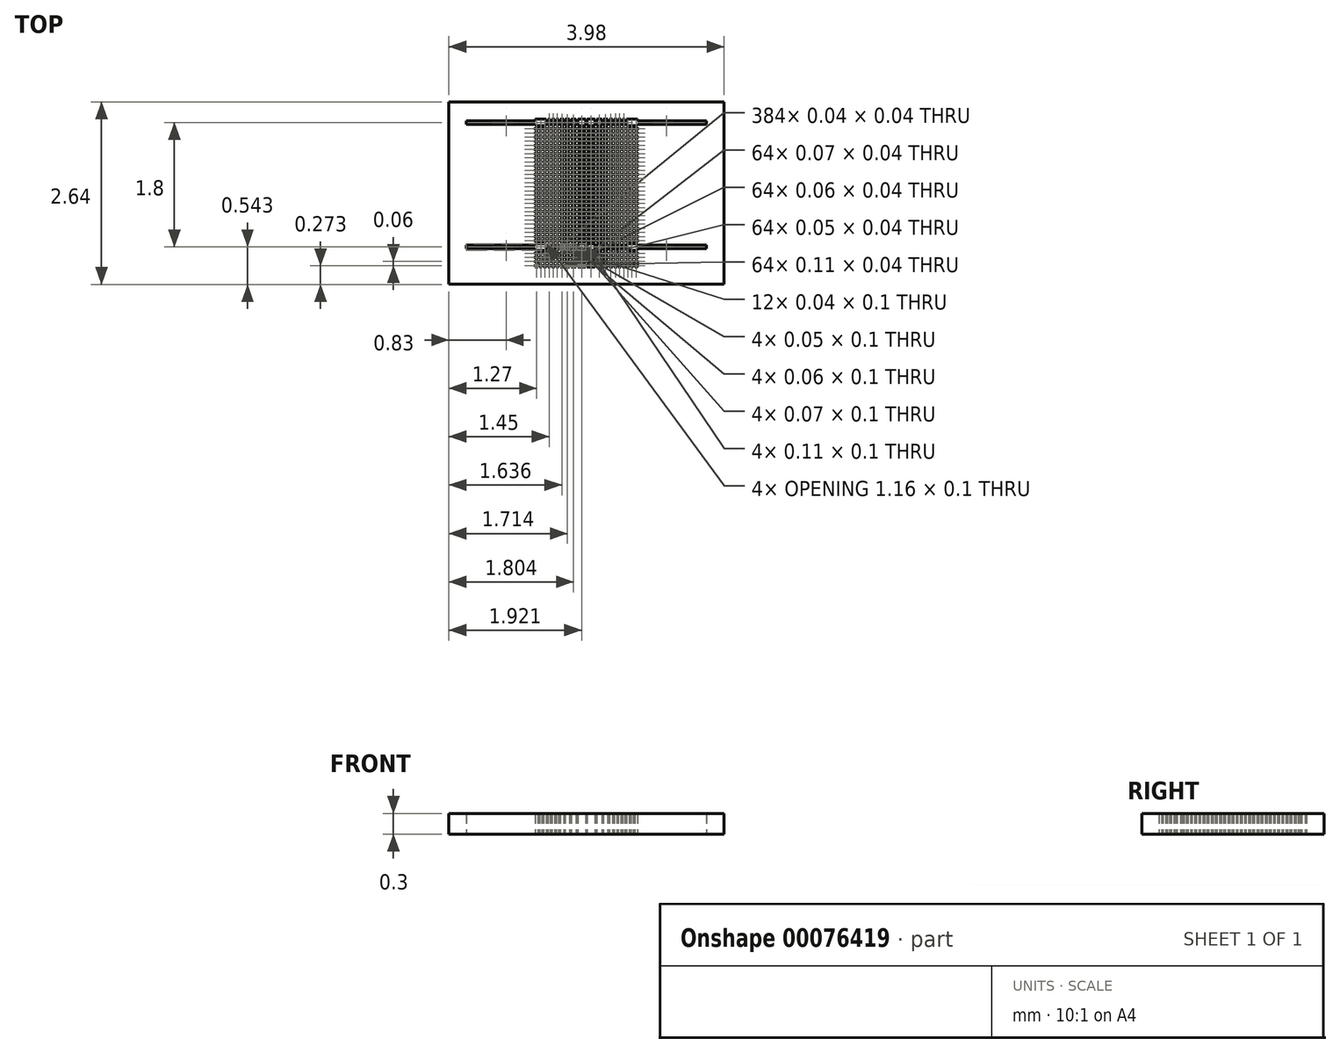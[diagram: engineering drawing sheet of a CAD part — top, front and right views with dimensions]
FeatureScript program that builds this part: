
annotation { "Feature Type Name" : "Feature", "Feature Type Description" : "" }
export const myFeature = defineFeature(function(context is Context, id is Id, definition is map)
    precondition{}
    {
        {
            var Q0;
            Q0=qCreatedBy(makeId("Top.planeOp"),FACE);
            var sketch = newSketch(context, id + "F0", { "sketchPlane" : qUnion([Q0])});
            skLineSegment(sketch, "E0", {"start": v(-0.58, -1.23) * mm, "end": v(-0.58, -1.33) * mm});
            skLineSegment(sketch, "E1", {"start": v(-0.56, -1.23) * mm, "end": v(-0.56, -1.33) * mm});
            skLineSegment(sketch, "E2", {"start": v(-0.52, -1.23) * mm, "end": v(-0.52, -1.33) * mm});
            skLineSegment(sketch, "E3", {"start": v(-0.52, -1.33) * mm, "end": v(-0.56, -1.33) * mm});
            skLineSegment(sketch, "E4", {"start": v(-0.5, -1.23) * mm, "end": v(-0.5, -1.33) * mm});
            skLineSegment(sketch, "E5", {"start": v(-0.46, -1.23) * mm, "end": v(-0.46, -1.33) * mm});
            skLineSegment(sketch, "E6", {"start": v(-0.46, -1.33) * mm, "end": v(-0.5, -1.33) * mm});
            skLineSegment(sketch, "E7", {"start": v(-0.44, -1.23) * mm, "end": v(-0.44, -1.33) * mm});
            skLineSegment(sketch, "E8", {"start": v(-0.4, -1.23) * mm, "end": v(-0.4, -1.33) * mm});
            skLineSegment(sketch, "E9", {"start": v(-0.4, -1.33) * mm, "end": v(-0.44, -1.33) * mm});
            skLineSegment(sketch, "E10", {"start": v(-0.74, -1.35) * mm, "end": v(-0.74, -1.39) * mm});
            skLineSegment(sketch, "E11", {"start": v(-0.7, -1.35) * mm, "end": v(-0.74, -1.35) * mm});
            skLineSegment(sketch, "E12", {"start": v(-0.7, -1.39) * mm, "end": v(-0.74, -1.39) * mm});
            skLineSegment(sketch, "E13", {"start": v(-0.7, -1.35) * mm, "end": v(-0.7, -1.39) * mm});
            skLineSegment(sketch, "E14", {"start": v(-0.7, -1.4) * mm, "end": v(-0.74, -1.4) * mm});
            skLineSegment(sketch, "E15", {"start": v(-0.7, -1.45) * mm, "end": v(-0.74, -1.45) * mm});
            skLineSegment(sketch, "E16", {"start": v(-0.74, -1.4) * mm, "end": v(-0.74, -1.45) * mm});
            skLineSegment(sketch, "E17", {"start": v(-0.7, -1.4) * mm, "end": v(-0.7, -1.45) * mm});
            skLineSegment(sketch, "E18", {"start": v(-0.7, -1.47) * mm, "end": v(-0.74, -1.47) * mm});
            skLineSegment(sketch, "E19", {"start": v(-0.7, -1.5) * mm, "end": v(-0.74, -1.5) * mm});
            skLineSegment(sketch, "E20", {"start": v(-0.74, -1.47) * mm, "end": v(-0.74, -1.5) * mm});
            skLineSegment(sketch, "E21", {"start": v(-0.7, -1.47) * mm, "end": v(-0.7, -1.5) * mm});
            skLineSegment(sketch, "E22", {"start": v(-0.7, -1.53) * mm, "end": v(-0.74, -1.53) * mm});
            skLineSegment(sketch, "E23", {"start": v(-0.7, -1.57) * mm, "end": v(-0.74, -1.57) * mm});
            skLineSegment(sketch, "E24", {"start": v(-0.74, -1.53) * mm, "end": v(-0.74, -1.57) * mm});
            skLineSegment(sketch, "E25", {"start": v(-0.7, -1.53) * mm, "end": v(-0.7, -1.57) * mm});
            skLineSegment(sketch, "E26", {"start": v(-0.7, -1.59) * mm, "end": v(-0.74, -1.59) * mm});
            skLineSegment(sketch, "E27", {"start": v(-0.7, -1.63) * mm, "end": v(-0.74, -1.63) * mm});
            skLineSegment(sketch, "E28", {"start": v(-0.74, -1.59) * mm, "end": v(-0.74, -1.63) * mm});
            skLineSegment(sketch, "E29", {"start": v(-0.7, -1.59) * mm, "end": v(-0.7, -1.63) * mm});
            skLineSegment(sketch, "E30", {"start": v(-0.7, -1.65) * mm, "end": v(-0.74, -1.65) * mm});
            skLineSegment(sketch, "E31", {"start": v(-0.7, -1.69) * mm, "end": v(-0.74, -1.69) * mm});
            skLineSegment(sketch, "E32", {"start": v(-0.74, -1.65) * mm, "end": v(-0.74, -1.69) * mm});
            skLineSegment(sketch, "E33", {"start": v(-0.7, -1.65) * mm, "end": v(-0.7, -1.69) * mm});
            skLineSegment(sketch, "E34", {"start": v(-0.64, -1.35) * mm, "end": v(-0.68, -1.35) * mm});
            skLineSegment(sketch, "E35", {"start": v(-0.64, -1.39) * mm, "end": v(-0.68, -1.39) * mm});
            skLineSegment(sketch, "E36", {"start": v(-0.68, -1.35) * mm, "end": v(-0.68, -1.39) * mm});
            skLineSegment(sketch, "E37", {"start": v(-0.64, -1.35) * mm, "end": v(-0.64, -1.39) * mm});
            skLineSegment(sketch, "E38", {"start": v(-0.64, -1.4) * mm, "end": v(-0.68, -1.4) * mm});
            skLineSegment(sketch, "E39", {"start": v(-0.64, -1.45) * mm, "end": v(-0.68, -1.45) * mm});
            skLineSegment(sketch, "E40", {"start": v(-0.68, -1.4) * mm, "end": v(-0.68, -1.45) * mm});
            skLineSegment(sketch, "E41", {"start": v(-0.64, -1.4) * mm, "end": v(-0.64, -1.45) * mm});
            skLineSegment(sketch, "E42", {"start": v(-0.64, -1.47) * mm, "end": v(-0.68, -1.47) * mm});
            skLineSegment(sketch, "E43", {"start": v(-0.64, -1.5) * mm, "end": v(-0.68, -1.5) * mm});
            skLineSegment(sketch, "E44", {"start": v(-0.68, -1.47) * mm, "end": v(-0.68, -1.5) * mm});
            skLineSegment(sketch, "E45", {"start": v(-0.64, -1.47) * mm, "end": v(-0.64, -1.5) * mm});
            skLineSegment(sketch, "E46", {"start": v(-0.64, -1.53) * mm, "end": v(-0.68, -1.53) * mm});
            skLineSegment(sketch, "E47", {"start": v(-0.64, -1.57) * mm, "end": v(-0.68, -1.57) * mm});
            skLineSegment(sketch, "E48", {"start": v(-0.68, -1.53) * mm, "end": v(-0.68, -1.57) * mm});
            skLineSegment(sketch, "E49", {"start": v(-0.64, -1.53) * mm, "end": v(-0.64, -1.57) * mm});
            skLineSegment(sketch, "E50", {"start": v(-0.64, -1.59) * mm, "end": v(-0.68, -1.59) * mm});
            skLineSegment(sketch, "E51", {"start": v(-0.64, -1.63) * mm, "end": v(-0.68, -1.63) * mm});
            skLineSegment(sketch, "E52", {"start": v(-0.68, -1.59) * mm, "end": v(-0.68, -1.63) * mm});
            skLineSegment(sketch, "E53", {"start": v(-0.64, -1.59) * mm, "end": v(-0.64, -1.63) * mm});
            skLineSegment(sketch, "E54", {"start": v(-0.64, -1.65) * mm, "end": v(-0.68, -1.65) * mm});
            skLineSegment(sketch, "E55", {"start": v(-0.64, -1.69) * mm, "end": v(-0.68, -1.69) * mm});
            skLineSegment(sketch, "E56", {"start": v(-0.68, -1.65) * mm, "end": v(-0.68, -1.69) * mm});
            skLineSegment(sketch, "E57", {"start": v(-0.64, -1.65) * mm, "end": v(-0.64, -1.69) * mm});
            skLineSegment(sketch, "E58", {"start": v(-0.58, -1.35) * mm, "end": v(-0.62, -1.35) * mm});
            skLineSegment(sketch, "E59", {"start": v(-0.58, -1.39) * mm, "end": v(-0.62, -1.39) * mm});
            skLineSegment(sketch, "E60", {"start": v(-0.62, -1.35) * mm, "end": v(-0.62, -1.39) * mm});
            skLineSegment(sketch, "E61", {"start": v(-0.58, -1.35) * mm, "end": v(-0.58, -1.39) * mm});
            skLineSegment(sketch, "E62", {"start": v(-0.58, -1.4) * mm, "end": v(-0.62, -1.4) * mm});
            skLineSegment(sketch, "E63", {"start": v(-0.58, -1.45) * mm, "end": v(-0.62, -1.45) * mm});
            skLineSegment(sketch, "E64", {"start": v(-0.62, -1.4) * mm, "end": v(-0.62, -1.45) * mm});
            skLineSegment(sketch, "E65", {"start": v(-0.58, -1.4) * mm, "end": v(-0.58, -1.45) * mm});
            skLineSegment(sketch, "E66", {"start": v(-0.58, -1.47) * mm, "end": v(-0.62, -1.47) * mm});
            skLineSegment(sketch, "E67", {"start": v(-0.58, -1.5) * mm, "end": v(-0.62, -1.5) * mm});
            skLineSegment(sketch, "E68", {"start": v(-0.62, -1.47) * mm, "end": v(-0.62, -1.5) * mm});
            skLineSegment(sketch, "E69", {"start": v(-0.58, -1.47) * mm, "end": v(-0.58, -1.5) * mm});
            skLineSegment(sketch, "E70", {"start": v(-0.58, -1.53) * mm, "end": v(-0.62, -1.53) * mm});
            skLineSegment(sketch, "E71", {"start": v(-0.58, -1.57) * mm, "end": v(-0.62, -1.57) * mm});
            skLineSegment(sketch, "E72", {"start": v(-0.62, -1.53) * mm, "end": v(-0.62, -1.57) * mm});
            skLineSegment(sketch, "E73", {"start": v(-0.58, -1.53) * mm, "end": v(-0.58, -1.57) * mm});
            skLineSegment(sketch, "E74", {"start": v(-0.58, -1.59) * mm, "end": v(-0.62, -1.59) * mm});
            skLineSegment(sketch, "E75", {"start": v(-0.58, -1.63) * mm, "end": v(-0.62, -1.63) * mm});
            skLineSegment(sketch, "E76", {"start": v(-0.62, -1.59) * mm, "end": v(-0.62, -1.63) * mm});
            skLineSegment(sketch, "E77", {"start": v(-0.58, -1.59) * mm, "end": v(-0.58, -1.63) * mm});
            skLineSegment(sketch, "E78", {"start": v(-0.58, -1.65) * mm, "end": v(-0.62, -1.65) * mm});
            skLineSegment(sketch, "E79", {"start": v(-0.58, -1.69) * mm, "end": v(-0.62, -1.69) * mm});
            skLineSegment(sketch, "E80", {"start": v(-0.62, -1.65) * mm, "end": v(-0.62, -1.69) * mm});
            skLineSegment(sketch, "E81", {"start": v(-0.58, -1.65) * mm, "end": v(-0.58, -1.69) * mm});
            skLineSegment(sketch, "E82", {"start": v(-0.52, -1.35) * mm, "end": v(-0.56, -1.35) * mm});
            skLineSegment(sketch, "E83", {"start": v(-0.52, -1.39) * mm, "end": v(-0.56, -1.39) * mm});
            skLineSegment(sketch, "E84", {"start": v(-0.56, -1.35) * mm, "end": v(-0.56, -1.39) * mm});
            skLineSegment(sketch, "E85", {"start": v(-0.52, -1.35) * mm, "end": v(-0.52, -1.39) * mm});
            skLineSegment(sketch, "E86", {"start": v(-0.52, -1.4) * mm, "end": v(-0.56, -1.4) * mm});
            skLineSegment(sketch, "E87", {"start": v(-0.52, -1.45) * mm, "end": v(-0.56, -1.45) * mm});
            skLineSegment(sketch, "E88", {"start": v(-0.56, -1.4) * mm, "end": v(-0.56, -1.45) * mm});
            skLineSegment(sketch, "E89", {"start": v(-0.52, -1.4) * mm, "end": v(-0.52, -1.45) * mm});
            skLineSegment(sketch, "E90", {"start": v(-0.52, -1.47) * mm, "end": v(-0.56, -1.47) * mm});
            skLineSegment(sketch, "E91", {"start": v(-0.52, -1.5) * mm, "end": v(-0.56, -1.5) * mm});
            skLineSegment(sketch, "E92", {"start": v(-0.56, -1.47) * mm, "end": v(-0.56, -1.5) * mm});
            skLineSegment(sketch, "E93", {"start": v(-0.52, -1.47) * mm, "end": v(-0.52, -1.5) * mm});
            skLineSegment(sketch, "E94", {"start": v(-0.52, -1.53) * mm, "end": v(-0.56, -1.53) * mm});
            skLineSegment(sketch, "E95", {"start": v(-0.52, -1.57) * mm, "end": v(-0.56, -1.57) * mm});
            skLineSegment(sketch, "E96", {"start": v(-0.56, -1.53) * mm, "end": v(-0.56, -1.57) * mm});
            skLineSegment(sketch, "E97", {"start": v(-0.52, -1.53) * mm, "end": v(-0.52, -1.57) * mm});
            skLineSegment(sketch, "E98", {"start": v(-0.52, -1.59) * mm, "end": v(-0.56, -1.59) * mm});
            skLineSegment(sketch, "E99", {"start": v(-0.52, -1.63) * mm, "end": v(-0.56, -1.63) * mm});
            skLineSegment(sketch, "E100", {"start": v(-0.56, -1.59) * mm, "end": v(-0.56, -1.63) * mm});
            skLineSegment(sketch, "E101", {"start": v(-0.52, -1.59) * mm, "end": v(-0.52, -1.63) * mm});
            skLineSegment(sketch, "E102", {"start": v(-0.52, -1.65) * mm, "end": v(-0.56, -1.65) * mm});
            skLineSegment(sketch, "E103", {"start": v(-0.52, -1.69) * mm, "end": v(-0.56, -1.69) * mm});
            skLineSegment(sketch, "E104", {"start": v(-0.56, -1.65) * mm, "end": v(-0.56, -1.69) * mm});
            skLineSegment(sketch, "E105", {"start": v(-0.52, -1.65) * mm, "end": v(-0.52, -1.69) * mm});
            skLineSegment(sketch, "E106", {"start": v(-0.46, -1.35) * mm, "end": v(-0.5, -1.35) * mm});
            skLineSegment(sketch, "E107", {"start": v(-0.46, -1.39) * mm, "end": v(-0.5, -1.39) * mm});
            skLineSegment(sketch, "E108", {"start": v(-0.5, -1.35) * mm, "end": v(-0.5, -1.39) * mm});
            skLineSegment(sketch, "E109", {"start": v(-0.46, -1.35) * mm, "end": v(-0.46, -1.39) * mm});
            skLineSegment(sketch, "E110", {"start": v(-0.46, -1.4) * mm, "end": v(-0.5, -1.4) * mm});
            skLineSegment(sketch, "E111", {"start": v(-0.46, -1.45) * mm, "end": v(-0.5, -1.45) * mm});
            skLineSegment(sketch, "E112", {"start": v(-0.5, -1.4) * mm, "end": v(-0.5, -1.45) * mm});
            skLineSegment(sketch, "E113", {"start": v(-0.46, -1.4) * mm, "end": v(-0.46, -1.45) * mm});
            skLineSegment(sketch, "E114", {"start": v(-0.46, -1.47) * mm, "end": v(-0.5, -1.47) * mm});
            skLineSegment(sketch, "E115", {"start": v(-0.46, -1.5) * mm, "end": v(-0.5, -1.5) * mm});
            skLineSegment(sketch, "E116", {"start": v(-0.5, -1.47) * mm, "end": v(-0.5, -1.5) * mm});
            skLineSegment(sketch, "E117", {"start": v(-0.46, -1.47) * mm, "end": v(-0.46, -1.5) * mm});
            skLineSegment(sketch, "E118", {"start": v(-0.46, -1.53) * mm, "end": v(-0.5, -1.53) * mm});
            skLineSegment(sketch, "E119", {"start": v(-0.46, -1.57) * mm, "end": v(-0.5, -1.57) * mm});
            skLineSegment(sketch, "E120", {"start": v(-0.5, -1.53) * mm, "end": v(-0.5, -1.57) * mm});
            skLineSegment(sketch, "E121", {"start": v(-0.46, -1.53) * mm, "end": v(-0.46, -1.57) * mm});
            skLineSegment(sketch, "E122", {"start": v(-0.46, -1.59) * mm, "end": v(-0.5, -1.59) * mm});
            skLineSegment(sketch, "E123", {"start": v(-0.46, -1.63) * mm, "end": v(-0.5, -1.63) * mm});
            skLineSegment(sketch, "E124", {"start": v(-0.5, -1.59) * mm, "end": v(-0.5, -1.63) * mm});
            skLineSegment(sketch, "E125", {"start": v(-0.46, -1.59) * mm, "end": v(-0.46, -1.63) * mm});
            skLineSegment(sketch, "E126", {"start": v(-0.46, -1.65) * mm, "end": v(-0.5, -1.65) * mm});
            skLineSegment(sketch, "E127", {"start": v(-0.46, -1.69) * mm, "end": v(-0.5, -1.69) * mm});
            skLineSegment(sketch, "E128", {"start": v(-0.5, -1.65) * mm, "end": v(-0.5, -1.69) * mm});
            skLineSegment(sketch, "E129", {"start": v(-0.46, -1.65) * mm, "end": v(-0.46, -1.69) * mm});
            skLineSegment(sketch, "E130", {"start": v(-0.4, -1.35) * mm, "end": v(-0.44, -1.35) * mm});
            skLineSegment(sketch, "E131", {"start": v(-0.4, -1.39) * mm, "end": v(-0.44, -1.39) * mm});
            skLineSegment(sketch, "E132", {"start": v(-0.44, -1.35) * mm, "end": v(-0.44, -1.39) * mm});
            skLineSegment(sketch, "E133", {"start": v(-0.4, -1.35) * mm, "end": v(-0.4, -1.39) * mm});
            skLineSegment(sketch, "E134", {"start": v(-0.4, -1.4) * mm, "end": v(-0.44, -1.4) * mm});
            skLineSegment(sketch, "E135", {"start": v(-0.4, -1.45) * mm, "end": v(-0.44, -1.45) * mm});
            skLineSegment(sketch, "E136", {"start": v(-0.44, -1.4) * mm, "end": v(-0.44, -1.45) * mm});
            skLineSegment(sketch, "E137", {"start": v(-0.4, -1.4) * mm, "end": v(-0.4, -1.45) * mm});
            skLineSegment(sketch, "E138", {"start": v(-0.4, -1.47) * mm, "end": v(-0.44, -1.47) * mm});
            skLineSegment(sketch, "E139", {"start": v(-0.4, -1.5) * mm, "end": v(-0.44, -1.5) * mm});
            skLineSegment(sketch, "E140", {"start": v(-0.44, -1.47) * mm, "end": v(-0.44, -1.5) * mm});
            skLineSegment(sketch, "E141", {"start": v(-0.4, -1.47) * mm, "end": v(-0.4, -1.5) * mm});
            skLineSegment(sketch, "E142", {"start": v(-0.4, -1.53) * mm, "end": v(-0.44, -1.53) * mm});
            skLineSegment(sketch, "E143", {"start": v(-0.4, -1.57) * mm, "end": v(-0.44, -1.57) * mm});
            skLineSegment(sketch, "E144", {"start": v(-0.44, -1.53) * mm, "end": v(-0.44, -1.57) * mm});
            skLineSegment(sketch, "E145", {"start": v(-0.4, -1.53) * mm, "end": v(-0.4, -1.57) * mm});
            skLineSegment(sketch, "E146", {"start": v(-0.4, -1.59) * mm, "end": v(-0.44, -1.59) * mm});
            skLineSegment(sketch, "E147", {"start": v(-0.4, -1.63) * mm, "end": v(-0.44, -1.63) * mm});
            skLineSegment(sketch, "E148", {"start": v(-0.44, -1.59) * mm, "end": v(-0.44, -1.63) * mm});
            skLineSegment(sketch, "E149", {"start": v(-0.4, -1.59) * mm, "end": v(-0.4, -1.63) * mm});
            skLineSegment(sketch, "E150", {"start": v(-0.4, -1.65) * mm, "end": v(-0.44, -1.65) * mm});
            skLineSegment(sketch, "E151", {"start": v(-0.4, -1.69) * mm, "end": v(-0.44, -1.69) * mm});
            skLineSegment(sketch, "E152", {"start": v(-0.44, -1.65) * mm, "end": v(-0.44, -1.69) * mm});
            skLineSegment(sketch, "E153", {"start": v(-0.4, -1.65) * mm, "end": v(-0.4, -1.69) * mm});
            skLineSegment(sketch, "E154", {"start": v(-0.38, -1.23) * mm, "end": v(-0.38, -1.33) * mm});
            skLineSegment(sketch, "E155", {"start": v(-0.38, -1.35) * mm, "end": v(-0.38, -1.39) * mm});
            skLineSegment(sketch, "E156", {"start": v(-0.33, -1.23) * mm, "end": v(-0.33, -1.33) * mm});
            skLineSegment(sketch, "E157", {"start": v(-0.33, -1.35) * mm, "end": v(-0.33, -1.39) * mm});
            skLineSegment(sketch, "E158", {"start": v(-0.3, -1.23) * mm, "end": v(-0.3, -1.33) * mm});
            skLineSegment(sketch, "E159", {"start": v(-0.3, -1.35) * mm, "end": v(-0.3, -1.39) * mm});
            skLineSegment(sketch, "E160", {"start": v(-0.25, -1.23) * mm, "end": v(-0.25, -1.33) * mm});
            skLineSegment(sketch, "E161", {"start": v(-0.25, -1.35) * mm, "end": v(-0.25, -1.39) * mm});
            skLineSegment(sketch, "E162", {"start": v(-0.22, -1.23) * mm, "end": v(-0.22, -1.33) * mm});
            skLineSegment(sketch, "E163", {"start": v(-0.22, -1.35) * mm, "end": v(-0.22, -1.39) * mm});
            skLineSegment(sketch, "E164", {"start": v(-0.15, -1.23) * mm, "end": v(-0.15, -1.33) * mm});
            skLineSegment(sketch, "E165", {"start": v(-0.15, -1.35) * mm, "end": v(-0.15, -1.39) * mm});
            skLineSegment(sketch, "E166", {"start": v(-0.13, -1.23) * mm, "end": v(-0.13, -1.33) * mm});
            skLineSegment(sketch, "E167", {"start": v(-0.13, -1.35) * mm, "end": v(-0.13, -1.39) * mm});
            skLineSegment(sketch, "E168", {"start": v(-0.01, -1.23) * mm, "end": v(-0.01, -1.33) * mm});
            skLineSegment(sketch, "E169", {"start": v(-0.13, -1.35) * mm, "end": v(-0.01, -1.35) * mm});
            skLineSegment(sketch, "E170", {"start": v(-0.13, -1.33) * mm, "end": v(-0.01, -1.33) * mm});
            skLineSegment(sketch, "E171", {"start": v(-0.13, -1.39) * mm, "end": v(-0.01, -1.39) * mm});
            skLineSegment(sketch, "E172", {"start": v(-0.15, -1.35) * mm, "end": v(-0.22, -1.35) * mm});
            skLineSegment(sketch, "E173", {"start": v(-0.22, -1.39) * mm, "end": v(-0.15, -1.39) * mm});
            skLineSegment(sketch, "E174", {"start": v(-0.25, -1.35) * mm, "end": v(-0.3, -1.35) * mm});
            skLineSegment(sketch, "E175", {"start": v(-0.3, -1.39) * mm, "end": v(-0.25, -1.39) * mm});
            skLineSegment(sketch, "E176", {"start": v(-0.33, -1.35) * mm, "end": v(-0.38, -1.35) * mm});
            skLineSegment(sketch, "E177", {"start": v(-0.38, -1.39) * mm, "end": v(-0.33, -1.39) * mm});
            skLineSegment(sketch, "E178", {"start": v(-0.38, -1.33) * mm, "end": v(-0.33, -1.33) * mm});
            skLineSegment(sketch, "E179", {"start": v(-0.3, -1.33) * mm, "end": v(-0.25, -1.33) * mm});
            skLineSegment(sketch, "E180", {"start": v(-0.22, -1.33) * mm, "end": v(-0.15, -1.33) * mm});
            skLineSegment(sketch, "E181", {"start": v(-0.01, -1.35) * mm, "end": v(-0.01, -1.39) * mm});
            skLineSegment(sketch, "E182", {"start": v(-0.01, -1.4) * mm, "end": v(-0.01, -1.45) * mm});
            skLineSegment(sketch, "E183", {"start": v(-0.38, -1.4) * mm, "end": v(-0.38, -1.45) * mm});
            skLineSegment(sketch, "E184", {"start": v(-0.33, -1.4) * mm, "end": v(-0.33, -1.45) * mm});
            skLineSegment(sketch, "E185", {"start": v(-0.3, -1.4) * mm, "end": v(-0.3, -1.45) * mm});
            skLineSegment(sketch, "E186", {"start": v(-0.25, -1.4) * mm, "end": v(-0.25, -1.45) * mm});
            skLineSegment(sketch, "E187", {"start": v(-0.22, -1.4) * mm, "end": v(-0.22, -1.45) * mm});
            skLineSegment(sketch, "E188", {"start": v(-0.15, -1.4) * mm, "end": v(-0.15, -1.45) * mm});
            skLineSegment(sketch, "E189", {"start": v(-0.13, -1.4) * mm, "end": v(-0.13, -1.45) * mm});
            skLineSegment(sketch, "E190", {"start": v(-0.13, -1.4) * mm, "end": v(-0.01, -1.4) * mm});
            skLineSegment(sketch, "E191", {"start": v(-0.13, -1.45) * mm, "end": v(-0.01, -1.45) * mm});
            skLineSegment(sketch, "E192", {"start": v(-0.15, -1.4) * mm, "end": v(-0.22, -1.4) * mm});
            skLineSegment(sketch, "E193", {"start": v(-0.22, -1.45) * mm, "end": v(-0.15, -1.45) * mm});
            skLineSegment(sketch, "E194", {"start": v(-0.25, -1.4) * mm, "end": v(-0.3, -1.4) * mm});
            skLineSegment(sketch, "E195", {"start": v(-0.3, -1.45) * mm, "end": v(-0.25, -1.45) * mm});
            skLineSegment(sketch, "E196", {"start": v(-0.33, -1.4) * mm, "end": v(-0.38, -1.4) * mm});
            skLineSegment(sketch, "E197", {"start": v(-0.38, -1.45) * mm, "end": v(-0.33, -1.45) * mm});
            skLineSegment(sketch, "E198", {"start": v(-0.01, -1.47) * mm, "end": v(-0.01, -1.5) * mm});
            skLineSegment(sketch, "E199", {"start": v(-0.38, -1.47) * mm, "end": v(-0.38, -1.5) * mm});
            skLineSegment(sketch, "E200", {"start": v(-0.33, -1.47) * mm, "end": v(-0.33, -1.5) * mm});
            skLineSegment(sketch, "E201", {"start": v(-0.3, -1.47) * mm, "end": v(-0.3, -1.5) * mm});
            skLineSegment(sketch, "E202", {"start": v(-0.25, -1.47) * mm, "end": v(-0.25, -1.5) * mm});
            skLineSegment(sketch, "E203", {"start": v(-0.22, -1.47) * mm, "end": v(-0.22, -1.5) * mm});
            skLineSegment(sketch, "E204", {"start": v(-0.15, -1.47) * mm, "end": v(-0.15, -1.5) * mm});
            skLineSegment(sketch, "E205", {"start": v(-0.13, -1.47) * mm, "end": v(-0.13, -1.5) * mm});
            skLineSegment(sketch, "E206", {"start": v(-0.13, -1.47) * mm, "end": v(-0.01, -1.47) * mm});
            skLineSegment(sketch, "E207", {"start": v(-0.13, -1.5) * mm, "end": v(-0.01, -1.5) * mm});
            skLineSegment(sketch, "E208", {"start": v(-0.15, -1.47) * mm, "end": v(-0.22, -1.47) * mm});
            skLineSegment(sketch, "E209", {"start": v(-0.22, -1.5) * mm, "end": v(-0.15, -1.5) * mm});
            skLineSegment(sketch, "E210", {"start": v(-0.25, -1.47) * mm, "end": v(-0.3, -1.47) * mm});
            skLineSegment(sketch, "E211", {"start": v(-0.3, -1.5) * mm, "end": v(-0.25, -1.5) * mm});
            skLineSegment(sketch, "E212", {"start": v(-0.33, -1.47) * mm, "end": v(-0.38, -1.47) * mm});
            skLineSegment(sketch, "E213", {"start": v(-0.38, -1.5) * mm, "end": v(-0.33, -1.5) * mm});
            skLineSegment(sketch, "E214", {"start": v(-0.01, -1.53) * mm, "end": v(-0.01, -1.57) * mm});
            skLineSegment(sketch, "E215", {"start": v(-0.38, -1.53) * mm, "end": v(-0.38, -1.57) * mm});
            skLineSegment(sketch, "E216", {"start": v(-0.33, -1.53) * mm, "end": v(-0.33, -1.57) * mm});
            skLineSegment(sketch, "E217", {"start": v(-0.3, -1.53) * mm, "end": v(-0.3, -1.57) * mm});
            skLineSegment(sketch, "E218", {"start": v(-0.25, -1.53) * mm, "end": v(-0.25, -1.57) * mm});
            skLineSegment(sketch, "E219", {"start": v(-0.22, -1.53) * mm, "end": v(-0.22, -1.57) * mm});
            skLineSegment(sketch, "E220", {"start": v(-0.15, -1.53) * mm, "end": v(-0.15, -1.57) * mm});
            skLineSegment(sketch, "E221", {"start": v(-0.13, -1.53) * mm, "end": v(-0.13, -1.57) * mm});
            skLineSegment(sketch, "E222", {"start": v(-0.13, -1.53) * mm, "end": v(-0.01, -1.53) * mm});
            skLineSegment(sketch, "E223", {"start": v(-0.13, -1.57) * mm, "end": v(-0.01, -1.57) * mm});
            skLineSegment(sketch, "E224", {"start": v(-0.15, -1.53) * mm, "end": v(-0.22, -1.53) * mm});
            skLineSegment(sketch, "E225", {"start": v(-0.22, -1.57) * mm, "end": v(-0.15, -1.57) * mm});
            skLineSegment(sketch, "E226", {"start": v(-0.25, -1.53) * mm, "end": v(-0.3, -1.53) * mm});
            skLineSegment(sketch, "E227", {"start": v(-0.3, -1.57) * mm, "end": v(-0.25, -1.57) * mm});
            skLineSegment(sketch, "E228", {"start": v(-0.33, -1.53) * mm, "end": v(-0.38, -1.53) * mm});
            skLineSegment(sketch, "E229", {"start": v(-0.38, -1.57) * mm, "end": v(-0.33, -1.57) * mm});
            skLineSegment(sketch, "E230", {"start": v(-0.01, -1.59) * mm, "end": v(-0.01, -1.63) * mm});
            skLineSegment(sketch, "E231", {"start": v(-0.38, -1.59) * mm, "end": v(-0.38, -1.63) * mm});
            skLineSegment(sketch, "E232", {"start": v(-0.33, -1.59) * mm, "end": v(-0.33, -1.63) * mm});
            skLineSegment(sketch, "E233", {"start": v(-0.3, -1.59) * mm, "end": v(-0.3, -1.63) * mm});
            skLineSegment(sketch, "E234", {"start": v(-0.25, -1.59) * mm, "end": v(-0.25, -1.63) * mm});
            skLineSegment(sketch, "E235", {"start": v(-0.22, -1.59) * mm, "end": v(-0.22, -1.63) * mm});
            skLineSegment(sketch, "E236", {"start": v(-0.15, -1.59) * mm, "end": v(-0.15, -1.63) * mm});
            skLineSegment(sketch, "E237", {"start": v(-0.13, -1.59) * mm, "end": v(-0.13, -1.63) * mm});
            skLineSegment(sketch, "E238", {"start": v(-0.13, -1.59) * mm, "end": v(-0.01, -1.59) * mm});
            skLineSegment(sketch, "E239", {"start": v(-0.13, -1.63) * mm, "end": v(-0.01, -1.63) * mm});
            skLineSegment(sketch, "E240", {"start": v(-0.15, -1.59) * mm, "end": v(-0.22, -1.59) * mm});
            skLineSegment(sketch, "E241", {"start": v(-0.22, -1.63) * mm, "end": v(-0.15, -1.63) * mm});
            skLineSegment(sketch, "E242", {"start": v(-0.25, -1.59) * mm, "end": v(-0.3, -1.59) * mm});
            skLineSegment(sketch, "E243", {"start": v(-0.3, -1.63) * mm, "end": v(-0.25, -1.63) * mm});
            skLineSegment(sketch, "E244", {"start": v(-0.33, -1.59) * mm, "end": v(-0.38, -1.59) * mm});
            skLineSegment(sketch, "E245", {"start": v(-0.38, -1.63) * mm, "end": v(-0.33, -1.63) * mm});
            skLineSegment(sketch, "E246", {"start": v(-0.01, -1.65) * mm, "end": v(-0.01, -1.69) * mm});
            skLineSegment(sketch, "E247", {"start": v(-0.38, -1.65) * mm, "end": v(-0.38, -1.69) * mm});
            skLineSegment(sketch, "E248", {"start": v(-0.33, -1.65) * mm, "end": v(-0.33, -1.69) * mm});
            skLineSegment(sketch, "E249", {"start": v(-0.3, -1.65) * mm, "end": v(-0.3, -1.69) * mm});
            skLineSegment(sketch, "E250", {"start": v(-0.25, -1.65) * mm, "end": v(-0.25, -1.69) * mm});
            skLineSegment(sketch, "E251", {"start": v(-0.22, -1.65) * mm, "end": v(-0.22, -1.69) * mm});
            skLineSegment(sketch, "E252", {"start": v(-0.15, -1.65) * mm, "end": v(-0.15, -1.69) * mm});
            skLineSegment(sketch, "E253", {"start": v(-0.13, -1.65) * mm, "end": v(-0.13, -1.69) * mm});
            skLineSegment(sketch, "E254", {"start": v(-0.13, -1.65) * mm, "end": v(-0.01, -1.65) * mm});
            skLineSegment(sketch, "E255", {"start": v(-0.13, -1.69) * mm, "end": v(-0.01, -1.69) * mm});
            skLineSegment(sketch, "E256", {"start": v(-0.15, -1.65) * mm, "end": v(-0.22, -1.65) * mm});
            skLineSegment(sketch, "E257", {"start": v(-0.22, -1.69) * mm, "end": v(-0.15, -1.69) * mm});
            skLineSegment(sketch, "E258", {"start": v(-0.25, -1.65) * mm, "end": v(-0.3, -1.65) * mm});
            skLineSegment(sketch, "E259", {"start": v(-0.3, -1.69) * mm, "end": v(-0.25, -1.69) * mm});
            skLineSegment(sketch, "E260", {"start": v(-0.33, -1.65) * mm, "end": v(-0.38, -1.65) * mm});
            skLineSegment(sketch, "E261", {"start": v(-0.38, -1.69) * mm, "end": v(-0.33, -1.69) * mm});
            skLineSegment(sketch, "E262", {"start": v(-0.7, -1.7) * mm, "end": v(-0.74, -1.7) * mm});
            skLineSegment(sketch, "E263", {"start": v(-0.7, -1.75) * mm, "end": v(-0.74, -1.75) * mm});
            skLineSegment(sketch, "E264", {"start": v(-0.74, -1.7) * mm, "end": v(-0.74, -1.75) * mm});
            skLineSegment(sketch, "E265", {"start": v(-0.7, -1.7) * mm, "end": v(-0.7, -1.75) * mm});
            skLineSegment(sketch, "E266", {"start": v(-0.64, -1.7) * mm, "end": v(-0.68, -1.7) * mm});
            skLineSegment(sketch, "E267", {"start": v(-0.64, -1.75) * mm, "end": v(-0.68, -1.75) * mm});
            skLineSegment(sketch, "E268", {"start": v(-0.68, -1.7) * mm, "end": v(-0.68, -1.75) * mm});
            skLineSegment(sketch, "E269", {"start": v(-0.64, -1.7) * mm, "end": v(-0.64, -1.75) * mm});
            skLineSegment(sketch, "E270", {"start": v(-0.58, -1.7) * mm, "end": v(-0.62, -1.7) * mm});
            skLineSegment(sketch, "E271", {"start": v(-0.58, -1.75) * mm, "end": v(-0.62, -1.75) * mm});
            skLineSegment(sketch, "E272", {"start": v(-0.62, -1.7) * mm, "end": v(-0.62, -1.75) * mm});
            skLineSegment(sketch, "E273", {"start": v(-0.58, -1.7) * mm, "end": v(-0.58, -1.75) * mm});
            skLineSegment(sketch, "E274", {"start": v(-0.52, -1.7) * mm, "end": v(-0.56, -1.7) * mm});
            skLineSegment(sketch, "E275", {"start": v(-0.52, -1.75) * mm, "end": v(-0.56, -1.75) * mm});
            skLineSegment(sketch, "E276", {"start": v(-0.56, -1.7) * mm, "end": v(-0.56, -1.75) * mm});
            skLineSegment(sketch, "E277", {"start": v(-0.52, -1.7) * mm, "end": v(-0.52, -1.75) * mm});
            skLineSegment(sketch, "E278", {"start": v(-0.46, -1.7) * mm, "end": v(-0.5, -1.7) * mm});
            skLineSegment(sketch, "E279", {"start": v(-0.46, -1.75) * mm, "end": v(-0.5, -1.75) * mm});
            skLineSegment(sketch, "E280", {"start": v(-0.5, -1.7) * mm, "end": v(-0.5, -1.75) * mm});
            skLineSegment(sketch, "E281", {"start": v(-0.46, -1.7) * mm, "end": v(-0.46, -1.75) * mm});
            skLineSegment(sketch, "E282", {"start": v(-0.4, -1.7) * mm, "end": v(-0.44, -1.7) * mm});
            skLineSegment(sketch, "E283", {"start": v(-0.4, -1.75) * mm, "end": v(-0.44, -1.75) * mm});
            skLineSegment(sketch, "E284", {"start": v(-0.44, -1.7) * mm, "end": v(-0.44, -1.75) * mm});
            skLineSegment(sketch, "E285", {"start": v(-0.4, -1.7) * mm, "end": v(-0.4, -1.75) * mm});
            skLineSegment(sketch, "E286", {"start": v(-0.01, -1.7) * mm, "end": v(-0.01, -1.75) * mm});
            skLineSegment(sketch, "E287", {"start": v(-0.38, -1.7) * mm, "end": v(-0.38, -1.75) * mm});
            skLineSegment(sketch, "E288", {"start": v(-0.33, -1.7) * mm, "end": v(-0.33, -1.75) * mm});
            skLineSegment(sketch, "E289", {"start": v(-0.3, -1.7) * mm, "end": v(-0.3, -1.75) * mm});
            skLineSegment(sketch, "E290", {"start": v(-0.25, -1.7) * mm, "end": v(-0.25, -1.75) * mm});
            skLineSegment(sketch, "E291", {"start": v(-0.22, -1.7) * mm, "end": v(-0.22, -1.75) * mm});
            skLineSegment(sketch, "E292", {"start": v(-0.15, -1.7) * mm, "end": v(-0.15, -1.75) * mm});
            skLineSegment(sketch, "E293", {"start": v(-0.13, -1.7) * mm, "end": v(-0.13, -1.75) * mm});
            skLineSegment(sketch, "E294", {"start": v(-0.13, -1.7) * mm, "end": v(-0.01, -1.7) * mm});
            skLineSegment(sketch, "E295", {"start": v(-0.13, -1.75) * mm, "end": v(-0.01, -1.75) * mm});
            skLineSegment(sketch, "E296", {"start": v(-0.15, -1.7) * mm, "end": v(-0.22, -1.7) * mm});
            skLineSegment(sketch, "E297", {"start": v(-0.22, -1.75) * mm, "end": v(-0.15, -1.75) * mm});
            skLineSegment(sketch, "E298", {"start": v(-0.25, -1.7) * mm, "end": v(-0.3, -1.7) * mm});
            skLineSegment(sketch, "E299", {"start": v(-0.3, -1.75) * mm, "end": v(-0.25, -1.75) * mm});
            skLineSegment(sketch, "E300", {"start": v(-0.33, -1.7) * mm, "end": v(-0.38, -1.7) * mm});
            skLineSegment(sketch, "E301", {"start": v(-0.38, -1.75) * mm, "end": v(-0.33, -1.75) * mm});
            skLineSegment(sketch, "E302", {"start": v(-0.7, -1.77) * mm, "end": v(-0.74, -1.77) * mm});
            skLineSegment(sketch, "E303", {"start": v(-0.7, -1.8) * mm, "end": v(-0.74, -1.8) * mm});
            skLineSegment(sketch, "E304", {"start": v(-0.74, -1.77) * mm, "end": v(-0.74, -1.8) * mm});
            skLineSegment(sketch, "E305", {"start": v(-0.7, -1.77) * mm, "end": v(-0.7, -1.8) * mm});
            skLineSegment(sketch, "E306", {"start": v(-0.64, -1.77) * mm, "end": v(-0.68, -1.77) * mm});
            skLineSegment(sketch, "E307", {"start": v(-0.64, -1.8) * mm, "end": v(-0.68, -1.8) * mm});
            skLineSegment(sketch, "E308", {"start": v(-0.68, -1.77) * mm, "end": v(-0.68, -1.8) * mm});
            skLineSegment(sketch, "E309", {"start": v(-0.64, -1.77) * mm, "end": v(-0.64, -1.8) * mm});
            skLineSegment(sketch, "E310", {"start": v(-0.58, -1.77) * mm, "end": v(-0.62, -1.77) * mm});
            skLineSegment(sketch, "E311", {"start": v(-0.58, -1.8) * mm, "end": v(-0.62, -1.8) * mm});
            skLineSegment(sketch, "E312", {"start": v(-0.62, -1.77) * mm, "end": v(-0.62, -1.8) * mm});
            skLineSegment(sketch, "E313", {"start": v(-0.58, -1.77) * mm, "end": v(-0.58, -1.8) * mm});
            skLineSegment(sketch, "E314", {"start": v(-0.52, -1.77) * mm, "end": v(-0.56, -1.77) * mm});
            skLineSegment(sketch, "E315", {"start": v(-0.52, -1.8) * mm, "end": v(-0.56, -1.8) * mm});
            skLineSegment(sketch, "E316", {"start": v(-0.56, -1.77) * mm, "end": v(-0.56, -1.8) * mm});
            skLineSegment(sketch, "E317", {"start": v(-0.52, -1.77) * mm, "end": v(-0.52, -1.8) * mm});
            skLineSegment(sketch, "E318", {"start": v(-0.46, -1.77) * mm, "end": v(-0.5, -1.77) * mm});
            skLineSegment(sketch, "E319", {"start": v(-0.46, -1.8) * mm, "end": v(-0.5, -1.8) * mm});
            skLineSegment(sketch, "E320", {"start": v(-0.5, -1.77) * mm, "end": v(-0.5, -1.8) * mm});
            skLineSegment(sketch, "E321", {"start": v(-0.46, -1.77) * mm, "end": v(-0.46, -1.8) * mm});
            skLineSegment(sketch, "E322", {"start": v(-0.4, -1.77) * mm, "end": v(-0.44, -1.77) * mm});
            skLineSegment(sketch, "E323", {"start": v(-0.4, -1.8) * mm, "end": v(-0.44, -1.8) * mm});
            skLineSegment(sketch, "E324", {"start": v(-0.44, -1.77) * mm, "end": v(-0.44, -1.8) * mm});
            skLineSegment(sketch, "E325", {"start": v(-0.4, -1.77) * mm, "end": v(-0.4, -1.8) * mm});
            skLineSegment(sketch, "E326", {"start": v(-0.01, -1.77) * mm, "end": v(-0.01, -1.8) * mm});
            skLineSegment(sketch, "E327", {"start": v(-0.38, -1.77) * mm, "end": v(-0.38, -1.8) * mm});
            skLineSegment(sketch, "E328", {"start": v(-0.33, -1.77) * mm, "end": v(-0.33, -1.8) * mm});
            skLineSegment(sketch, "E329", {"start": v(-0.3, -1.77) * mm, "end": v(-0.3, -1.8) * mm});
            skLineSegment(sketch, "E330", {"start": v(-0.25, -1.77) * mm, "end": v(-0.25, -1.8) * mm});
            skLineSegment(sketch, "E331", {"start": v(-0.22, -1.77) * mm, "end": v(-0.22, -1.8) * mm});
            skLineSegment(sketch, "E332", {"start": v(-0.15, -1.77) * mm, "end": v(-0.15, -1.8) * mm});
            skLineSegment(sketch, "E333", {"start": v(-0.13, -1.77) * mm, "end": v(-0.13, -1.8) * mm});
            skLineSegment(sketch, "E334", {"start": v(-0.13, -1.77) * mm, "end": v(-0.01, -1.77) * mm});
            skLineSegment(sketch, "E335", {"start": v(-0.13, -1.8) * mm, "end": v(-0.01, -1.8) * mm});
            skLineSegment(sketch, "E336", {"start": v(-0.15, -1.77) * mm, "end": v(-0.22, -1.77) * mm});
            skLineSegment(sketch, "E337", {"start": v(-0.22, -1.8) * mm, "end": v(-0.15, -1.8) * mm});
            skLineSegment(sketch, "E338", {"start": v(-0.25, -1.77) * mm, "end": v(-0.3, -1.77) * mm});
            skLineSegment(sketch, "E339", {"start": v(-0.3, -1.8) * mm, "end": v(-0.25, -1.8) * mm});
            skLineSegment(sketch, "E340", {"start": v(-0.33, -1.77) * mm, "end": v(-0.38, -1.77) * mm});
            skLineSegment(sketch, "E341", {"start": v(-0.38, -1.8) * mm, "end": v(-0.33, -1.8) * mm});
            skLineSegment(sketch, "E342", {"start": v(-0.7, -1.83) * mm, "end": v(-0.74, -1.83) * mm});
            skLineSegment(sketch, "E343", {"start": v(-0.7, -1.87) * mm, "end": v(-0.74, -1.87) * mm});
            skLineSegment(sketch, "E344", {"start": v(-0.74, -1.83) * mm, "end": v(-0.74, -1.87) * mm});
            skLineSegment(sketch, "E345", {"start": v(-0.7, -1.83) * mm, "end": v(-0.7, -1.87) * mm});
            skLineSegment(sketch, "E346", {"start": v(-0.64, -1.83) * mm, "end": v(-0.68, -1.83) * mm});
            skLineSegment(sketch, "E347", {"start": v(-0.64, -1.87) * mm, "end": v(-0.68, -1.87) * mm});
            skLineSegment(sketch, "E348", {"start": v(-0.68, -1.83) * mm, "end": v(-0.68, -1.87) * mm});
            skLineSegment(sketch, "E349", {"start": v(-0.64, -1.83) * mm, "end": v(-0.64, -1.87) * mm});
            skLineSegment(sketch, "E350", {"start": v(-0.58, -1.83) * mm, "end": v(-0.62, -1.83) * mm});
            skLineSegment(sketch, "E351", {"start": v(-0.58, -1.87) * mm, "end": v(-0.62, -1.87) * mm});
            skLineSegment(sketch, "E352", {"start": v(-0.62, -1.83) * mm, "end": v(-0.62, -1.87) * mm});
            skLineSegment(sketch, "E353", {"start": v(-0.58, -1.83) * mm, "end": v(-0.58, -1.87) * mm});
            skLineSegment(sketch, "E354", {"start": v(-0.52, -1.83) * mm, "end": v(-0.56, -1.83) * mm});
            skLineSegment(sketch, "E355", {"start": v(-0.52, -1.87) * mm, "end": v(-0.56, -1.87) * mm});
            skLineSegment(sketch, "E356", {"start": v(-0.56, -1.83) * mm, "end": v(-0.56, -1.87) * mm});
            skLineSegment(sketch, "E357", {"start": v(-0.52, -1.83) * mm, "end": v(-0.52, -1.87) * mm});
            skLineSegment(sketch, "E358", {"start": v(-0.46, -1.83) * mm, "end": v(-0.5, -1.83) * mm});
            skLineSegment(sketch, "E359", {"start": v(-0.46, -1.87) * mm, "end": v(-0.5, -1.87) * mm});
            skLineSegment(sketch, "E360", {"start": v(-0.5, -1.83) * mm, "end": v(-0.5, -1.87) * mm});
            skLineSegment(sketch, "E361", {"start": v(-0.46, -1.83) * mm, "end": v(-0.46, -1.87) * mm});
            skLineSegment(sketch, "E362", {"start": v(-0.4, -1.83) * mm, "end": v(-0.44, -1.83) * mm});
            skLineSegment(sketch, "E363", {"start": v(-0.4, -1.87) * mm, "end": v(-0.44, -1.87) * mm});
            skLineSegment(sketch, "E364", {"start": v(-0.44, -1.83) * mm, "end": v(-0.44, -1.87) * mm});
            skLineSegment(sketch, "E365", {"start": v(-0.4, -1.83) * mm, "end": v(-0.4, -1.87) * mm});
            skLineSegment(sketch, "E366", {"start": v(-0.01, -1.83) * mm, "end": v(-0.01, -1.87) * mm});
            skLineSegment(sketch, "E367", {"start": v(-0.38, -1.83) * mm, "end": v(-0.38, -1.87) * mm});
            skLineSegment(sketch, "E368", {"start": v(-0.33, -1.83) * mm, "end": v(-0.33, -1.87) * mm});
            skLineSegment(sketch, "E369", {"start": v(-0.3, -1.83) * mm, "end": v(-0.3, -1.87) * mm});
            skLineSegment(sketch, "E370", {"start": v(-0.25, -1.83) * mm, "end": v(-0.25, -1.87) * mm});
            skLineSegment(sketch, "E371", {"start": v(-0.22, -1.83) * mm, "end": v(-0.22, -1.87) * mm});
            skLineSegment(sketch, "E372", {"start": v(-0.15, -1.83) * mm, "end": v(-0.15, -1.87) * mm});
            skLineSegment(sketch, "E373", {"start": v(-0.13, -1.83) * mm, "end": v(-0.13, -1.87) * mm});
            skLineSegment(sketch, "E374", {"start": v(-0.13, -1.83) * mm, "end": v(-0.01, -1.83) * mm});
            skLineSegment(sketch, "E375", {"start": v(-0.13, -1.87) * mm, "end": v(-0.01, -1.87) * mm});
            skLineSegment(sketch, "E376", {"start": v(-0.15, -1.83) * mm, "end": v(-0.22, -1.83) * mm});
            skLineSegment(sketch, "E377", {"start": v(-0.22, -1.87) * mm, "end": v(-0.15, -1.87) * mm});
            skLineSegment(sketch, "E378", {"start": v(-0.25, -1.83) * mm, "end": v(-0.3, -1.83) * mm});
            skLineSegment(sketch, "E379", {"start": v(-0.3, -1.87) * mm, "end": v(-0.25, -1.87) * mm});
            skLineSegment(sketch, "E380", {"start": v(-0.33, -1.83) * mm, "end": v(-0.38, -1.83) * mm});
            skLineSegment(sketch, "E381", {"start": v(-0.38, -1.87) * mm, "end": v(-0.33, -1.87) * mm});
            skLineSegment(sketch, "E382", {"start": v(-0.7, -1.89) * mm, "end": v(-0.74, -1.89) * mm});
            skLineSegment(sketch, "E383", {"start": v(-0.7, -1.93) * mm, "end": v(-0.74, -1.93) * mm});
            skLineSegment(sketch, "E384", {"start": v(-0.74, -1.89) * mm, "end": v(-0.74, -1.93) * mm});
            skLineSegment(sketch, "E385", {"start": v(-0.7, -1.89) * mm, "end": v(-0.7, -1.93) * mm});
            skLineSegment(sketch, "E386", {"start": v(-0.64, -1.89) * mm, "end": v(-0.68, -1.89) * mm});
            skLineSegment(sketch, "E387", {"start": v(-0.64, -1.93) * mm, "end": v(-0.68, -1.93) * mm});
            skLineSegment(sketch, "E388", {"start": v(-0.68, -1.89) * mm, "end": v(-0.68, -1.93) * mm});
            skLineSegment(sketch, "E389", {"start": v(-0.64, -1.89) * mm, "end": v(-0.64, -1.93) * mm});
            skLineSegment(sketch, "E390", {"start": v(-0.58, -1.89) * mm, "end": v(-0.62, -1.89) * mm});
            skLineSegment(sketch, "E391", {"start": v(-0.58, -1.93) * mm, "end": v(-0.62, -1.93) * mm});
            skLineSegment(sketch, "E392", {"start": v(-0.62, -1.89) * mm, "end": v(-0.62, -1.93) * mm});
            skLineSegment(sketch, "E393", {"start": v(-0.58, -1.89) * mm, "end": v(-0.58, -1.93) * mm});
            skLineSegment(sketch, "E394", {"start": v(-0.52, -1.89) * mm, "end": v(-0.56, -1.89) * mm});
            skLineSegment(sketch, "E395", {"start": v(-0.52, -1.93) * mm, "end": v(-0.56, -1.93) * mm});
            skLineSegment(sketch, "E396", {"start": v(-0.56, -1.89) * mm, "end": v(-0.56, -1.93) * mm});
            skLineSegment(sketch, "E397", {"start": v(-0.52, -1.89) * mm, "end": v(-0.52, -1.93) * mm});
            skLineSegment(sketch, "E398", {"start": v(-0.46, -1.89) * mm, "end": v(-0.5, -1.89) * mm});
            skLineSegment(sketch, "E399", {"start": v(-0.46, -1.93) * mm, "end": v(-0.5, -1.93) * mm});
            skLineSegment(sketch, "E400", {"start": v(-0.5, -1.89) * mm, "end": v(-0.5, -1.93) * mm});
            skLineSegment(sketch, "E401", {"start": v(-0.46, -1.89) * mm, "end": v(-0.46, -1.93) * mm});
            skLineSegment(sketch, "E402", {"start": v(-0.4, -1.89) * mm, "end": v(-0.44, -1.89) * mm});
            skLineSegment(sketch, "E403", {"start": v(-0.4, -1.93) * mm, "end": v(-0.44, -1.93) * mm});
            skLineSegment(sketch, "E404", {"start": v(-0.44, -1.89) * mm, "end": v(-0.44, -1.93) * mm});
            skLineSegment(sketch, "E405", {"start": v(-0.4, -1.89) * mm, "end": v(-0.4, -1.93) * mm});
            skLineSegment(sketch, "E406", {"start": v(-0.01, -1.89) * mm, "end": v(-0.01, -1.93) * mm});
            skLineSegment(sketch, "E407", {"start": v(-0.38, -1.89) * mm, "end": v(-0.38, -1.93) * mm});
            skLineSegment(sketch, "E408", {"start": v(-0.33, -1.89) * mm, "end": v(-0.33, -1.93) * mm});
            skLineSegment(sketch, "E409", {"start": v(-0.3, -1.89) * mm, "end": v(-0.3, -1.93) * mm});
            skLineSegment(sketch, "E410", {"start": v(-0.25, -1.89) * mm, "end": v(-0.25, -1.93) * mm});
            skLineSegment(sketch, "E411", {"start": v(-0.22, -1.89) * mm, "end": v(-0.22, -1.93) * mm});
            skLineSegment(sketch, "E412", {"start": v(-0.15, -1.89) * mm, "end": v(-0.15, -1.93) * mm});
            skLineSegment(sketch, "E413", {"start": v(-0.13, -1.89) * mm, "end": v(-0.13, -1.93) * mm});
            skLineSegment(sketch, "E414", {"start": v(-0.13, -1.89) * mm, "end": v(-0.01, -1.89) * mm});
            skLineSegment(sketch, "E415", {"start": v(-0.13, -1.93) * mm, "end": v(-0.01, -1.93) * mm});
            skLineSegment(sketch, "E416", {"start": v(-0.15, -1.89) * mm, "end": v(-0.22, -1.89) * mm});
            skLineSegment(sketch, "E417", {"start": v(-0.22, -1.93) * mm, "end": v(-0.15, -1.93) * mm});
            skLineSegment(sketch, "E418", {"start": v(-0.25, -1.89) * mm, "end": v(-0.3, -1.89) * mm});
            skLineSegment(sketch, "E419", {"start": v(-0.3, -1.93) * mm, "end": v(-0.25, -1.93) * mm});
            skLineSegment(sketch, "E420", {"start": v(-0.33, -1.89) * mm, "end": v(-0.38, -1.89) * mm});
            skLineSegment(sketch, "E421", {"start": v(-0.38, -1.93) * mm, "end": v(-0.33, -1.93) * mm});
            skLineSegment(sketch, "E422", {"start": v(-0.7, -1.95) * mm, "end": v(-0.74, -1.95) * mm});
            skLineSegment(sketch, "E423", {"start": v(-0.7, -1.99) * mm, "end": v(-0.74, -1.99) * mm});
            skLineSegment(sketch, "E424", {"start": v(-0.74, -1.95) * mm, "end": v(-0.74, -1.99) * mm});
            skLineSegment(sketch, "E425", {"start": v(-0.7, -1.95) * mm, "end": v(-0.7, -1.99) * mm});
            skLineSegment(sketch, "E426", {"start": v(-0.64, -1.95) * mm, "end": v(-0.68, -1.95) * mm});
            skLineSegment(sketch, "E427", {"start": v(-0.64, -1.99) * mm, "end": v(-0.68, -1.99) * mm});
            skLineSegment(sketch, "E428", {"start": v(-0.68, -1.95) * mm, "end": v(-0.68, -1.99) * mm});
            skLineSegment(sketch, "E429", {"start": v(-0.64, -1.95) * mm, "end": v(-0.64, -1.99) * mm});
            skLineSegment(sketch, "E430", {"start": v(-0.58, -1.95) * mm, "end": v(-0.62, -1.95) * mm});
            skLineSegment(sketch, "E431", {"start": v(-0.58, -1.99) * mm, "end": v(-0.62, -1.99) * mm});
            skLineSegment(sketch, "E432", {"start": v(-0.62, -1.95) * mm, "end": v(-0.62, -1.99) * mm});
            skLineSegment(sketch, "E433", {"start": v(-0.58, -1.95) * mm, "end": v(-0.58, -1.99) * mm});
            skLineSegment(sketch, "E434", {"start": v(-0.52, -1.95) * mm, "end": v(-0.56, -1.95) * mm});
            skLineSegment(sketch, "E435", {"start": v(-0.52, -1.99) * mm, "end": v(-0.56, -1.99) * mm});
            skLineSegment(sketch, "E436", {"start": v(-0.56, -1.95) * mm, "end": v(-0.56, -1.99) * mm});
            skLineSegment(sketch, "E437", {"start": v(-0.52, -1.95) * mm, "end": v(-0.52, -1.99) * mm});
            skLineSegment(sketch, "E438", {"start": v(-0.46, -1.95) * mm, "end": v(-0.5, -1.95) * mm});
            skLineSegment(sketch, "E439", {"start": v(-0.46, -1.99) * mm, "end": v(-0.5, -1.99) * mm});
            skLineSegment(sketch, "E440", {"start": v(-0.5, -1.95) * mm, "end": v(-0.5, -1.99) * mm});
            skLineSegment(sketch, "E441", {"start": v(-0.46, -1.95) * mm, "end": v(-0.46, -1.99) * mm});
            skLineSegment(sketch, "E442", {"start": v(-0.4, -1.95) * mm, "end": v(-0.44, -1.95) * mm});
            skLineSegment(sketch, "E443", {"start": v(-0.4, -1.99) * mm, "end": v(-0.44, -1.99) * mm});
            skLineSegment(sketch, "E444", {"start": v(-0.44, -1.95) * mm, "end": v(-0.44, -1.99) * mm});
            skLineSegment(sketch, "E445", {"start": v(-0.4, -1.95) * mm, "end": v(-0.4, -1.99) * mm});
            skLineSegment(sketch, "E446", {"start": v(-0.01, -1.95) * mm, "end": v(-0.01, -1.99) * mm});
            skLineSegment(sketch, "E447", {"start": v(-0.38, -1.95) * mm, "end": v(-0.38, -1.99) * mm});
            skLineSegment(sketch, "E448", {"start": v(-0.33, -1.95) * mm, "end": v(-0.33, -1.99) * mm});
            skLineSegment(sketch, "E449", {"start": v(-0.3, -1.95) * mm, "end": v(-0.3, -1.99) * mm});
            skLineSegment(sketch, "E450", {"start": v(-0.25, -1.95) * mm, "end": v(-0.25, -1.99) * mm});
            skLineSegment(sketch, "E451", {"start": v(-0.22, -1.95) * mm, "end": v(-0.22, -1.99) * mm});
            skLineSegment(sketch, "E452", {"start": v(-0.15, -1.95) * mm, "end": v(-0.15, -1.99) * mm});
            skLineSegment(sketch, "E453", {"start": v(-0.13, -1.95) * mm, "end": v(-0.13, -1.99) * mm});
            skLineSegment(sketch, "E454", {"start": v(-0.13, -1.95) * mm, "end": v(-0.01, -1.95) * mm});
            skLineSegment(sketch, "E455", {"start": v(-0.13, -1.99) * mm, "end": v(-0.01, -1.99) * mm});
            skLineSegment(sketch, "E456", {"start": v(-0.15, -1.95) * mm, "end": v(-0.22, -1.95) * mm});
            skLineSegment(sketch, "E457", {"start": v(-0.22, -1.99) * mm, "end": v(-0.15, -1.99) * mm});
            skLineSegment(sketch, "E458", {"start": v(-0.25, -1.95) * mm, "end": v(-0.3, -1.95) * mm});
            skLineSegment(sketch, "E459", {"start": v(-0.3, -1.99) * mm, "end": v(-0.25, -1.99) * mm});
            skLineSegment(sketch, "E460", {"start": v(-0.33, -1.95) * mm, "end": v(-0.38, -1.95) * mm});
            skLineSegment(sketch, "E461", {"start": v(-0.38, -1.99) * mm, "end": v(-0.33, -1.99) * mm});
            skLineSegment(sketch, "E462", {"start": v(-0.7, -2) * mm, "end": v(-0.74, -2) * mm});
            skLineSegment(sketch, "E463", {"start": v(-0.7, -2.05) * mm, "end": v(-0.74, -2.05) * mm});
            skLineSegment(sketch, "E464", {"start": v(-0.74, -2) * mm, "end": v(-0.74, -2.05) * mm});
            skLineSegment(sketch, "E465", {"start": v(-0.7, -2) * mm, "end": v(-0.7, -2.05) * mm});
            skLineSegment(sketch, "E466", {"start": v(-0.64, -2) * mm, "end": v(-0.68, -2) * mm});
            skLineSegment(sketch, "E467", {"start": v(-0.64, -2.05) * mm, "end": v(-0.68, -2.05) * mm});
            skLineSegment(sketch, "E468", {"start": v(-0.68, -2) * mm, "end": v(-0.68, -2.05) * mm});
            skLineSegment(sketch, "E469", {"start": v(-0.64, -2) * mm, "end": v(-0.64, -2.05) * mm});
            skLineSegment(sketch, "E470", {"start": v(-0.58, -2) * mm, "end": v(-0.62, -2) * mm});
            skLineSegment(sketch, "E471", {"start": v(-0.58, -2.05) * mm, "end": v(-0.62, -2.05) * mm});
            skLineSegment(sketch, "E472", {"start": v(-0.62, -2) * mm, "end": v(-0.62, -2.05) * mm});
            skLineSegment(sketch, "E473", {"start": v(-0.58, -2) * mm, "end": v(-0.58, -2.05) * mm});
            skLineSegment(sketch, "E474", {"start": v(-0.52, -2) * mm, "end": v(-0.56, -2) * mm});
            skLineSegment(sketch, "E475", {"start": v(-0.52, -2.05) * mm, "end": v(-0.56, -2.05) * mm});
            skLineSegment(sketch, "E476", {"start": v(-0.56, -2) * mm, "end": v(-0.56, -2.05) * mm});
            skLineSegment(sketch, "E477", {"start": v(-0.52, -2) * mm, "end": v(-0.52, -2.05) * mm});
            skLineSegment(sketch, "E478", {"start": v(-0.46, -2) * mm, "end": v(-0.5, -2) * mm});
            skLineSegment(sketch, "E479", {"start": v(-0.46, -2.05) * mm, "end": v(-0.5, -2.05) * mm});
            skLineSegment(sketch, "E480", {"start": v(-0.5, -2) * mm, "end": v(-0.5, -2.05) * mm});
            skLineSegment(sketch, "E481", {"start": v(-0.46, -2) * mm, "end": v(-0.46, -2.05) * mm});
            skLineSegment(sketch, "E482", {"start": v(-0.4, -2) * mm, "end": v(-0.44, -2) * mm});
            skLineSegment(sketch, "E483", {"start": v(-0.4, -2.05) * mm, "end": v(-0.44, -2.05) * mm});
            skLineSegment(sketch, "E484", {"start": v(-0.44, -2) * mm, "end": v(-0.44, -2.05) * mm});
            skLineSegment(sketch, "E485", {"start": v(-0.4, -2) * mm, "end": v(-0.4, -2.05) * mm});
            skLineSegment(sketch, "E486", {"start": v(-0.01, -2) * mm, "end": v(-0.01, -2.05) * mm});
            skLineSegment(sketch, "E487", {"start": v(-0.38, -2) * mm, "end": v(-0.38, -2.05) * mm});
            skLineSegment(sketch, "E488", {"start": v(-0.33, -2) * mm, "end": v(-0.33, -2.05) * mm});
            skLineSegment(sketch, "E489", {"start": v(-0.3, -2) * mm, "end": v(-0.3, -2.05) * mm});
            skLineSegment(sketch, "E490", {"start": v(-0.25, -2) * mm, "end": v(-0.25, -2.05) * mm});
            skLineSegment(sketch, "E491", {"start": v(-0.22, -2) * mm, "end": v(-0.22, -2.05) * mm});
            skLineSegment(sketch, "E492", {"start": v(-0.15, -2) * mm, "end": v(-0.15, -2.05) * mm});
            skLineSegment(sketch, "E493", {"start": v(-0.13, -2) * mm, "end": v(-0.13, -2.05) * mm});
            skLineSegment(sketch, "E494", {"start": v(-0.13, -2) * mm, "end": v(-0.01, -2) * mm});
            skLineSegment(sketch, "E495", {"start": v(-0.13, -2.05) * mm, "end": v(-0.01, -2.05) * mm});
            skLineSegment(sketch, "E496", {"start": v(-0.15, -2) * mm, "end": v(-0.22, -2) * mm});
            skLineSegment(sketch, "E497", {"start": v(-0.22, -2.05) * mm, "end": v(-0.15, -2.05) * mm});
            skLineSegment(sketch, "E498", {"start": v(-0.25, -2) * mm, "end": v(-0.3, -2) * mm});
            skLineSegment(sketch, "E499", {"start": v(-0.3, -2.05) * mm, "end": v(-0.25, -2.05) * mm});
            skLineSegment(sketch, "E500", {"start": v(-0.33, -2) * mm, "end": v(-0.38, -2) * mm});
            skLineSegment(sketch, "E501", {"start": v(-0.38, -2.05) * mm, "end": v(-0.33, -2.05) * mm});
            skLineSegment(sketch, "E502", {"start": v(-0.7, -2.07) * mm, "end": v(-0.74, -2.07) * mm});
            skLineSegment(sketch, "E503", {"start": v(-0.7, -2.1) * mm, "end": v(-0.74, -2.1) * mm});
            skLineSegment(sketch, "E504", {"start": v(-0.74, -2.07) * mm, "end": v(-0.74, -2.1) * mm});
            skLineSegment(sketch, "E505", {"start": v(-0.7, -2.07) * mm, "end": v(-0.7, -2.1) * mm});
            skLineSegment(sketch, "E506", {"start": v(-0.64, -2.07) * mm, "end": v(-0.68, -2.07) * mm});
            skLineSegment(sketch, "E507", {"start": v(-0.64, -2.1) * mm, "end": v(-0.68, -2.1) * mm});
            skLineSegment(sketch, "E508", {"start": v(-0.68, -2.07) * mm, "end": v(-0.68, -2.1) * mm});
            skLineSegment(sketch, "E509", {"start": v(-0.64, -2.07) * mm, "end": v(-0.64, -2.1) * mm});
            skLineSegment(sketch, "E510", {"start": v(-0.58, -2.07) * mm, "end": v(-0.62, -2.07) * mm});
            skLineSegment(sketch, "E511", {"start": v(-0.58, -2.1) * mm, "end": v(-0.62, -2.1) * mm});
            skLineSegment(sketch, "E512", {"start": v(-0.62, -2.07) * mm, "end": v(-0.62, -2.1) * mm});
            skLineSegment(sketch, "E513", {"start": v(-0.58, -2.07) * mm, "end": v(-0.58, -2.1) * mm});
            skLineSegment(sketch, "E514", {"start": v(-0.52, -2.07) * mm, "end": v(-0.56, -2.07) * mm});
            skLineSegment(sketch, "E515", {"start": v(-0.52, -2.1) * mm, "end": v(-0.56, -2.1) * mm});
            skLineSegment(sketch, "E516", {"start": v(-0.56, -2.07) * mm, "end": v(-0.56, -2.1) * mm});
            skLineSegment(sketch, "E517", {"start": v(-0.52, -2.07) * mm, "end": v(-0.52, -2.1) * mm});
            skLineSegment(sketch, "E518", {"start": v(-0.46, -2.07) * mm, "end": v(-0.5, -2.07) * mm});
            skLineSegment(sketch, "E519", {"start": v(-0.46, -2.1) * mm, "end": v(-0.5, -2.1) * mm});
            skLineSegment(sketch, "E520", {"start": v(-0.5, -2.07) * mm, "end": v(-0.5, -2.1) * mm});
            skLineSegment(sketch, "E521", {"start": v(-0.46, -2.07) * mm, "end": v(-0.46, -2.1) * mm});
            skLineSegment(sketch, "E522", {"start": v(-0.4, -2.07) * mm, "end": v(-0.44, -2.07) * mm});
            skLineSegment(sketch, "E523", {"start": v(-0.4, -2.1) * mm, "end": v(-0.44, -2.1) * mm});
            skLineSegment(sketch, "E524", {"start": v(-0.44, -2.07) * mm, "end": v(-0.44, -2.1) * mm});
            skLineSegment(sketch, "E525", {"start": v(-0.4, -2.07) * mm, "end": v(-0.4, -2.1) * mm});
            skLineSegment(sketch, "E526", {"start": v(-0.01, -2.07) * mm, "end": v(-0.01, -2.1) * mm});
            skLineSegment(sketch, "E527", {"start": v(-0.38, -2.07) * mm, "end": v(-0.38, -2.1) * mm});
            skLineSegment(sketch, "E528", {"start": v(-0.33, -2.07) * mm, "end": v(-0.33, -2.1) * mm});
            skLineSegment(sketch, "E529", {"start": v(-0.3, -2.07) * mm, "end": v(-0.3, -2.1) * mm});
            skLineSegment(sketch, "E530", {"start": v(-0.25, -2.07) * mm, "end": v(-0.25, -2.1) * mm});
            skLineSegment(sketch, "E531", {"start": v(-0.22, -2.07) * mm, "end": v(-0.22, -2.1) * mm});
            skLineSegment(sketch, "E532", {"start": v(-0.15, -2.07) * mm, "end": v(-0.15, -2.1) * mm});
            skLineSegment(sketch, "E533", {"start": v(-0.13, -2.07) * mm, "end": v(-0.13, -2.1) * mm});
            skLineSegment(sketch, "E534", {"start": v(-0.13, -2.07) * mm, "end": v(-0.01, -2.07) * mm});
            skLineSegment(sketch, "E535", {"start": v(-0.13, -2.1) * mm, "end": v(-0.01, -2.1) * mm});
            skLineSegment(sketch, "E536", {"start": v(-0.15, -2.07) * mm, "end": v(-0.22, -2.07) * mm});
            skLineSegment(sketch, "E537", {"start": v(-0.22, -2.1) * mm, "end": v(-0.15, -2.1) * mm});
            skLineSegment(sketch, "E538", {"start": v(-0.25, -2.07) * mm, "end": v(-0.3, -2.07) * mm});
            skLineSegment(sketch, "E539", {"start": v(-0.3, -2.1) * mm, "end": v(-0.25, -2.1) * mm});
            skLineSegment(sketch, "E540", {"start": v(-0.33, -2.07) * mm, "end": v(-0.38, -2.07) * mm});
            skLineSegment(sketch, "E541", {"start": v(-0.38, -2.1) * mm, "end": v(-0.33, -2.1) * mm});
            skLineSegment(sketch, "E542", {"start": v(-0.7, -2.13) * mm, "end": v(-0.74, -2.13) * mm});
            skLineSegment(sketch, "E543", {"start": v(-0.7, -2.17) * mm, "end": v(-0.74, -2.17) * mm});
            skLineSegment(sketch, "E544", {"start": v(-0.74, -2.13) * mm, "end": v(-0.74, -2.17) * mm});
            skLineSegment(sketch, "E545", {"start": v(-0.7, -2.13) * mm, "end": v(-0.7, -2.17) * mm});
            skLineSegment(sketch, "E546", {"start": v(-0.64, -2.13) * mm, "end": v(-0.68, -2.13) * mm});
            skLineSegment(sketch, "E547", {"start": v(-0.64, -2.17) * mm, "end": v(-0.68, -2.17) * mm});
            skLineSegment(sketch, "E548", {"start": v(-0.68, -2.13) * mm, "end": v(-0.68, -2.17) * mm});
            skLineSegment(sketch, "E549", {"start": v(-0.64, -2.13) * mm, "end": v(-0.64, -2.17) * mm});
            skLineSegment(sketch, "E550", {"start": v(-0.58, -2.13) * mm, "end": v(-0.62, -2.13) * mm});
            skLineSegment(sketch, "E551", {"start": v(-0.58, -2.17) * mm, "end": v(-0.62, -2.17) * mm});
            skLineSegment(sketch, "E552", {"start": v(-0.62, -2.13) * mm, "end": v(-0.62, -2.17) * mm});
            skLineSegment(sketch, "E553", {"start": v(-0.58, -2.13) * mm, "end": v(-0.58, -2.17) * mm});
            skLineSegment(sketch, "E554", {"start": v(-0.52, -2.13) * mm, "end": v(-0.56, -2.13) * mm});
            skLineSegment(sketch, "E555", {"start": v(-0.52, -2.17) * mm, "end": v(-0.56, -2.17) * mm});
            skLineSegment(sketch, "E556", {"start": v(-0.56, -2.13) * mm, "end": v(-0.56, -2.17) * mm});
            skLineSegment(sketch, "E557", {"start": v(-0.52, -2.13) * mm, "end": v(-0.52, -2.17) * mm});
            skLineSegment(sketch, "E558", {"start": v(-0.46, -2.13) * mm, "end": v(-0.5, -2.13) * mm});
            skLineSegment(sketch, "E559", {"start": v(-0.46, -2.17) * mm, "end": v(-0.5, -2.17) * mm});
            skLineSegment(sketch, "E560", {"start": v(-0.5, -2.13) * mm, "end": v(-0.5, -2.17) * mm});
            skLineSegment(sketch, "E561", {"start": v(-0.46, -2.13) * mm, "end": v(-0.46, -2.17) * mm});
            skLineSegment(sketch, "E562", {"start": v(-0.4, -2.13) * mm, "end": v(-0.44, -2.13) * mm});
            skLineSegment(sketch, "E563", {"start": v(-0.4, -2.17) * mm, "end": v(-0.44, -2.17) * mm});
            skLineSegment(sketch, "E564", {"start": v(-0.44, -2.13) * mm, "end": v(-0.44, -2.17) * mm});
            skLineSegment(sketch, "E565", {"start": v(-0.4, -2.13) * mm, "end": v(-0.4, -2.17) * mm});
            skLineSegment(sketch, "E566", {"start": v(-0.01, -2.13) * mm, "end": v(-0.01, -2.17) * mm});
            skLineSegment(sketch, "E567", {"start": v(-0.38, -2.13) * mm, "end": v(-0.38, -2.17) * mm});
            skLineSegment(sketch, "E568", {"start": v(-0.33, -2.13) * mm, "end": v(-0.33, -2.17) * mm});
            skLineSegment(sketch, "E569", {"start": v(-0.3, -2.13) * mm, "end": v(-0.3, -2.17) * mm});
            skLineSegment(sketch, "E570", {"start": v(-0.25, -2.13) * mm, "end": v(-0.25, -2.17) * mm});
            skLineSegment(sketch, "E571", {"start": v(-0.22, -2.13) * mm, "end": v(-0.22, -2.17) * mm});
            skLineSegment(sketch, "E572", {"start": v(-0.15, -2.13) * mm, "end": v(-0.15, -2.17) * mm});
            skLineSegment(sketch, "E573", {"start": v(-0.13, -2.13) * mm, "end": v(-0.13, -2.17) * mm});
            skLineSegment(sketch, "E574", {"start": v(-0.13, -2.13) * mm, "end": v(-0.01, -2.13) * mm});
            skLineSegment(sketch, "E575", {"start": v(-0.13, -2.17) * mm, "end": v(-0.01, -2.17) * mm});
            skLineSegment(sketch, "E576", {"start": v(-0.15, -2.13) * mm, "end": v(-0.22, -2.13) * mm});
            skLineSegment(sketch, "E577", {"start": v(-0.22, -2.17) * mm, "end": v(-0.15, -2.17) * mm});
            skLineSegment(sketch, "E578", {"start": v(-0.25, -2.13) * mm, "end": v(-0.3, -2.13) * mm});
            skLineSegment(sketch, "E579", {"start": v(-0.3, -2.17) * mm, "end": v(-0.25, -2.17) * mm});
            skLineSegment(sketch, "E580", {"start": v(-0.33, -2.13) * mm, "end": v(-0.38, -2.13) * mm});
            skLineSegment(sketch, "E581", {"start": v(-0.38, -2.17) * mm, "end": v(-0.33, -2.17) * mm});
            skLineSegment(sketch, "E582", {"start": v(-0.7, -2.19) * mm, "end": v(-0.74, -2.19) * mm});
            skLineSegment(sketch, "E583", {"start": v(-0.7, -2.23) * mm, "end": v(-0.74, -2.23) * mm});
            skLineSegment(sketch, "E584", {"start": v(-0.74, -2.19) * mm, "end": v(-0.74, -2.23) * mm});
            skLineSegment(sketch, "E585", {"start": v(-0.7, -2.19) * mm, "end": v(-0.7, -2.23) * mm});
            skLineSegment(sketch, "E586", {"start": v(-0.64, -2.19) * mm, "end": v(-0.68, -2.19) * mm});
            skLineSegment(sketch, "E587", {"start": v(-0.64, -2.23) * mm, "end": v(-0.68, -2.23) * mm});
            skLineSegment(sketch, "E588", {"start": v(-0.68, -2.19) * mm, "end": v(-0.68, -2.23) * mm});
            skLineSegment(sketch, "E589", {"start": v(-0.64, -2.19) * mm, "end": v(-0.64, -2.23) * mm});
            skLineSegment(sketch, "E590", {"start": v(-0.58, -2.19) * mm, "end": v(-0.62, -2.19) * mm});
            skLineSegment(sketch, "E591", {"start": v(-0.58, -2.23) * mm, "end": v(-0.62, -2.23) * mm});
            skLineSegment(sketch, "E592", {"start": v(-0.62, -2.19) * mm, "end": v(-0.62, -2.23) * mm});
            skLineSegment(sketch, "E593", {"start": v(-0.58, -2.19) * mm, "end": v(-0.58, -2.23) * mm});
            skLineSegment(sketch, "E594", {"start": v(-0.52, -2.19) * mm, "end": v(-0.56, -2.19) * mm});
            skLineSegment(sketch, "E595", {"start": v(-0.52, -2.23) * mm, "end": v(-0.56, -2.23) * mm});
            skLineSegment(sketch, "E596", {"start": v(-0.56, -2.19) * mm, "end": v(-0.56, -2.23) * mm});
            skLineSegment(sketch, "E597", {"start": v(-0.52, -2.19) * mm, "end": v(-0.52, -2.23) * mm});
            skLineSegment(sketch, "E598", {"start": v(-0.46, -2.19) * mm, "end": v(-0.5, -2.19) * mm});
            skLineSegment(sketch, "E599", {"start": v(-0.46, -2.23) * mm, "end": v(-0.5, -2.23) * mm});
            skLineSegment(sketch, "E600", {"start": v(-0.5, -2.19) * mm, "end": v(-0.5, -2.23) * mm});
            skLineSegment(sketch, "E601", {"start": v(-0.46, -2.19) * mm, "end": v(-0.46, -2.23) * mm});
            skLineSegment(sketch, "E602", {"start": v(-0.4, -2.19) * mm, "end": v(-0.44, -2.19) * mm});
            skLineSegment(sketch, "E603", {"start": v(-0.4, -2.23) * mm, "end": v(-0.44, -2.23) * mm});
            skLineSegment(sketch, "E604", {"start": v(-0.44, -2.19) * mm, "end": v(-0.44, -2.23) * mm});
            skLineSegment(sketch, "E605", {"start": v(-0.4, -2.19) * mm, "end": v(-0.4, -2.23) * mm});
            skLineSegment(sketch, "E606", {"start": v(-0.01, -2.19) * mm, "end": v(-0.01, -2.23) * mm});
            skLineSegment(sketch, "E607", {"start": v(-0.38, -2.19) * mm, "end": v(-0.38, -2.23) * mm});
            skLineSegment(sketch, "E608", {"start": v(-0.33, -2.19) * mm, "end": v(-0.33, -2.23) * mm});
            skLineSegment(sketch, "E609", {"start": v(-0.3, -2.19) * mm, "end": v(-0.3, -2.23) * mm});
            skLineSegment(sketch, "E610", {"start": v(-0.25, -2.19) * mm, "end": v(-0.25, -2.23) * mm});
            skLineSegment(sketch, "E611", {"start": v(-0.22, -2.19) * mm, "end": v(-0.22, -2.23) * mm});
            skLineSegment(sketch, "E612", {"start": v(-0.15, -2.19) * mm, "end": v(-0.15, -2.23) * mm});
            skLineSegment(sketch, "E613", {"start": v(-0.13, -2.19) * mm, "end": v(-0.13, -2.23) * mm});
            skLineSegment(sketch, "E614", {"start": v(-0.13, -2.19) * mm, "end": v(-0.01, -2.19) * mm});
            skLineSegment(sketch, "E615", {"start": v(-0.13, -2.23) * mm, "end": v(-0.01, -2.23) * mm});
            skLineSegment(sketch, "E616", {"start": v(-0.15, -2.19) * mm, "end": v(-0.22, -2.19) * mm});
            skLineSegment(sketch, "E617", {"start": v(-0.22, -2.23) * mm, "end": v(-0.15, -2.23) * mm});
            skLineSegment(sketch, "E618", {"start": v(-0.25, -2.19) * mm, "end": v(-0.3, -2.19) * mm});
            skLineSegment(sketch, "E619", {"start": v(-0.3, -2.23) * mm, "end": v(-0.25, -2.23) * mm});
            skLineSegment(sketch, "E620", {"start": v(-0.33, -2.19) * mm, "end": v(-0.38, -2.19) * mm});
            skLineSegment(sketch, "E621", {"start": v(-0.38, -2.23) * mm, "end": v(-0.33, -2.23) * mm});
            skLineSegment(sketch, "E622", {"start": v(-0.7, -2.25) * mm, "end": v(-0.74, -2.25) * mm});
            skLineSegment(sketch, "E623", {"start": v(-0.7, -2.29) * mm, "end": v(-0.74, -2.29) * mm});
            skLineSegment(sketch, "E624", {"start": v(-0.74, -2.25) * mm, "end": v(-0.74, -2.29) * mm});
            skLineSegment(sketch, "E625", {"start": v(-0.7, -2.25) * mm, "end": v(-0.7, -2.29) * mm});
            skLineSegment(sketch, "E626", {"start": v(-0.64, -2.25) * mm, "end": v(-0.68, -2.25) * mm});
            skLineSegment(sketch, "E627", {"start": v(-0.64, -2.29) * mm, "end": v(-0.68, -2.29) * mm});
            skLineSegment(sketch, "E628", {"start": v(-0.68, -2.25) * mm, "end": v(-0.68, -2.29) * mm});
            skLineSegment(sketch, "E629", {"start": v(-0.64, -2.25) * mm, "end": v(-0.64, -2.29) * mm});
            skLineSegment(sketch, "E630", {"start": v(-0.58, -2.25) * mm, "end": v(-0.62, -2.25) * mm});
            skLineSegment(sketch, "E631", {"start": v(-0.58, -2.29) * mm, "end": v(-0.62, -2.29) * mm});
            skLineSegment(sketch, "E632", {"start": v(-0.62, -2.25) * mm, "end": v(-0.62, -2.29) * mm});
            skLineSegment(sketch, "E633", {"start": v(-0.58, -2.25) * mm, "end": v(-0.58, -2.29) * mm});
            skLineSegment(sketch, "E634", {"start": v(-0.52, -2.25) * mm, "end": v(-0.56, -2.25) * mm});
            skLineSegment(sketch, "E635", {"start": v(-0.52, -2.29) * mm, "end": v(-0.56, -2.29) * mm});
            skLineSegment(sketch, "E636", {"start": v(-0.56, -2.25) * mm, "end": v(-0.56, -2.29) * mm});
            skLineSegment(sketch, "E637", {"start": v(-0.52, -2.25) * mm, "end": v(-0.52, -2.29) * mm});
            skLineSegment(sketch, "E638", {"start": v(-0.46, -2.25) * mm, "end": v(-0.5, -2.25) * mm});
            skLineSegment(sketch, "E639", {"start": v(-0.46, -2.29) * mm, "end": v(-0.5, -2.29) * mm});
            skLineSegment(sketch, "E640", {"start": v(-0.5, -2.25) * mm, "end": v(-0.5, -2.29) * mm});
            skLineSegment(sketch, "E641", {"start": v(-0.46, -2.25) * mm, "end": v(-0.46, -2.29) * mm});
            skLineSegment(sketch, "E642", {"start": v(-0.4, -2.25) * mm, "end": v(-0.44, -2.25) * mm});
            skLineSegment(sketch, "E643", {"start": v(-0.4, -2.29) * mm, "end": v(-0.44, -2.29) * mm});
            skLineSegment(sketch, "E644", {"start": v(-0.44, -2.25) * mm, "end": v(-0.44, -2.29) * mm});
            skLineSegment(sketch, "E645", {"start": v(-0.4, -2.25) * mm, "end": v(-0.4, -2.29) * mm});
            skLineSegment(sketch, "E646", {"start": v(-0.01, -2.25) * mm, "end": v(-0.01, -2.29) * mm});
            skLineSegment(sketch, "E647", {"start": v(-0.38, -2.25) * mm, "end": v(-0.38, -2.29) * mm});
            skLineSegment(sketch, "E648", {"start": v(-0.33, -2.25) * mm, "end": v(-0.33, -2.29) * mm});
            skLineSegment(sketch, "E649", {"start": v(-0.3, -2.25) * mm, "end": v(-0.3, -2.29) * mm});
            skLineSegment(sketch, "E650", {"start": v(-0.25, -2.25) * mm, "end": v(-0.25, -2.29) * mm});
            skLineSegment(sketch, "E651", {"start": v(-0.22, -2.25) * mm, "end": v(-0.22, -2.29) * mm});
            skLineSegment(sketch, "E652", {"start": v(-0.15, -2.25) * mm, "end": v(-0.15, -2.29) * mm});
            skLineSegment(sketch, "E653", {"start": v(-0.13, -2.25) * mm, "end": v(-0.13, -2.29) * mm});
            skLineSegment(sketch, "E654", {"start": v(-0.13, -2.25) * mm, "end": v(-0.01, -2.25) * mm});
            skLineSegment(sketch, "E655", {"start": v(-0.13, -2.29) * mm, "end": v(-0.01, -2.29) * mm});
            skLineSegment(sketch, "E656", {"start": v(-0.15, -2.25) * mm, "end": v(-0.22, -2.25) * mm});
            skLineSegment(sketch, "E657", {"start": v(-0.22, -2.29) * mm, "end": v(-0.15, -2.29) * mm});
            skLineSegment(sketch, "E658", {"start": v(-0.25, -2.25) * mm, "end": v(-0.3, -2.25) * mm});
            skLineSegment(sketch, "E659", {"start": v(-0.3, -2.29) * mm, "end": v(-0.25, -2.29) * mm});
            skLineSegment(sketch, "E660", {"start": v(-0.33, -2.25) * mm, "end": v(-0.38, -2.25) * mm});
            skLineSegment(sketch, "E661", {"start": v(-0.38, -2.29) * mm, "end": v(-0.33, -2.29) * mm});
            skLineSegment(sketch, "E662", {"start": v(-0.7, -2.3) * mm, "end": v(-0.74, -2.3) * mm});
            skLineSegment(sketch, "E663", {"start": v(-0.7, -2.35) * mm, "end": v(-0.74, -2.35) * mm});
            skLineSegment(sketch, "E664", {"start": v(-0.74, -2.3) * mm, "end": v(-0.74, -2.35) * mm});
            skLineSegment(sketch, "E665", {"start": v(-0.7, -2.3) * mm, "end": v(-0.7, -2.35) * mm});
            skLineSegment(sketch, "E666", {"start": v(-0.64, -2.3) * mm, "end": v(-0.68, -2.3) * mm});
            skLineSegment(sketch, "E667", {"start": v(-0.64, -2.35) * mm, "end": v(-0.68, -2.35) * mm});
            skLineSegment(sketch, "E668", {"start": v(-0.68, -2.3) * mm, "end": v(-0.68, -2.35) * mm});
            skLineSegment(sketch, "E669", {"start": v(-0.64, -2.3) * mm, "end": v(-0.64, -2.35) * mm});
            skLineSegment(sketch, "E670", {"start": v(-0.58, -2.3) * mm, "end": v(-0.62, -2.3) * mm});
            skLineSegment(sketch, "E671", {"start": v(-0.58, -2.35) * mm, "end": v(-0.62, -2.35) * mm});
            skLineSegment(sketch, "E672", {"start": v(-0.62, -2.3) * mm, "end": v(-0.62, -2.35) * mm});
            skLineSegment(sketch, "E673", {"start": v(-0.58, -2.3) * mm, "end": v(-0.58, -2.35) * mm});
            skLineSegment(sketch, "E674", {"start": v(-0.52, -2.3) * mm, "end": v(-0.56, -2.3) * mm});
            skLineSegment(sketch, "E675", {"start": v(-0.52, -2.35) * mm, "end": v(-0.56, -2.35) * mm});
            skLineSegment(sketch, "E676", {"start": v(-0.56, -2.3) * mm, "end": v(-0.56, -2.35) * mm});
            skLineSegment(sketch, "E677", {"start": v(-0.52, -2.3) * mm, "end": v(-0.52, -2.35) * mm});
            skLineSegment(sketch, "E678", {"start": v(-0.46, -2.3) * mm, "end": v(-0.5, -2.3) * mm});
            skLineSegment(sketch, "E679", {"start": v(-0.46, -2.35) * mm, "end": v(-0.5, -2.35) * mm});
            skLineSegment(sketch, "E680", {"start": v(-0.5, -2.3) * mm, "end": v(-0.5, -2.35) * mm});
            skLineSegment(sketch, "E681", {"start": v(-0.46, -2.3) * mm, "end": v(-0.46, -2.35) * mm});
            skLineSegment(sketch, "E682", {"start": v(-0.4, -2.3) * mm, "end": v(-0.44, -2.3) * mm});
            skLineSegment(sketch, "E683", {"start": v(-0.4, -2.35) * mm, "end": v(-0.44, -2.35) * mm});
            skLineSegment(sketch, "E684", {"start": v(-0.44, -2.3) * mm, "end": v(-0.44, -2.35) * mm});
            skLineSegment(sketch, "E685", {"start": v(-0.4, -2.3) * mm, "end": v(-0.4, -2.35) * mm});
            skLineSegment(sketch, "E686", {"start": v(-0.01, -2.3) * mm, "end": v(-0.01, -2.35) * mm});
            skLineSegment(sketch, "E687", {"start": v(-0.38, -2.3) * mm, "end": v(-0.38, -2.35) * mm});
            skLineSegment(sketch, "E688", {"start": v(-0.33, -2.3) * mm, "end": v(-0.33, -2.35) * mm});
            skLineSegment(sketch, "E689", {"start": v(-0.3, -2.3) * mm, "end": v(-0.3, -2.35) * mm});
            skLineSegment(sketch, "E690", {"start": v(-0.25, -2.3) * mm, "end": v(-0.25, -2.35) * mm});
            skLineSegment(sketch, "E691", {"start": v(-0.22, -2.3) * mm, "end": v(-0.22, -2.35) * mm});
            skLineSegment(sketch, "E692", {"start": v(-0.15, -2.3) * mm, "end": v(-0.15, -2.35) * mm});
            skLineSegment(sketch, "E693", {"start": v(-0.13, -2.3) * mm, "end": v(-0.13, -2.35) * mm});
            skLineSegment(sketch, "E694", {"start": v(-0.13, -2.3) * mm, "end": v(-0.01, -2.3) * mm});
            skLineSegment(sketch, "E695", {"start": v(-0.13, -2.35) * mm, "end": v(-0.01, -2.35) * mm});
            skLineSegment(sketch, "E696", {"start": v(-0.15, -2.3) * mm, "end": v(-0.22, -2.3) * mm});
            skLineSegment(sketch, "E697", {"start": v(-0.22, -2.35) * mm, "end": v(-0.15, -2.35) * mm});
            skLineSegment(sketch, "E698", {"start": v(-0.25, -2.3) * mm, "end": v(-0.3, -2.3) * mm});
            skLineSegment(sketch, "E699", {"start": v(-0.3, -2.35) * mm, "end": v(-0.25, -2.35) * mm});
            skLineSegment(sketch, "E700", {"start": v(-0.33, -2.3) * mm, "end": v(-0.38, -2.3) * mm});
            skLineSegment(sketch, "E701", {"start": v(-0.38, -2.35) * mm, "end": v(-0.33, -2.35) * mm});
            skLineSegment(sketch, "E702", {"start": v(-0.7, -2.37) * mm, "end": v(-0.74, -2.37) * mm});
            skLineSegment(sketch, "E703", {"start": v(-0.7, -2.4) * mm, "end": v(-0.74, -2.4) * mm});
            skLineSegment(sketch, "E704", {"start": v(-0.74, -2.37) * mm, "end": v(-0.74, -2.4) * mm});
            skLineSegment(sketch, "E705", {"start": v(-0.7, -2.37) * mm, "end": v(-0.7, -2.4) * mm});
            skLineSegment(sketch, "E706", {"start": v(-0.64, -2.37) * mm, "end": v(-0.68, -2.37) * mm});
            skLineSegment(sketch, "E707", {"start": v(-0.64, -2.4) * mm, "end": v(-0.68, -2.4) * mm});
            skLineSegment(sketch, "E708", {"start": v(-0.68, -2.37) * mm, "end": v(-0.68, -2.4) * mm});
            skLineSegment(sketch, "E709", {"start": v(-0.64, -2.37) * mm, "end": v(-0.64, -2.4) * mm});
            skLineSegment(sketch, "E710", {"start": v(-0.58, -2.37) * mm, "end": v(-0.62, -2.37) * mm});
            skLineSegment(sketch, "E711", {"start": v(-0.58, -2.4) * mm, "end": v(-0.62, -2.4) * mm});
            skLineSegment(sketch, "E712", {"start": v(-0.62, -2.37) * mm, "end": v(-0.62, -2.4) * mm});
            skLineSegment(sketch, "E713", {"start": v(-0.58, -2.37) * mm, "end": v(-0.58, -2.4) * mm});
            skLineSegment(sketch, "E714", {"start": v(-0.52, -2.37) * mm, "end": v(-0.56, -2.37) * mm});
            skLineSegment(sketch, "E715", {"start": v(-0.52, -2.4) * mm, "end": v(-0.56, -2.4) * mm});
            skLineSegment(sketch, "E716", {"start": v(-0.56, -2.37) * mm, "end": v(-0.56, -2.4) * mm});
            skLineSegment(sketch, "E717", {"start": v(-0.52, -2.37) * mm, "end": v(-0.52, -2.4) * mm});
            skLineSegment(sketch, "E718", {"start": v(-0.46, -2.37) * mm, "end": v(-0.5, -2.37) * mm});
            skLineSegment(sketch, "E719", {"start": v(-0.46, -2.4) * mm, "end": v(-0.5, -2.4) * mm});
            skLineSegment(sketch, "E720", {"start": v(-0.5, -2.37) * mm, "end": v(-0.5, -2.4) * mm});
            skLineSegment(sketch, "E721", {"start": v(-0.46, -2.37) * mm, "end": v(-0.46, -2.4) * mm});
            skLineSegment(sketch, "E722", {"start": v(-0.4, -2.37) * mm, "end": v(-0.44, -2.37) * mm});
            skLineSegment(sketch, "E723", {"start": v(-0.4, -2.4) * mm, "end": v(-0.44, -2.4) * mm});
            skLineSegment(sketch, "E724", {"start": v(-0.44, -2.37) * mm, "end": v(-0.44, -2.4) * mm});
            skLineSegment(sketch, "E725", {"start": v(-0.4, -2.37) * mm, "end": v(-0.4, -2.4) * mm});
            skLineSegment(sketch, "E726", {"start": v(-0.01, -2.37) * mm, "end": v(-0.01, -2.4) * mm});
            skLineSegment(sketch, "E727", {"start": v(-0.38, -2.37) * mm, "end": v(-0.38, -2.4) * mm});
            skLineSegment(sketch, "E728", {"start": v(-0.33, -2.37) * mm, "end": v(-0.33, -2.4) * mm});
            skLineSegment(sketch, "E729", {"start": v(-0.3, -2.37) * mm, "end": v(-0.3, -2.4) * mm});
            skLineSegment(sketch, "E730", {"start": v(-0.25, -2.37) * mm, "end": v(-0.25, -2.4) * mm});
            skLineSegment(sketch, "E731", {"start": v(-0.22, -2.37) * mm, "end": v(-0.22, -2.4) * mm});
            skLineSegment(sketch, "E732", {"start": v(-0.15, -2.37) * mm, "end": v(-0.15, -2.4) * mm});
            skLineSegment(sketch, "E733", {"start": v(-0.13, -2.37) * mm, "end": v(-0.13, -2.4) * mm});
            skLineSegment(sketch, "E734", {"start": v(-0.13, -2.37) * mm, "end": v(-0.01, -2.37) * mm});
            skLineSegment(sketch, "E735", {"start": v(-0.13, -2.4) * mm, "end": v(-0.01, -2.4) * mm});
            skLineSegment(sketch, "E736", {"start": v(-0.15, -2.37) * mm, "end": v(-0.22, -2.37) * mm});
            skLineSegment(sketch, "E737", {"start": v(-0.22, -2.4) * mm, "end": v(-0.15, -2.4) * mm});
            skLineSegment(sketch, "E738", {"start": v(-0.25, -2.37) * mm, "end": v(-0.3, -2.37) * mm});
            skLineSegment(sketch, "E739", {"start": v(-0.3, -2.4) * mm, "end": v(-0.25, -2.4) * mm});
            skLineSegment(sketch, "E740", {"start": v(-0.33, -2.37) * mm, "end": v(-0.38, -2.37) * mm});
            skLineSegment(sketch, "E741", {"start": v(-0.38, -2.4) * mm, "end": v(-0.33, -2.4) * mm});
            skLineSegment(sketch, "E742", {"start": v(-0.7, -2.43) * mm, "end": v(-0.74, -2.43) * mm});
            skLineSegment(sketch, "E743", {"start": v(-0.7, -2.47) * mm, "end": v(-0.74, -2.47) * mm});
            skLineSegment(sketch, "E744", {"start": v(-0.74, -2.43) * mm, "end": v(-0.74, -2.47) * mm});
            skLineSegment(sketch, "E745", {"start": v(-0.7, -2.43) * mm, "end": v(-0.7, -2.47) * mm});
            skLineSegment(sketch, "E746", {"start": v(-0.64, -2.43) * mm, "end": v(-0.68, -2.43) * mm});
            skLineSegment(sketch, "E747", {"start": v(-0.64, -2.47) * mm, "end": v(-0.68, -2.47) * mm});
            skLineSegment(sketch, "E748", {"start": v(-0.68, -2.43) * mm, "end": v(-0.68, -2.47) * mm});
            skLineSegment(sketch, "E749", {"start": v(-0.64, -2.43) * mm, "end": v(-0.64, -2.47) * mm});
            skLineSegment(sketch, "E750", {"start": v(-0.58, -2.43) * mm, "end": v(-0.62, -2.43) * mm});
            skLineSegment(sketch, "E751", {"start": v(-0.58, -2.47) * mm, "end": v(-0.62, -2.47) * mm});
            skLineSegment(sketch, "E752", {"start": v(-0.62, -2.43) * mm, "end": v(-0.62, -2.47) * mm});
            skLineSegment(sketch, "E753", {"start": v(-0.58, -2.43) * mm, "end": v(-0.58, -2.47) * mm});
            skLineSegment(sketch, "E754", {"start": v(-0.52, -2.43) * mm, "end": v(-0.56, -2.43) * mm});
            skLineSegment(sketch, "E755", {"start": v(-0.52, -2.47) * mm, "end": v(-0.56, -2.47) * mm});
            skLineSegment(sketch, "E756", {"start": v(-0.56, -2.43) * mm, "end": v(-0.56, -2.47) * mm});
            skLineSegment(sketch, "E757", {"start": v(-0.52, -2.43) * mm, "end": v(-0.52, -2.47) * mm});
            skLineSegment(sketch, "E758", {"start": v(-0.46, -2.43) * mm, "end": v(-0.5, -2.43) * mm});
            skLineSegment(sketch, "E759", {"start": v(-0.46, -2.47) * mm, "end": v(-0.5, -2.47) * mm});
            skLineSegment(sketch, "E760", {"start": v(-0.5, -2.43) * mm, "end": v(-0.5, -2.47) * mm});
            skLineSegment(sketch, "E761", {"start": v(-0.46, -2.43) * mm, "end": v(-0.46, -2.47) * mm});
            skLineSegment(sketch, "E762", {"start": v(-0.4, -2.43) * mm, "end": v(-0.44, -2.43) * mm});
            skLineSegment(sketch, "E763", {"start": v(-0.4, -2.47) * mm, "end": v(-0.44, -2.47) * mm});
            skLineSegment(sketch, "E764", {"start": v(-0.44, -2.43) * mm, "end": v(-0.44, -2.47) * mm});
            skLineSegment(sketch, "E765", {"start": v(-0.4, -2.43) * mm, "end": v(-0.4, -2.47) * mm});
            skLineSegment(sketch, "E766", {"start": v(-0.01, -2.43) * mm, "end": v(-0.01, -2.47) * mm});
            skLineSegment(sketch, "E767", {"start": v(-0.38, -2.43) * mm, "end": v(-0.38, -2.47) * mm});
            skLineSegment(sketch, "E768", {"start": v(-0.33, -2.43) * mm, "end": v(-0.33, -2.47) * mm});
            skLineSegment(sketch, "E769", {"start": v(-0.3, -2.43) * mm, "end": v(-0.3, -2.47) * mm});
            skLineSegment(sketch, "E770", {"start": v(-0.25, -2.43) * mm, "end": v(-0.25, -2.47) * mm});
            skLineSegment(sketch, "E771", {"start": v(-0.22, -2.43) * mm, "end": v(-0.22, -2.47) * mm});
            skLineSegment(sketch, "E772", {"start": v(-0.15, -2.43) * mm, "end": v(-0.15, -2.47) * mm});
            skLineSegment(sketch, "E773", {"start": v(-0.13, -2.43) * mm, "end": v(-0.13, -2.47) * mm});
            skLineSegment(sketch, "E774", {"start": v(-0.13, -2.43) * mm, "end": v(-0.01, -2.43) * mm});
            skLineSegment(sketch, "E775", {"start": v(-0.13, -2.47) * mm, "end": v(-0.01, -2.47) * mm});
            skLineSegment(sketch, "E776", {"start": v(-0.15, -2.43) * mm, "end": v(-0.22, -2.43) * mm});
            skLineSegment(sketch, "E777", {"start": v(-0.22, -2.47) * mm, "end": v(-0.15, -2.47) * mm});
            skLineSegment(sketch, "E778", {"start": v(-0.25, -2.43) * mm, "end": v(-0.3, -2.43) * mm});
            skLineSegment(sketch, "E779", {"start": v(-0.3, -2.47) * mm, "end": v(-0.25, -2.47) * mm});
            skLineSegment(sketch, "E780", {"start": v(-0.33, -2.43) * mm, "end": v(-0.38, -2.43) * mm});
            skLineSegment(sketch, "E781", {"start": v(-0.38, -2.47) * mm, "end": v(-0.33, -2.47) * mm});
            skLineSegment(sketch, "E782", {"start": v(-0.7, -2.49) * mm, "end": v(-0.74, -2.49) * mm});
            skLineSegment(sketch, "E783", {"start": v(-0.7, -2.53) * mm, "end": v(-0.74, -2.53) * mm});
            skLineSegment(sketch, "E784", {"start": v(-0.74, -2.49) * mm, "end": v(-0.74, -2.53) * mm});
            skLineSegment(sketch, "E785", {"start": v(-0.7, -2.49) * mm, "end": v(-0.7, -2.53) * mm});
            skLineSegment(sketch, "E786", {"start": v(-0.64, -2.49) * mm, "end": v(-0.68, -2.49) * mm});
            skLineSegment(sketch, "E787", {"start": v(-0.64, -2.53) * mm, "end": v(-0.68, -2.53) * mm});
            skLineSegment(sketch, "E788", {"start": v(-0.68, -2.49) * mm, "end": v(-0.68, -2.53) * mm});
            skLineSegment(sketch, "E789", {"start": v(-0.64, -2.49) * mm, "end": v(-0.64, -2.53) * mm});
            skLineSegment(sketch, "E790", {"start": v(-0.58, -2.49) * mm, "end": v(-0.62, -2.49) * mm});
            skLineSegment(sketch, "E791", {"start": v(-0.58, -2.53) * mm, "end": v(-0.62, -2.53) * mm});
            skLineSegment(sketch, "E792", {"start": v(-0.62, -2.49) * mm, "end": v(-0.62, -2.53) * mm});
            skLineSegment(sketch, "E793", {"start": v(-0.58, -2.49) * mm, "end": v(-0.58, -2.53) * mm});
            skLineSegment(sketch, "E794", {"start": v(-0.52, -2.49) * mm, "end": v(-0.56, -2.49) * mm});
            skLineSegment(sketch, "E795", {"start": v(-0.52, -2.53) * mm, "end": v(-0.56, -2.53) * mm});
            skLineSegment(sketch, "E796", {"start": v(-0.56, -2.49) * mm, "end": v(-0.56, -2.53) * mm});
            skLineSegment(sketch, "E797", {"start": v(-0.52, -2.49) * mm, "end": v(-0.52, -2.53) * mm});
            skLineSegment(sketch, "E798", {"start": v(-0.46, -2.49) * mm, "end": v(-0.5, -2.49) * mm});
            skLineSegment(sketch, "E799", {"start": v(-0.46, -2.53) * mm, "end": v(-0.5, -2.53) * mm});
            skLineSegment(sketch, "E800", {"start": v(-0.5, -2.49) * mm, "end": v(-0.5, -2.53) * mm});
            skLineSegment(sketch, "E801", {"start": v(-0.46, -2.49) * mm, "end": v(-0.46, -2.53) * mm});
            skLineSegment(sketch, "E802", {"start": v(-0.4, -2.49) * mm, "end": v(-0.44, -2.49) * mm});
            skLineSegment(sketch, "E803", {"start": v(-0.4, -2.53) * mm, "end": v(-0.44, -2.53) * mm});
            skLineSegment(sketch, "E804", {"start": v(-0.44, -2.49) * mm, "end": v(-0.44, -2.53) * mm});
            skLineSegment(sketch, "E805", {"start": v(-0.4, -2.49) * mm, "end": v(-0.4, -2.53) * mm});
            skLineSegment(sketch, "E806", {"start": v(-0.01, -2.49) * mm, "end": v(-0.01, -2.53) * mm});
            skLineSegment(sketch, "E807", {"start": v(-0.38, -2.49) * mm, "end": v(-0.38, -2.53) * mm});
            skLineSegment(sketch, "E808", {"start": v(-0.33, -2.49) * mm, "end": v(-0.33, -2.53) * mm});
            skLineSegment(sketch, "E809", {"start": v(-0.3, -2.49) * mm, "end": v(-0.3, -2.53) * mm});
            skLineSegment(sketch, "E810", {"start": v(-0.25, -2.49) * mm, "end": v(-0.25, -2.53) * mm});
            skLineSegment(sketch, "E811", {"start": v(-0.22, -2.49) * mm, "end": v(-0.22, -2.53) * mm});
            skLineSegment(sketch, "E812", {"start": v(-0.15, -2.49) * mm, "end": v(-0.15, -2.53) * mm});
            skLineSegment(sketch, "E813", {"start": v(-0.13, -2.49) * mm, "end": v(-0.13, -2.53) * mm});
            skLineSegment(sketch, "E814", {"start": v(-0.13, -2.49) * mm, "end": v(-0.01, -2.49) * mm});
            skLineSegment(sketch, "E815", {"start": v(-0.13, -2.53) * mm, "end": v(-0.01, -2.53) * mm});
            skLineSegment(sketch, "E816", {"start": v(-0.15, -2.49) * mm, "end": v(-0.22, -2.49) * mm});
            skLineSegment(sketch, "E817", {"start": v(-0.22, -2.53) * mm, "end": v(-0.15, -2.53) * mm});
            skLineSegment(sketch, "E818", {"start": v(-0.25, -2.49) * mm, "end": v(-0.3, -2.49) * mm});
            skLineSegment(sketch, "E819", {"start": v(-0.3, -2.53) * mm, "end": v(-0.25, -2.53) * mm});
            skLineSegment(sketch, "E820", {"start": v(-0.33, -2.49) * mm, "end": v(-0.38, -2.49) * mm});
            skLineSegment(sketch, "E821", {"start": v(-0.38, -2.53) * mm, "end": v(-0.33, -2.53) * mm});
            skLineSegment(sketch, "E822", {"start": v(-0.7, -2.55) * mm, "end": v(-0.74, -2.55) * mm});
            skLineSegment(sketch, "E823", {"start": v(-0.7, -2.59) * mm, "end": v(-0.74, -2.59) * mm});
            skLineSegment(sketch, "E824", {"start": v(-0.74, -2.55) * mm, "end": v(-0.74, -2.59) * mm});
            skLineSegment(sketch, "E825", {"start": v(-0.7, -2.55) * mm, "end": v(-0.7, -2.59) * mm});
            skLineSegment(sketch, "E826", {"start": v(-0.64, -2.55) * mm, "end": v(-0.68, -2.55) * mm});
            skLineSegment(sketch, "E827", {"start": v(-0.64, -2.59) * mm, "end": v(-0.68, -2.59) * mm});
            skLineSegment(sketch, "E828", {"start": v(-0.68, -2.55) * mm, "end": v(-0.68, -2.59) * mm});
            skLineSegment(sketch, "E829", {"start": v(-0.64, -2.55) * mm, "end": v(-0.64, -2.59) * mm});
            skLineSegment(sketch, "E830", {"start": v(-0.58, -2.55) * mm, "end": v(-0.62, -2.55) * mm});
            skLineSegment(sketch, "E831", {"start": v(-0.58, -2.59) * mm, "end": v(-0.62, -2.59) * mm});
            skLineSegment(sketch, "E832", {"start": v(-0.62, -2.55) * mm, "end": v(-0.62, -2.59) * mm});
            skLineSegment(sketch, "E833", {"start": v(-0.58, -2.55) * mm, "end": v(-0.58, -2.59) * mm});
            skLineSegment(sketch, "E834", {"start": v(-0.52, -2.55) * mm, "end": v(-0.56, -2.55) * mm});
            skLineSegment(sketch, "E835", {"start": v(-0.52, -2.59) * mm, "end": v(-0.56, -2.59) * mm});
            skLineSegment(sketch, "E836", {"start": v(-0.56, -2.55) * mm, "end": v(-0.56, -2.59) * mm});
            skLineSegment(sketch, "E837", {"start": v(-0.52, -2.55) * mm, "end": v(-0.52, -2.59) * mm});
            skLineSegment(sketch, "E838", {"start": v(-0.46, -2.55) * mm, "end": v(-0.5, -2.55) * mm});
            skLineSegment(sketch, "E839", {"start": v(-0.46, -2.59) * mm, "end": v(-0.5, -2.59) * mm});
            skLineSegment(sketch, "E840", {"start": v(-0.5, -2.55) * mm, "end": v(-0.5, -2.59) * mm});
            skLineSegment(sketch, "E841", {"start": v(-0.46, -2.55) * mm, "end": v(-0.46, -2.59) * mm});
            skLineSegment(sketch, "E842", {"start": v(-0.4, -2.55) * mm, "end": v(-0.44, -2.55) * mm});
            skLineSegment(sketch, "E843", {"start": v(-0.4, -2.59) * mm, "end": v(-0.44, -2.59) * mm});
            skLineSegment(sketch, "E844", {"start": v(-0.44, -2.55) * mm, "end": v(-0.44, -2.59) * mm});
            skLineSegment(sketch, "E845", {"start": v(-0.4, -2.55) * mm, "end": v(-0.4, -2.59) * mm});
            skLineSegment(sketch, "E846", {"start": v(-0.01, -2.55) * mm, "end": v(-0.01, -2.59) * mm});
            skLineSegment(sketch, "E847", {"start": v(-0.38, -2.55) * mm, "end": v(-0.38, -2.59) * mm});
            skLineSegment(sketch, "E848", {"start": v(-0.33, -2.55) * mm, "end": v(-0.33, -2.59) * mm});
            skLineSegment(sketch, "E849", {"start": v(-0.3, -2.55) * mm, "end": v(-0.3, -2.59) * mm});
            skLineSegment(sketch, "E850", {"start": v(-0.25, -2.55) * mm, "end": v(-0.25, -2.59) * mm});
            skLineSegment(sketch, "E851", {"start": v(-0.22, -2.55) * mm, "end": v(-0.22, -2.59) * mm});
            skLineSegment(sketch, "E852", {"start": v(-0.15, -2.55) * mm, "end": v(-0.15, -2.59) * mm});
            skLineSegment(sketch, "E853", {"start": v(-0.13, -2.55) * mm, "end": v(-0.13, -2.59) * mm});
            skLineSegment(sketch, "E854", {"start": v(-0.13, -2.55) * mm, "end": v(-0.01, -2.55) * mm});
            skLineSegment(sketch, "E855", {"start": v(-0.13, -2.59) * mm, "end": v(-0.01, -2.59) * mm});
            skLineSegment(sketch, "E856", {"start": v(-0.15, -2.55) * mm, "end": v(-0.22, -2.55) * mm});
            skLineSegment(sketch, "E857", {"start": v(-0.22, -2.59) * mm, "end": v(-0.15, -2.59) * mm});
            skLineSegment(sketch, "E858", {"start": v(-0.25, -2.55) * mm, "end": v(-0.3, -2.55) * mm});
            skLineSegment(sketch, "E859", {"start": v(-0.3, -2.59) * mm, "end": v(-0.25, -2.59) * mm});
            skLineSegment(sketch, "E860", {"start": v(-0.33, -2.55) * mm, "end": v(-0.38, -2.55) * mm});
            skLineSegment(sketch, "E861", {"start": v(-0.38, -2.59) * mm, "end": v(-0.33, -2.59) * mm});
            skLineSegment(sketch, "E862", {"start": v(-0.7, -2.6) * mm, "end": v(-0.74, -2.6) * mm});
            skLineSegment(sketch, "E863", {"start": v(-0.7, -2.65) * mm, "end": v(-0.74, -2.65) * mm});
            skLineSegment(sketch, "E864", {"start": v(-0.74, -2.6) * mm, "end": v(-0.74, -2.65) * mm});
            skLineSegment(sketch, "E865", {"start": v(-0.7, -2.6) * mm, "end": v(-0.7, -2.65) * mm});
            skLineSegment(sketch, "E866", {"start": v(-0.64, -2.6) * mm, "end": v(-0.68, -2.6) * mm});
            skLineSegment(sketch, "E867", {"start": v(-0.64, -2.65) * mm, "end": v(-0.68, -2.65) * mm});
            skLineSegment(sketch, "E868", {"start": v(-0.68, -2.6) * mm, "end": v(-0.68, -2.65) * mm});
            skLineSegment(sketch, "E869", {"start": v(-0.64, -2.6) * mm, "end": v(-0.64, -2.65) * mm});
            skLineSegment(sketch, "E870", {"start": v(-0.58, -2.6) * mm, "end": v(-0.62, -2.6) * mm});
            skLineSegment(sketch, "E871", {"start": v(-0.58, -2.65) * mm, "end": v(-0.62, -2.65) * mm});
            skLineSegment(sketch, "E872", {"start": v(-0.62, -2.6) * mm, "end": v(-0.62, -2.65) * mm});
            skLineSegment(sketch, "E873", {"start": v(-0.58, -2.6) * mm, "end": v(-0.58, -2.65) * mm});
            skLineSegment(sketch, "E874", {"start": v(-0.52, -2.6) * mm, "end": v(-0.56, -2.6) * mm});
            skLineSegment(sketch, "E875", {"start": v(-0.52, -2.65) * mm, "end": v(-0.56, -2.65) * mm});
            skLineSegment(sketch, "E876", {"start": v(-0.56, -2.6) * mm, "end": v(-0.56, -2.65) * mm});
            skLineSegment(sketch, "E877", {"start": v(-0.52, -2.6) * mm, "end": v(-0.52, -2.65) * mm});
            skLineSegment(sketch, "E878", {"start": v(-0.46, -2.6) * mm, "end": v(-0.5, -2.6) * mm});
            skLineSegment(sketch, "E879", {"start": v(-0.46, -2.65) * mm, "end": v(-0.5, -2.65) * mm});
            skLineSegment(sketch, "E880", {"start": v(-0.5, -2.6) * mm, "end": v(-0.5, -2.65) * mm});
            skLineSegment(sketch, "E881", {"start": v(-0.46, -2.6) * mm, "end": v(-0.46, -2.65) * mm});
            skLineSegment(sketch, "E882", {"start": v(-0.4, -2.6) * mm, "end": v(-0.44, -2.6) * mm});
            skLineSegment(sketch, "E883", {"start": v(-0.4, -2.65) * mm, "end": v(-0.44, -2.65) * mm});
            skLineSegment(sketch, "E884", {"start": v(-0.44, -2.6) * mm, "end": v(-0.44, -2.65) * mm});
            skLineSegment(sketch, "E885", {"start": v(-0.4, -2.6) * mm, "end": v(-0.4, -2.65) * mm});
            skLineSegment(sketch, "E886", {"start": v(-0.01, -2.6) * mm, "end": v(-0.01, -2.65) * mm});
            skLineSegment(sketch, "E887", {"start": v(-0.38, -2.6) * mm, "end": v(-0.38, -2.65) * mm});
            skLineSegment(sketch, "E888", {"start": v(-0.33, -2.6) * mm, "end": v(-0.33, -2.65) * mm});
            skLineSegment(sketch, "E889", {"start": v(-0.3, -2.6) * mm, "end": v(-0.3, -2.65) * mm});
            skLineSegment(sketch, "E890", {"start": v(-0.25, -2.6) * mm, "end": v(-0.25, -2.65) * mm});
            skLineSegment(sketch, "E891", {"start": v(-0.22, -2.6) * mm, "end": v(-0.22, -2.65) * mm});
            skLineSegment(sketch, "E892", {"start": v(-0.15, -2.6) * mm, "end": v(-0.15, -2.65) * mm});
            skLineSegment(sketch, "E893", {"start": v(-0.13, -2.6) * mm, "end": v(-0.13, -2.65) * mm});
            skLineSegment(sketch, "E894", {"start": v(-0.13, -2.6) * mm, "end": v(-0.01, -2.6) * mm});
            skLineSegment(sketch, "E895", {"start": v(-0.13, -2.65) * mm, "end": v(-0.01, -2.65) * mm});
            skLineSegment(sketch, "E896", {"start": v(-0.15, -2.6) * mm, "end": v(-0.22, -2.6) * mm});
            skLineSegment(sketch, "E897", {"start": v(-0.22, -2.65) * mm, "end": v(-0.15, -2.65) * mm});
            skLineSegment(sketch, "E898", {"start": v(-0.25, -2.6) * mm, "end": v(-0.3, -2.6) * mm});
            skLineSegment(sketch, "E899", {"start": v(-0.3, -2.65) * mm, "end": v(-0.25, -2.65) * mm});
            skLineSegment(sketch, "E900", {"start": v(-0.33, -2.6) * mm, "end": v(-0.38, -2.6) * mm});
            skLineSegment(sketch, "E901", {"start": v(-0.38, -2.65) * mm, "end": v(-0.33, -2.65) * mm});
            skLineSegment(sketch, "E902", {"start": v(-0.7, -2.67) * mm, "end": v(-0.74, -2.67) * mm});
            skLineSegment(sketch, "E903", {"start": v(-0.7, -2.7) * mm, "end": v(-0.74, -2.7) * mm});
            skLineSegment(sketch, "E904", {"start": v(-0.74, -2.67) * mm, "end": v(-0.74, -2.7) * mm});
            skLineSegment(sketch, "E905", {"start": v(-0.7, -2.67) * mm, "end": v(-0.7, -2.7) * mm});
            skLineSegment(sketch, "E906", {"start": v(-0.64, -2.67) * mm, "end": v(-0.68, -2.67) * mm});
            skLineSegment(sketch, "E907", {"start": v(-0.64, -2.7) * mm, "end": v(-0.68, -2.7) * mm});
            skLineSegment(sketch, "E908", {"start": v(-0.68, -2.67) * mm, "end": v(-0.68, -2.7) * mm});
            skLineSegment(sketch, "E909", {"start": v(-0.64, -2.67) * mm, "end": v(-0.64, -2.7) * mm});
            skLineSegment(sketch, "E910", {"start": v(-0.58, -2.67) * mm, "end": v(-0.62, -2.67) * mm});
            skLineSegment(sketch, "E911", {"start": v(-0.58, -2.7) * mm, "end": v(-0.62, -2.7) * mm});
            skLineSegment(sketch, "E912", {"start": v(-0.62, -2.67) * mm, "end": v(-0.62, -2.7) * mm});
            skLineSegment(sketch, "E913", {"start": v(-0.58, -2.67) * mm, "end": v(-0.58, -2.7) * mm});
            skLineSegment(sketch, "E914", {"start": v(-0.52, -2.67) * mm, "end": v(-0.56, -2.67) * mm});
            skLineSegment(sketch, "E915", {"start": v(-0.52, -2.7) * mm, "end": v(-0.56, -2.7) * mm});
            skLineSegment(sketch, "E916", {"start": v(-0.56, -2.67) * mm, "end": v(-0.56, -2.7) * mm});
            skLineSegment(sketch, "E917", {"start": v(-0.52, -2.67) * mm, "end": v(-0.52, -2.7) * mm});
            skLineSegment(sketch, "E918", {"start": v(-0.46, -2.67) * mm, "end": v(-0.5, -2.67) * mm});
            skLineSegment(sketch, "E919", {"start": v(-0.46, -2.7) * mm, "end": v(-0.5, -2.7) * mm});
            skLineSegment(sketch, "E920", {"start": v(-0.5, -2.67) * mm, "end": v(-0.5, -2.7) * mm});
            skLineSegment(sketch, "E921", {"start": v(-0.46, -2.67) * mm, "end": v(-0.46, -2.7) * mm});
            skLineSegment(sketch, "E922", {"start": v(-0.4, -2.67) * mm, "end": v(-0.44, -2.67) * mm});
            skLineSegment(sketch, "E923", {"start": v(-0.4, -2.7) * mm, "end": v(-0.44, -2.7) * mm});
            skLineSegment(sketch, "E924", {"start": v(-0.44, -2.67) * mm, "end": v(-0.44, -2.7) * mm});
            skLineSegment(sketch, "E925", {"start": v(-0.4, -2.67) * mm, "end": v(-0.4, -2.7) * mm});
            skLineSegment(sketch, "E926", {"start": v(-0.01, -2.67) * mm, "end": v(-0.01, -2.7) * mm});
            skLineSegment(sketch, "E927", {"start": v(-0.38, -2.67) * mm, "end": v(-0.38, -2.7) * mm});
            skLineSegment(sketch, "E928", {"start": v(-0.33, -2.67) * mm, "end": v(-0.33, -2.7) * mm});
            skLineSegment(sketch, "E929", {"start": v(-0.3, -2.67) * mm, "end": v(-0.3, -2.7) * mm});
            skLineSegment(sketch, "E930", {"start": v(-0.25, -2.67) * mm, "end": v(-0.25, -2.7) * mm});
            skLineSegment(sketch, "E931", {"start": v(-0.22, -2.67) * mm, "end": v(-0.22, -2.7) * mm});
            skLineSegment(sketch, "E932", {"start": v(-0.15, -2.67) * mm, "end": v(-0.15, -2.7) * mm});
            skLineSegment(sketch, "E933", {"start": v(-0.13, -2.67) * mm, "end": v(-0.13, -2.7) * mm});
            skLineSegment(sketch, "E934", {"start": v(-0.13, -2.67) * mm, "end": v(-0.01, -2.67) * mm});
            skLineSegment(sketch, "E935", {"start": v(-0.13, -2.7) * mm, "end": v(-0.01, -2.7) * mm});
            skLineSegment(sketch, "E936", {"start": v(-0.15, -2.67) * mm, "end": v(-0.22, -2.67) * mm});
            skLineSegment(sketch, "E937", {"start": v(-0.22, -2.7) * mm, "end": v(-0.15, -2.7) * mm});
            skLineSegment(sketch, "E938", {"start": v(-0.25, -2.67) * mm, "end": v(-0.3, -2.67) * mm});
            skLineSegment(sketch, "E939", {"start": v(-0.3, -2.7) * mm, "end": v(-0.25, -2.7) * mm});
            skLineSegment(sketch, "E940", {"start": v(-0.33, -2.67) * mm, "end": v(-0.38, -2.67) * mm});
            skLineSegment(sketch, "E941", {"start": v(-0.38, -2.7) * mm, "end": v(-0.33, -2.7) * mm});
            skLineSegment(sketch, "E942", {"start": v(-0.7, -2.73) * mm, "end": v(-0.74, -2.73) * mm});
            skLineSegment(sketch, "E943", {"start": v(-0.7, -2.77) * mm, "end": v(-0.74, -2.77) * mm});
            skLineSegment(sketch, "E944", {"start": v(-0.74, -2.73) * mm, "end": v(-0.74, -2.77) * mm});
            skLineSegment(sketch, "E945", {"start": v(-0.7, -2.73) * mm, "end": v(-0.7, -2.77) * mm});
            skLineSegment(sketch, "E946", {"start": v(-0.64, -2.73) * mm, "end": v(-0.68, -2.73) * mm});
            skLineSegment(sketch, "E947", {"start": v(-0.64, -2.77) * mm, "end": v(-0.68, -2.77) * mm});
            skLineSegment(sketch, "E948", {"start": v(-0.68, -2.73) * mm, "end": v(-0.68, -2.77) * mm});
            skLineSegment(sketch, "E949", {"start": v(-0.64, -2.73) * mm, "end": v(-0.64, -2.77) * mm});
            skLineSegment(sketch, "E950", {"start": v(-0.58, -2.73) * mm, "end": v(-0.62, -2.73) * mm});
            skLineSegment(sketch, "E951", {"start": v(-0.58, -2.77) * mm, "end": v(-0.62, -2.77) * mm});
            skLineSegment(sketch, "E952", {"start": v(-0.62, -2.73) * mm, "end": v(-0.62, -2.77) * mm});
            skLineSegment(sketch, "E953", {"start": v(-0.58, -2.73) * mm, "end": v(-0.58, -2.77) * mm});
            skLineSegment(sketch, "E954", {"start": v(-0.52, -2.73) * mm, "end": v(-0.56, -2.73) * mm});
            skLineSegment(sketch, "E955", {"start": v(-0.52, -2.77) * mm, "end": v(-0.56, -2.77) * mm});
            skLineSegment(sketch, "E956", {"start": v(-0.56, -2.73) * mm, "end": v(-0.56, -2.77) * mm});
            skLineSegment(sketch, "E957", {"start": v(-0.52, -2.73) * mm, "end": v(-0.52, -2.77) * mm});
            skLineSegment(sketch, "E958", {"start": v(-0.46, -2.73) * mm, "end": v(-0.5, -2.73) * mm});
            skLineSegment(sketch, "E959", {"start": v(-0.46, -2.77) * mm, "end": v(-0.5, -2.77) * mm});
            skLineSegment(sketch, "E960", {"start": v(-0.5, -2.73) * mm, "end": v(-0.5, -2.77) * mm});
            skLineSegment(sketch, "E961", {"start": v(-0.46, -2.73) * mm, "end": v(-0.46, -2.77) * mm});
            skLineSegment(sketch, "E962", {"start": v(-0.4, -2.73) * mm, "end": v(-0.44, -2.73) * mm});
            skLineSegment(sketch, "E963", {"start": v(-0.4, -2.77) * mm, "end": v(-0.44, -2.77) * mm});
            skLineSegment(sketch, "E964", {"start": v(-0.44, -2.73) * mm, "end": v(-0.44, -2.77) * mm});
            skLineSegment(sketch, "E965", {"start": v(-0.4, -2.73) * mm, "end": v(-0.4, -2.77) * mm});
            skLineSegment(sketch, "E966", {"start": v(-0.01, -2.73) * mm, "end": v(-0.01, -2.77) * mm});
            skLineSegment(sketch, "E967", {"start": v(-0.38, -2.73) * mm, "end": v(-0.38, -2.77) * mm});
            skLineSegment(sketch, "E968", {"start": v(-0.33, -2.73) * mm, "end": v(-0.33, -2.77) * mm});
            skLineSegment(sketch, "E969", {"start": v(-0.3, -2.73) * mm, "end": v(-0.3, -2.77) * mm});
            skLineSegment(sketch, "E970", {"start": v(-0.25, -2.73) * mm, "end": v(-0.25, -2.77) * mm});
            skLineSegment(sketch, "E971", {"start": v(-0.22, -2.73) * mm, "end": v(-0.22, -2.77) * mm});
            skLineSegment(sketch, "E972", {"start": v(-0.15, -2.73) * mm, "end": v(-0.15, -2.77) * mm});
            skLineSegment(sketch, "E973", {"start": v(-0.13, -2.73) * mm, "end": v(-0.13, -2.77) * mm});
            skLineSegment(sketch, "E974", {"start": v(-0.13, -2.73) * mm, "end": v(-0.01, -2.73) * mm});
            skLineSegment(sketch, "E975", {"start": v(-0.13, -2.77) * mm, "end": v(-0.01, -2.77) * mm});
            skLineSegment(sketch, "E976", {"start": v(-0.15, -2.73) * mm, "end": v(-0.22, -2.73) * mm});
            skLineSegment(sketch, "E977", {"start": v(-0.22, -2.77) * mm, "end": v(-0.15, -2.77) * mm});
            skLineSegment(sketch, "E978", {"start": v(-0.25, -2.73) * mm, "end": v(-0.3, -2.73) * mm});
            skLineSegment(sketch, "E979", {"start": v(-0.3, -2.77) * mm, "end": v(-0.25, -2.77) * mm});
            skLineSegment(sketch, "E980", {"start": v(-0.33, -2.73) * mm, "end": v(-0.38, -2.73) * mm});
            skLineSegment(sketch, "E981", {"start": v(-0.38, -2.77) * mm, "end": v(-0.33, -2.77) * mm});
            skLineSegment(sketch, "E982", {"start": v(-0.7, -2.79) * mm, "end": v(-0.74, -2.79) * mm});
            skLineSegment(sketch, "E983", {"start": v(-0.7, -2.83) * mm, "end": v(-0.74, -2.83) * mm});
            skLineSegment(sketch, "E984", {"start": v(-0.74, -2.79) * mm, "end": v(-0.74, -2.83) * mm});
            skLineSegment(sketch, "E985", {"start": v(-0.7, -2.79) * mm, "end": v(-0.7, -2.83) * mm});
            skLineSegment(sketch, "E986", {"start": v(-0.64, -2.79) * mm, "end": v(-0.68, -2.79) * mm});
            skLineSegment(sketch, "E987", {"start": v(-0.64, -2.83) * mm, "end": v(-0.68, -2.83) * mm});
            skLineSegment(sketch, "E988", {"start": v(-0.68, -2.79) * mm, "end": v(-0.68, -2.83) * mm});
            skLineSegment(sketch, "E989", {"start": v(-0.64, -2.79) * mm, "end": v(-0.64, -2.83) * mm});
            skLineSegment(sketch, "E990", {"start": v(-0.58, -2.79) * mm, "end": v(-0.62, -2.79) * mm});
            skLineSegment(sketch, "E991", {"start": v(-0.58, -2.83) * mm, "end": v(-0.62, -2.83) * mm});
            skLineSegment(sketch, "E992", {"start": v(-0.62, -2.79) * mm, "end": v(-0.62, -2.83) * mm});
            skLineSegment(sketch, "E993", {"start": v(-0.58, -2.79) * mm, "end": v(-0.58, -2.83) * mm});
            skLineSegment(sketch, "E994", {"start": v(-0.52, -2.79) * mm, "end": v(-0.56, -2.79) * mm});
            skLineSegment(sketch, "E995", {"start": v(-0.52, -2.83) * mm, "end": v(-0.56, -2.83) * mm});
            skLineSegment(sketch, "E996", {"start": v(-0.56, -2.79) * mm, "end": v(-0.56, -2.83) * mm});
            skLineSegment(sketch, "E997", {"start": v(-0.52, -2.79) * mm, "end": v(-0.52, -2.83) * mm});
            skLineSegment(sketch, "E998", {"start": v(-0.46, -2.79) * mm, "end": v(-0.5, -2.79) * mm});
            skLineSegment(sketch, "E999", {"start": v(-0.46, -2.83) * mm, "end": v(-0.5, -2.83) * mm});
            skLineSegment(sketch, "E1000", {"start": v(-0.5, -2.79) * mm, "end": v(-0.5, -2.83) * mm});
            skLineSegment(sketch, "E1001", {"start": v(-0.46, -2.79) * mm, "end": v(-0.46, -2.83) * mm});
            skLineSegment(sketch, "E1002", {"start": v(-0.4, -2.79) * mm, "end": v(-0.44, -2.79) * mm});
            skLineSegment(sketch, "E1003", {"start": v(-0.4, -2.83) * mm, "end": v(-0.44, -2.83) * mm});
            skLineSegment(sketch, "E1004", {"start": v(-0.44, -2.79) * mm, "end": v(-0.44, -2.83) * mm});
            skLineSegment(sketch, "E1005", {"start": v(-0.4, -2.79) * mm, "end": v(-0.4, -2.83) * mm});
            skLineSegment(sketch, "E1006", {"start": v(-0.01, -2.79) * mm, "end": v(-0.01, -2.83) * mm});
            skLineSegment(sketch, "E1007", {"start": v(-0.38, -2.79) * mm, "end": v(-0.38, -2.83) * mm});
            skLineSegment(sketch, "E1008", {"start": v(-0.33, -2.79) * mm, "end": v(-0.33, -2.83) * mm});
            skLineSegment(sketch, "E1009", {"start": v(-0.3, -2.79) * mm, "end": v(-0.3, -2.83) * mm});
            skLineSegment(sketch, "E1010", {"start": v(-0.25, -2.79) * mm, "end": v(-0.25, -2.83) * mm});
            skLineSegment(sketch, "E1011", {"start": v(-0.22, -2.79) * mm, "end": v(-0.22, -2.83) * mm});
            skLineSegment(sketch, "E1012", {"start": v(-0.15, -2.79) * mm, "end": v(-0.15, -2.83) * mm});
            skLineSegment(sketch, "E1013", {"start": v(-0.13, -2.79) * mm, "end": v(-0.13, -2.83) * mm});
            skLineSegment(sketch, "E1014", {"start": v(-0.13, -2.79) * mm, "end": v(-0.01, -2.79) * mm});
            skLineSegment(sketch, "E1015", {"start": v(-0.13, -2.83) * mm, "end": v(-0.01, -2.83) * mm});
            skLineSegment(sketch, "E1016", {"start": v(-0.15, -2.79) * mm, "end": v(-0.22, -2.79) * mm});
            skLineSegment(sketch, "E1017", {"start": v(-0.22, -2.83) * mm, "end": v(-0.15, -2.83) * mm});
            skLineSegment(sketch, "E1018", {"start": v(-0.25, -2.79) * mm, "end": v(-0.3, -2.79) * mm});
            skLineSegment(sketch, "E1019", {"start": v(-0.3, -2.83) * mm, "end": v(-0.25, -2.83) * mm});
            skLineSegment(sketch, "E1020", {"start": v(-0.33, -2.79) * mm, "end": v(-0.38, -2.79) * mm});
            skLineSegment(sketch, "E1021", {"start": v(-0.38, -2.83) * mm, "end": v(-0.33, -2.83) * mm});
            skLineSegment(sketch, "E1022", {"start": v(0.58, -1.33) * mm, "end": v(0.74, -1.33) * mm});
            skLineSegment(sketch, "E1023", {"start": v(0.7, -1.35) * mm, "end": v(0.74, -1.35) * mm});
            skLineSegment(sketch, "E1024", {"start": v(0.7, -1.39) * mm, "end": v(0.74, -1.39) * mm});
            skLineSegment(sketch, "E1025", {"start": v(0.01, -1.23) * mm, "end": v(0.01, -1.33) * mm});
            skLineSegment(sketch, "E1026", {"start": v(0.01, -1.35) * mm, "end": v(0.01, -1.39) * mm});
            skLineSegment(sketch, "E1027", {"start": v(0.74, -1.35) * mm, "end": v(0.74, -1.39) * mm});
            skLineSegment(sketch, "E1028", {"start": v(0.7, -1.35) * mm, "end": v(0.7, -1.39) * mm});
            skLineSegment(sketch, "E1029", {"start": v(0.58, -1.23) * mm, "end": v(0.58, -1.33) * mm});
            skLineSegment(sketch, "E1030", {"start": v(0.56, -1.23) * mm, "end": v(0.56, -1.33) * mm});
            skLineSegment(sketch, "E1031", {"start": v(0.52, -1.23) * mm, "end": v(0.52, -1.33) * mm});
            skLineSegment(sketch, "E1032", {"start": v(0.52, -1.33) * mm, "end": v(0.56, -1.33) * mm});
            skLineSegment(sketch, "E1033", {"start": v(0.5, -1.23) * mm, "end": v(0.5, -1.33) * mm});
            skLineSegment(sketch, "E1034", {"start": v(0.46, -1.23) * mm, "end": v(0.46, -1.33) * mm});
            skLineSegment(sketch, "E1035", {"start": v(0.46, -1.33) * mm, "end": v(0.5, -1.33) * mm});
            skLineSegment(sketch, "E1036", {"start": v(0.44, -1.23) * mm, "end": v(0.44, -1.33) * mm});
            skLineSegment(sketch, "E1037", {"start": v(0.4, -1.23) * mm, "end": v(0.4, -1.33) * mm});
            skLineSegment(sketch, "E1038", {"start": v(0.38, -1.23) * mm, "end": v(0.38, -1.33) * mm});
            skLineSegment(sketch, "E1039", {"start": v(0.33, -1.23) * mm, "end": v(0.33, -1.33) * mm});
            skLineSegment(sketch, "E1040", {"start": v(0.3, -1.23) * mm, "end": v(0.3, -1.33) * mm});
            skLineSegment(sketch, "E1041", {"start": v(0.25, -1.23) * mm, "end": v(0.25, -1.33) * mm});
            skLineSegment(sketch, "E1042", {"start": v(0.22, -1.23) * mm, "end": v(0.22, -1.33) * mm});
            skLineSegment(sketch, "E1043", {"start": v(0.15, -1.23) * mm, "end": v(0.15, -1.33) * mm});
            skLineSegment(sketch, "E1044", {"start": v(0.13, -1.23) * mm, "end": v(0.13, -1.33) * mm});
            skLineSegment(sketch, "E1045", {"start": v(0.4, -1.33) * mm, "end": v(0.44, -1.33) * mm});
            skLineSegment(sketch, "E1046", {"start": v(0.7, -1.4) * mm, "end": v(0.74, -1.4) * mm});
            skLineSegment(sketch, "E1047", {"start": v(0.7, -1.45) * mm, "end": v(0.74, -1.45) * mm});
            skLineSegment(sketch, "E1048", {"start": v(0.74, -1.4) * mm, "end": v(0.74, -1.45) * mm});
            skLineSegment(sketch, "E1049", {"start": v(0.7, -1.4) * mm, "end": v(0.7, -1.45) * mm});
            skLineSegment(sketch, "E1050", {"start": v(0.7, -1.47) * mm, "end": v(0.74, -1.47) * mm});
            skLineSegment(sketch, "E1051", {"start": v(0.7, -1.5) * mm, "end": v(0.74, -1.5) * mm});
            skLineSegment(sketch, "E1052", {"start": v(0.74, -1.47) * mm, "end": v(0.74, -1.5) * mm});
            skLineSegment(sketch, "E1053", {"start": v(0.7, -1.47) * mm, "end": v(0.7, -1.5) * mm});
            skLineSegment(sketch, "E1054", {"start": v(0.7, -1.53) * mm, "end": v(0.74, -1.53) * mm});
            skLineSegment(sketch, "E1055", {"start": v(0.7, -1.57) * mm, "end": v(0.74, -1.57) * mm});
            skLineSegment(sketch, "E1056", {"start": v(0.74, -1.53) * mm, "end": v(0.74, -1.57) * mm});
            skLineSegment(sketch, "E1057", {"start": v(0.7, -1.53) * mm, "end": v(0.7, -1.57) * mm});
            skLineSegment(sketch, "E1058", {"start": v(0.7, -1.59) * mm, "end": v(0.74, -1.59) * mm});
            skLineSegment(sketch, "E1059", {"start": v(0.7, -1.63) * mm, "end": v(0.74, -1.63) * mm});
            skLineSegment(sketch, "E1060", {"start": v(0.74, -1.59) * mm, "end": v(0.74, -1.63) * mm});
            skLineSegment(sketch, "E1061", {"start": v(0.7, -1.59) * mm, "end": v(0.7, -1.63) * mm});
            skLineSegment(sketch, "E1062", {"start": v(0.7, -1.65) * mm, "end": v(0.74, -1.65) * mm});
            skLineSegment(sketch, "E1063", {"start": v(0.7, -1.69) * mm, "end": v(0.74, -1.69) * mm});
            skLineSegment(sketch, "E1064", {"start": v(0.74, -1.65) * mm, "end": v(0.74, -1.69) * mm});
            skLineSegment(sketch, "E1065", {"start": v(0.7, -1.65) * mm, "end": v(0.7, -1.69) * mm});
            skLineSegment(sketch, "E1066", {"start": v(0.64, -1.35) * mm, "end": v(0.68, -1.35) * mm});
            skLineSegment(sketch, "E1067", {"start": v(0.64, -1.39) * mm, "end": v(0.68, -1.39) * mm});
            skLineSegment(sketch, "E1068", {"start": v(0.68, -1.35) * mm, "end": v(0.68, -1.39) * mm});
            skLineSegment(sketch, "E1069", {"start": v(0.64, -1.35) * mm, "end": v(0.64, -1.39) * mm});
            skLineSegment(sketch, "E1070", {"start": v(0.64, -1.4) * mm, "end": v(0.68, -1.4) * mm});
            skLineSegment(sketch, "E1071", {"start": v(0.64, -1.45) * mm, "end": v(0.68, -1.45) * mm});
            skLineSegment(sketch, "E1072", {"start": v(0.68, -1.4) * mm, "end": v(0.68, -1.45) * mm});
            skLineSegment(sketch, "E1073", {"start": v(0.64, -1.4) * mm, "end": v(0.64, -1.45) * mm});
            skLineSegment(sketch, "E1074", {"start": v(0.64, -1.47) * mm, "end": v(0.68, -1.47) * mm});
            skLineSegment(sketch, "E1075", {"start": v(0.64, -1.5) * mm, "end": v(0.68, -1.5) * mm});
            skLineSegment(sketch, "E1076", {"start": v(0.68, -1.47) * mm, "end": v(0.68, -1.5) * mm});
            skLineSegment(sketch, "E1077", {"start": v(0.64, -1.47) * mm, "end": v(0.64, -1.5) * mm});
            skLineSegment(sketch, "E1078", {"start": v(0.64, -1.53) * mm, "end": v(0.68, -1.53) * mm});
            skLineSegment(sketch, "E1079", {"start": v(0.64, -1.57) * mm, "end": v(0.68, -1.57) * mm});
            skLineSegment(sketch, "E1080", {"start": v(0.68, -1.53) * mm, "end": v(0.68, -1.57) * mm});
            skLineSegment(sketch, "E1081", {"start": v(0.64, -1.53) * mm, "end": v(0.64, -1.57) * mm});
            skLineSegment(sketch, "E1082", {"start": v(0.64, -1.59) * mm, "end": v(0.68, -1.59) * mm});
            skLineSegment(sketch, "E1083", {"start": v(0.64, -1.63) * mm, "end": v(0.68, -1.63) * mm});
            skLineSegment(sketch, "E1084", {"start": v(0.68, -1.59) * mm, "end": v(0.68, -1.63) * mm});
            skLineSegment(sketch, "E1085", {"start": v(0.64, -1.59) * mm, "end": v(0.64, -1.63) * mm});
            skLineSegment(sketch, "E1086", {"start": v(0.64, -1.65) * mm, "end": v(0.68, -1.65) * mm});
            skLineSegment(sketch, "E1087", {"start": v(0.64, -1.69) * mm, "end": v(0.68, -1.69) * mm});
            skLineSegment(sketch, "E1088", {"start": v(0.68, -1.65) * mm, "end": v(0.68, -1.69) * mm});
            skLineSegment(sketch, "E1089", {"start": v(0.64, -1.65) * mm, "end": v(0.64, -1.69) * mm});
            skLineSegment(sketch, "E1090", {"start": v(0.58, -1.35) * mm, "end": v(0.62, -1.35) * mm});
            skLineSegment(sketch, "E1091", {"start": v(0.58, -1.39) * mm, "end": v(0.62, -1.39) * mm});
            skLineSegment(sketch, "E1092", {"start": v(0.62, -1.35) * mm, "end": v(0.62, -1.39) * mm});
            skLineSegment(sketch, "E1093", {"start": v(0.58, -1.35) * mm, "end": v(0.58, -1.39) * mm});
            skLineSegment(sketch, "E1094", {"start": v(0.58, -1.4) * mm, "end": v(0.62, -1.4) * mm});
            skLineSegment(sketch, "E1095", {"start": v(0.58, -1.45) * mm, "end": v(0.62, -1.45) * mm});
            skLineSegment(sketch, "E1096", {"start": v(0.62, -1.4) * mm, "end": v(0.62, -1.45) * mm});
            skLineSegment(sketch, "E1097", {"start": v(0.58, -1.4) * mm, "end": v(0.58, -1.45) * mm});
            skLineSegment(sketch, "E1098", {"start": v(0.58, -1.47) * mm, "end": v(0.62, -1.47) * mm});
            skLineSegment(sketch, "E1099", {"start": v(0.58, -1.5) * mm, "end": v(0.62, -1.5) * mm});
            skLineSegment(sketch, "E1100", {"start": v(0.62, -1.47) * mm, "end": v(0.62, -1.5) * mm});
            skLineSegment(sketch, "E1101", {"start": v(0.58, -1.47) * mm, "end": v(0.58, -1.5) * mm});
            skLineSegment(sketch, "E1102", {"start": v(0.58, -1.53) * mm, "end": v(0.62, -1.53) * mm});
            skLineSegment(sketch, "E1103", {"start": v(0.58, -1.57) * mm, "end": v(0.62, -1.57) * mm});
            skLineSegment(sketch, "E1104", {"start": v(0.62, -1.53) * mm, "end": v(0.62, -1.57) * mm});
            skLineSegment(sketch, "E1105", {"start": v(0.58, -1.53) * mm, "end": v(0.58, -1.57) * mm});
            skLineSegment(sketch, "E1106", {"start": v(0.58, -1.59) * mm, "end": v(0.62, -1.59) * mm});
            skLineSegment(sketch, "E1107", {"start": v(0.58, -1.63) * mm, "end": v(0.62, -1.63) * mm});
            skLineSegment(sketch, "E1108", {"start": v(0.62, -1.59) * mm, "end": v(0.62, -1.63) * mm});
            skLineSegment(sketch, "E1109", {"start": v(0.58, -1.59) * mm, "end": v(0.58, -1.63) * mm});
            skLineSegment(sketch, "E1110", {"start": v(0.58, -1.65) * mm, "end": v(0.62, -1.65) * mm});
            skLineSegment(sketch, "E1111", {"start": v(0.58, -1.69) * mm, "end": v(0.62, -1.69) * mm});
            skLineSegment(sketch, "E1112", {"start": v(0.62, -1.65) * mm, "end": v(0.62, -1.69) * mm});
            skLineSegment(sketch, "E1113", {"start": v(0.58, -1.65) * mm, "end": v(0.58, -1.69) * mm});
            skLineSegment(sketch, "E1114", {"start": v(0.52, -1.35) * mm, "end": v(0.56, -1.35) * mm});
            skLineSegment(sketch, "E1115", {"start": v(0.52, -1.39) * mm, "end": v(0.56, -1.39) * mm});
            skLineSegment(sketch, "E1116", {"start": v(0.56, -1.35) * mm, "end": v(0.56, -1.39) * mm});
            skLineSegment(sketch, "E1117", {"start": v(0.52, -1.35) * mm, "end": v(0.52, -1.39) * mm});
            skLineSegment(sketch, "E1118", {"start": v(0.52, -1.4) * mm, "end": v(0.56, -1.4) * mm});
            skLineSegment(sketch, "E1119", {"start": v(0.52, -1.45) * mm, "end": v(0.56, -1.45) * mm});
            skLineSegment(sketch, "E1120", {"start": v(0.56, -1.4) * mm, "end": v(0.56, -1.45) * mm});
            skLineSegment(sketch, "E1121", {"start": v(0.52, -1.4) * mm, "end": v(0.52, -1.45) * mm});
            skLineSegment(sketch, "E1122", {"start": v(0.52, -1.47) * mm, "end": v(0.56, -1.47) * mm});
            skLineSegment(sketch, "E1123", {"start": v(0.52, -1.5) * mm, "end": v(0.56, -1.5) * mm});
            skLineSegment(sketch, "E1124", {"start": v(0.56, -1.47) * mm, "end": v(0.56, -1.5) * mm});
            skLineSegment(sketch, "E1125", {"start": v(0.52, -1.47) * mm, "end": v(0.52, -1.5) * mm});
            skLineSegment(sketch, "E1126", {"start": v(0.52, -1.53) * mm, "end": v(0.56, -1.53) * mm});
            skLineSegment(sketch, "E1127", {"start": v(0.52, -1.57) * mm, "end": v(0.56, -1.57) * mm});
            skLineSegment(sketch, "E1128", {"start": v(0.56, -1.53) * mm, "end": v(0.56, -1.57) * mm});
            skLineSegment(sketch, "E1129", {"start": v(0.52, -1.53) * mm, "end": v(0.52, -1.57) * mm});
            skLineSegment(sketch, "E1130", {"start": v(0.52, -1.59) * mm, "end": v(0.56, -1.59) * mm});
            skLineSegment(sketch, "E1131", {"start": v(0.52, -1.63) * mm, "end": v(0.56, -1.63) * mm});
            skLineSegment(sketch, "E1132", {"start": v(0.56, -1.59) * mm, "end": v(0.56, -1.63) * mm});
            skLineSegment(sketch, "E1133", {"start": v(0.52, -1.59) * mm, "end": v(0.52, -1.63) * mm});
            skLineSegment(sketch, "E1134", {"start": v(0.52, -1.65) * mm, "end": v(0.56, -1.65) * mm});
            skLineSegment(sketch, "E1135", {"start": v(0.52, -1.69) * mm, "end": v(0.56, -1.69) * mm});
            skLineSegment(sketch, "E1136", {"start": v(0.56, -1.65) * mm, "end": v(0.56, -1.69) * mm});
            skLineSegment(sketch, "E1137", {"start": v(0.52, -1.65) * mm, "end": v(0.52, -1.69) * mm});
            skLineSegment(sketch, "E1138", {"start": v(0.46, -1.35) * mm, "end": v(0.5, -1.35) * mm});
            skLineSegment(sketch, "E1139", {"start": v(0.46, -1.39) * mm, "end": v(0.5, -1.39) * mm});
            skLineSegment(sketch, "E1140", {"start": v(0.5, -1.35) * mm, "end": v(0.5, -1.39) * mm});
            skLineSegment(sketch, "E1141", {"start": v(0.46, -1.35) * mm, "end": v(0.46, -1.39) * mm});
            skLineSegment(sketch, "E1142", {"start": v(0.46, -1.4) * mm, "end": v(0.5, -1.4) * mm});
            skLineSegment(sketch, "E1143", {"start": v(0.46, -1.45) * mm, "end": v(0.5, -1.45) * mm});
            skLineSegment(sketch, "E1144", {"start": v(0.5, -1.4) * mm, "end": v(0.5, -1.45) * mm});
            skLineSegment(sketch, "E1145", {"start": v(0.46, -1.4) * mm, "end": v(0.46, -1.45) * mm});
            skLineSegment(sketch, "E1146", {"start": v(0.46, -1.47) * mm, "end": v(0.5, -1.47) * mm});
            skLineSegment(sketch, "E1147", {"start": v(0.46, -1.5) * mm, "end": v(0.5, -1.5) * mm});
            skLineSegment(sketch, "E1148", {"start": v(0.5, -1.47) * mm, "end": v(0.5, -1.5) * mm});
            skLineSegment(sketch, "E1149", {"start": v(0.46, -1.47) * mm, "end": v(0.46, -1.5) * mm});
            skLineSegment(sketch, "E1150", {"start": v(0.46, -1.53) * mm, "end": v(0.5, -1.53) * mm});
            skLineSegment(sketch, "E1151", {"start": v(0.46, -1.57) * mm, "end": v(0.5, -1.57) * mm});
            skLineSegment(sketch, "E1152", {"start": v(0.5, -1.53) * mm, "end": v(0.5, -1.57) * mm});
            skLineSegment(sketch, "E1153", {"start": v(0.46, -1.53) * mm, "end": v(0.46, -1.57) * mm});
            skLineSegment(sketch, "E1154", {"start": v(0.46, -1.59) * mm, "end": v(0.5, -1.59) * mm});
            skLineSegment(sketch, "E1155", {"start": v(0.46, -1.63) * mm, "end": v(0.5, -1.63) * mm});
            skLineSegment(sketch, "E1156", {"start": v(0.5, -1.59) * mm, "end": v(0.5, -1.63) * mm});
            skLineSegment(sketch, "E1157", {"start": v(0.46, -1.59) * mm, "end": v(0.46, -1.63) * mm});
            skLineSegment(sketch, "E1158", {"start": v(0.46, -1.65) * mm, "end": v(0.5, -1.65) * mm});
            skLineSegment(sketch, "E1159", {"start": v(0.46, -1.69) * mm, "end": v(0.5, -1.69) * mm});
            skLineSegment(sketch, "E1160", {"start": v(0.5, -1.65) * mm, "end": v(0.5, -1.69) * mm});
            skLineSegment(sketch, "E1161", {"start": v(0.46, -1.65) * mm, "end": v(0.46, -1.69) * mm});
            skLineSegment(sketch, "E1162", {"start": v(0.4, -1.35) * mm, "end": v(0.44, -1.35) * mm});
            skLineSegment(sketch, "E1163", {"start": v(0.4, -1.39) * mm, "end": v(0.44, -1.39) * mm});
            skLineSegment(sketch, "E1164", {"start": v(0.44, -1.35) * mm, "end": v(0.44, -1.39) * mm});
            skLineSegment(sketch, "E1165", {"start": v(0.4, -1.35) * mm, "end": v(0.4, -1.39) * mm});
            skLineSegment(sketch, "E1166", {"start": v(0.38, -1.35) * mm, "end": v(0.38, -1.39) * mm});
            skLineSegment(sketch, "E1167", {"start": v(0.33, -1.35) * mm, "end": v(0.33, -1.39) * mm});
            skLineSegment(sketch, "E1168", {"start": v(0.3, -1.35) * mm, "end": v(0.3, -1.39) * mm});
            skLineSegment(sketch, "E1169", {"start": v(0.25, -1.35) * mm, "end": v(0.25, -1.39) * mm});
            skLineSegment(sketch, "E1170", {"start": v(0.22, -1.35) * mm, "end": v(0.22, -1.39) * mm});
            skLineSegment(sketch, "E1171", {"start": v(0.15, -1.35) * mm, "end": v(0.15, -1.39) * mm});
            skLineSegment(sketch, "E1172", {"start": v(0.13, -1.35) * mm, "end": v(0.13, -1.39) * mm});
            skLineSegment(sketch, "E1173", {"start": v(0.4, -1.4) * mm, "end": v(0.44, -1.4) * mm});
            skLineSegment(sketch, "E1174", {"start": v(0.4, -1.45) * mm, "end": v(0.44, -1.45) * mm});
            skLineSegment(sketch, "E1175", {"start": v(0.44, -1.4) * mm, "end": v(0.44, -1.45) * mm});
            skLineSegment(sketch, "E1176", {"start": v(0.4, -1.4) * mm, "end": v(0.4, -1.45) * mm});
            skLineSegment(sketch, "E1177", {"start": v(0.4, -1.47) * mm, "end": v(0.44, -1.47) * mm});
            skLineSegment(sketch, "E1178", {"start": v(0.4, -1.5) * mm, "end": v(0.44, -1.5) * mm});
            skLineSegment(sketch, "E1179", {"start": v(0.44, -1.47) * mm, "end": v(0.44, -1.5) * mm});
            skLineSegment(sketch, "E1180", {"start": v(0.4, -1.47) * mm, "end": v(0.4, -1.5) * mm});
            skLineSegment(sketch, "E1181", {"start": v(0.4, -1.53) * mm, "end": v(0.44, -1.53) * mm});
            skLineSegment(sketch, "E1182", {"start": v(0.4, -1.57) * mm, "end": v(0.44, -1.57) * mm});
            skLineSegment(sketch, "E1183", {"start": v(0.44, -1.53) * mm, "end": v(0.44, -1.57) * mm});
            skLineSegment(sketch, "E1184", {"start": v(0.4, -1.53) * mm, "end": v(0.4, -1.57) * mm});
            skLineSegment(sketch, "E1185", {"start": v(0.4, -1.59) * mm, "end": v(0.44, -1.59) * mm});
            skLineSegment(sketch, "E1186", {"start": v(0.4, -1.63) * mm, "end": v(0.44, -1.63) * mm});
            skLineSegment(sketch, "E1187", {"start": v(0.44, -1.59) * mm, "end": v(0.44, -1.63) * mm});
            skLineSegment(sketch, "E1188", {"start": v(0.4, -1.59) * mm, "end": v(0.4, -1.63) * mm});
            skLineSegment(sketch, "E1189", {"start": v(0.4, -1.65) * mm, "end": v(0.44, -1.65) * mm});
            skLineSegment(sketch, "E1190", {"start": v(0.4, -1.69) * mm, "end": v(0.44, -1.69) * mm});
            skLineSegment(sketch, "E1191", {"start": v(0.44, -1.65) * mm, "end": v(0.44, -1.69) * mm});
            skLineSegment(sketch, "E1192", {"start": v(0.4, -1.65) * mm, "end": v(0.4, -1.69) * mm});
            skLineSegment(sketch, "E1193", {"start": v(0.13, -1.35) * mm, "end": v(0.01, -1.35) * mm});
            skLineSegment(sketch, "E1194", {"start": v(0.13, -1.33) * mm, "end": v(0.01, -1.33) * mm});
            skLineSegment(sketch, "E1195", {"start": v(0.13, -1.39) * mm, "end": v(0.01, -1.39) * mm});
            skLineSegment(sketch, "E1196", {"start": v(0.15, -1.35) * mm, "end": v(0.22, -1.35) * mm});
            skLineSegment(sketch, "E1197", {"start": v(0.22, -1.39) * mm, "end": v(0.15, -1.39) * mm});
            skLineSegment(sketch, "E1198", {"start": v(0.25, -1.35) * mm, "end": v(0.3, -1.35) * mm});
            skLineSegment(sketch, "E1199", {"start": v(0.3, -1.39) * mm, "end": v(0.25, -1.39) * mm});
            skLineSegment(sketch, "E1200", {"start": v(0.33, -1.35) * mm, "end": v(0.38, -1.35) * mm});
            skLineSegment(sketch, "E1201", {"start": v(0.38, -1.39) * mm, "end": v(0.33, -1.39) * mm});
            skLineSegment(sketch, "E1202", {"start": v(0.38, -1.33) * mm, "end": v(0.33, -1.33) * mm});
            skLineSegment(sketch, "E1203", {"start": v(0.3, -1.33) * mm, "end": v(0.25, -1.33) * mm});
            skLineSegment(sketch, "E1204", {"start": v(0.22, -1.33) * mm, "end": v(0.15, -1.33) * mm});
            skLineSegment(sketch, "E1205", {"start": v(0.01, -1.4) * mm, "end": v(0.01, -1.45) * mm});
            skLineSegment(sketch, "E1206", {"start": v(0.38, -1.4) * mm, "end": v(0.38, -1.45) * mm});
            skLineSegment(sketch, "E1207", {"start": v(0.33, -1.4) * mm, "end": v(0.33, -1.45) * mm});
            skLineSegment(sketch, "E1208", {"start": v(0.3, -1.4) * mm, "end": v(0.3, -1.45) * mm});
            skLineSegment(sketch, "E1209", {"start": v(0.25, -1.4) * mm, "end": v(0.25, -1.45) * mm});
            skLineSegment(sketch, "E1210", {"start": v(0.22, -1.4) * mm, "end": v(0.22, -1.45) * mm});
            skLineSegment(sketch, "E1211", {"start": v(0.15, -1.4) * mm, "end": v(0.15, -1.45) * mm});
            skLineSegment(sketch, "E1212", {"start": v(0.13, -1.4) * mm, "end": v(0.13, -1.45) * mm});
            skLineSegment(sketch, "E1213", {"start": v(0.13, -1.4) * mm, "end": v(0.01, -1.4) * mm});
            skLineSegment(sketch, "E1214", {"start": v(0.13, -1.45) * mm, "end": v(0.01, -1.45) * mm});
            skLineSegment(sketch, "E1215", {"start": v(0.15, -1.4) * mm, "end": v(0.22, -1.4) * mm});
            skLineSegment(sketch, "E1216", {"start": v(0.22, -1.45) * mm, "end": v(0.15, -1.45) * mm});
            skLineSegment(sketch, "E1217", {"start": v(0.25, -1.4) * mm, "end": v(0.3, -1.4) * mm});
            skLineSegment(sketch, "E1218", {"start": v(0.3, -1.45) * mm, "end": v(0.25, -1.45) * mm});
            skLineSegment(sketch, "E1219", {"start": v(0.33, -1.4) * mm, "end": v(0.38, -1.4) * mm});
            skLineSegment(sketch, "E1220", {"start": v(0.38, -1.45) * mm, "end": v(0.33, -1.45) * mm});
            skLineSegment(sketch, "E1221", {"start": v(0.01, -1.47) * mm, "end": v(0.01, -1.5) * mm});
            skLineSegment(sketch, "E1222", {"start": v(0.38, -1.47) * mm, "end": v(0.38, -1.5) * mm});
            skLineSegment(sketch, "E1223", {"start": v(0.33, -1.47) * mm, "end": v(0.33, -1.5) * mm});
            skLineSegment(sketch, "E1224", {"start": v(0.3, -1.47) * mm, "end": v(0.3, -1.5) * mm});
            skLineSegment(sketch, "E1225", {"start": v(0.25, -1.47) * mm, "end": v(0.25, -1.5) * mm});
            skLineSegment(sketch, "E1226", {"start": v(0.22, -1.47) * mm, "end": v(0.22, -1.5) * mm});
            skLineSegment(sketch, "E1227", {"start": v(0.15, -1.47) * mm, "end": v(0.15, -1.5) * mm});
            skLineSegment(sketch, "E1228", {"start": v(0.13, -1.47) * mm, "end": v(0.13, -1.5) * mm});
            skLineSegment(sketch, "E1229", {"start": v(0.13, -1.47) * mm, "end": v(0.01, -1.47) * mm});
            skLineSegment(sketch, "E1230", {"start": v(0.13, -1.5) * mm, "end": v(0.01, -1.5) * mm});
            skLineSegment(sketch, "E1231", {"start": v(0.15, -1.47) * mm, "end": v(0.22, -1.47) * mm});
            skLineSegment(sketch, "E1232", {"start": v(0.22, -1.5) * mm, "end": v(0.15, -1.5) * mm});
            skLineSegment(sketch, "E1233", {"start": v(0.25, -1.47) * mm, "end": v(0.3, -1.47) * mm});
            skLineSegment(sketch, "E1234", {"start": v(0.3, -1.5) * mm, "end": v(0.25, -1.5) * mm});
            skLineSegment(sketch, "E1235", {"start": v(0.33, -1.47) * mm, "end": v(0.38, -1.47) * mm});
            skLineSegment(sketch, "E1236", {"start": v(0.38, -1.5) * mm, "end": v(0.33, -1.5) * mm});
            skLineSegment(sketch, "E1237", {"start": v(0.01, -1.53) * mm, "end": v(0.01, -1.57) * mm});
            skLineSegment(sketch, "E1238", {"start": v(0.38, -1.53) * mm, "end": v(0.38, -1.57) * mm});
            skLineSegment(sketch, "E1239", {"start": v(0.33, -1.53) * mm, "end": v(0.33, -1.57) * mm});
            skLineSegment(sketch, "E1240", {"start": v(0.3, -1.53) * mm, "end": v(0.3, -1.57) * mm});
            skLineSegment(sketch, "E1241", {"start": v(0.25, -1.53) * mm, "end": v(0.25, -1.57) * mm});
            skLineSegment(sketch, "E1242", {"start": v(0.22, -1.53) * mm, "end": v(0.22, -1.57) * mm});
            skLineSegment(sketch, "E1243", {"start": v(0.15, -1.53) * mm, "end": v(0.15, -1.57) * mm});
            skLineSegment(sketch, "E1244", {"start": v(0.13, -1.53) * mm, "end": v(0.13, -1.57) * mm});
            skLineSegment(sketch, "E1245", {"start": v(0.13, -1.53) * mm, "end": v(0.01, -1.53) * mm});
            skLineSegment(sketch, "E1246", {"start": v(0.13, -1.57) * mm, "end": v(0.01, -1.57) * mm});
            skLineSegment(sketch, "E1247", {"start": v(0.15, -1.53) * mm, "end": v(0.22, -1.53) * mm});
            skLineSegment(sketch, "E1248", {"start": v(0.22, -1.57) * mm, "end": v(0.15, -1.57) * mm});
            skLineSegment(sketch, "E1249", {"start": v(0.25, -1.53) * mm, "end": v(0.3, -1.53) * mm});
            skLineSegment(sketch, "E1250", {"start": v(0.3, -1.57) * mm, "end": v(0.25, -1.57) * mm});
            skLineSegment(sketch, "E1251", {"start": v(0.33, -1.53) * mm, "end": v(0.38, -1.53) * mm});
            skLineSegment(sketch, "E1252", {"start": v(0.38, -1.57) * mm, "end": v(0.33, -1.57) * mm});
            skLineSegment(sketch, "E1253", {"start": v(0.01, -1.59) * mm, "end": v(0.01, -1.63) * mm});
            skLineSegment(sketch, "E1254", {"start": v(0.38, -1.59) * mm, "end": v(0.38, -1.63) * mm});
            skLineSegment(sketch, "E1255", {"start": v(0.33, -1.59) * mm, "end": v(0.33, -1.63) * mm});
            skLineSegment(sketch, "E1256", {"start": v(0.3, -1.59) * mm, "end": v(0.3, -1.63) * mm});
            skLineSegment(sketch, "E1257", {"start": v(0.25, -1.59) * mm, "end": v(0.25, -1.63) * mm});
            skLineSegment(sketch, "E1258", {"start": v(0.22, -1.59) * mm, "end": v(0.22, -1.63) * mm});
            skLineSegment(sketch, "E1259", {"start": v(0.15, -1.59) * mm, "end": v(0.15, -1.63) * mm});
            skLineSegment(sketch, "E1260", {"start": v(0.13, -1.59) * mm, "end": v(0.13, -1.63) * mm});
            skLineSegment(sketch, "E1261", {"start": v(0.13, -1.59) * mm, "end": v(0.01, -1.59) * mm});
            skLineSegment(sketch, "E1262", {"start": v(0.13, -1.63) * mm, "end": v(0.01, -1.63) * mm});
            skLineSegment(sketch, "E1263", {"start": v(0.15, -1.59) * mm, "end": v(0.22, -1.59) * mm});
            skLineSegment(sketch, "E1264", {"start": v(0.22, -1.63) * mm, "end": v(0.15, -1.63) * mm});
            skLineSegment(sketch, "E1265", {"start": v(0.25, -1.59) * mm, "end": v(0.3, -1.59) * mm});
            skLineSegment(sketch, "E1266", {"start": v(0.3, -1.63) * mm, "end": v(0.25, -1.63) * mm});
            skLineSegment(sketch, "E1267", {"start": v(0.33, -1.59) * mm, "end": v(0.38, -1.59) * mm});
            skLineSegment(sketch, "E1268", {"start": v(0.38, -1.63) * mm, "end": v(0.33, -1.63) * mm});
            skLineSegment(sketch, "E1269", {"start": v(0.01, -1.65) * mm, "end": v(0.01, -1.69) * mm});
            skLineSegment(sketch, "E1270", {"start": v(0.38, -1.65) * mm, "end": v(0.38, -1.69) * mm});
            skLineSegment(sketch, "E1271", {"start": v(0.33, -1.65) * mm, "end": v(0.33, -1.69) * mm});
            skLineSegment(sketch, "E1272", {"start": v(0.3, -1.65) * mm, "end": v(0.3, -1.69) * mm});
            skLineSegment(sketch, "E1273", {"start": v(0.25, -1.65) * mm, "end": v(0.25, -1.69) * mm});
            skLineSegment(sketch, "E1274", {"start": v(0.22, -1.65) * mm, "end": v(0.22, -1.69) * mm});
            skLineSegment(sketch, "E1275", {"start": v(0.15, -1.65) * mm, "end": v(0.15, -1.69) * mm});
            skLineSegment(sketch, "E1276", {"start": v(0.13, -1.65) * mm, "end": v(0.13, -1.69) * mm});
            skLineSegment(sketch, "E1277", {"start": v(0.13, -1.65) * mm, "end": v(0.01, -1.65) * mm});
            skLineSegment(sketch, "E1278", {"start": v(0.13, -1.69) * mm, "end": v(0.01, -1.69) * mm});
            skLineSegment(sketch, "E1279", {"start": v(0.15, -1.65) * mm, "end": v(0.22, -1.65) * mm});
            skLineSegment(sketch, "E1280", {"start": v(0.22, -1.69) * mm, "end": v(0.15, -1.69) * mm});
            skLineSegment(sketch, "E1281", {"start": v(0.25, -1.65) * mm, "end": v(0.3, -1.65) * mm});
            skLineSegment(sketch, "E1282", {"start": v(0.3, -1.69) * mm, "end": v(0.25, -1.69) * mm});
            skLineSegment(sketch, "E1283", {"start": v(0.33, -1.65) * mm, "end": v(0.38, -1.65) * mm});
            skLineSegment(sketch, "E1284", {"start": v(0.38, -1.69) * mm, "end": v(0.33, -1.69) * mm});
            skLineSegment(sketch, "E1285", {"start": v(0.7, -1.7) * mm, "end": v(0.74, -1.7) * mm});
            skLineSegment(sketch, "E1286", {"start": v(0.7, -1.75) * mm, "end": v(0.74, -1.75) * mm});
            skLineSegment(sketch, "E1287", {"start": v(0.74, -1.7) * mm, "end": v(0.74, -1.75) * mm});
            skLineSegment(sketch, "E1288", {"start": v(0.7, -1.7) * mm, "end": v(0.7, -1.75) * mm});
            skLineSegment(sketch, "E1289", {"start": v(0.64, -1.7) * mm, "end": v(0.68, -1.7) * mm});
            skLineSegment(sketch, "E1290", {"start": v(0.64, -1.75) * mm, "end": v(0.68, -1.75) * mm});
            skLineSegment(sketch, "E1291", {"start": v(0.68, -1.7) * mm, "end": v(0.68, -1.75) * mm});
            skLineSegment(sketch, "E1292", {"start": v(0.64, -1.7) * mm, "end": v(0.64, -1.75) * mm});
            skLineSegment(sketch, "E1293", {"start": v(0.58, -1.7) * mm, "end": v(0.62, -1.7) * mm});
            skLineSegment(sketch, "E1294", {"start": v(0.58, -1.75) * mm, "end": v(0.62, -1.75) * mm});
            skLineSegment(sketch, "E1295", {"start": v(0.62, -1.7) * mm, "end": v(0.62, -1.75) * mm});
            skLineSegment(sketch, "E1296", {"start": v(0.58, -1.7) * mm, "end": v(0.58, -1.75) * mm});
            skLineSegment(sketch, "E1297", {"start": v(0.52, -1.7) * mm, "end": v(0.56, -1.7) * mm});
            skLineSegment(sketch, "E1298", {"start": v(0.52, -1.75) * mm, "end": v(0.56, -1.75) * mm});
            skLineSegment(sketch, "E1299", {"start": v(0.56, -1.7) * mm, "end": v(0.56, -1.75) * mm});
            skLineSegment(sketch, "E1300", {"start": v(0.52, -1.7) * mm, "end": v(0.52, -1.75) * mm});
            skLineSegment(sketch, "E1301", {"start": v(0.46, -1.7) * mm, "end": v(0.5, -1.7) * mm});
            skLineSegment(sketch, "E1302", {"start": v(0.46, -1.75) * mm, "end": v(0.5, -1.75) * mm});
            skLineSegment(sketch, "E1303", {"start": v(0.5, -1.7) * mm, "end": v(0.5, -1.75) * mm});
            skLineSegment(sketch, "E1304", {"start": v(0.46, -1.7) * mm, "end": v(0.46, -1.75) * mm});
            skLineSegment(sketch, "E1305", {"start": v(0.4, -1.7) * mm, "end": v(0.44, -1.7) * mm});
            skLineSegment(sketch, "E1306", {"start": v(0.4, -1.75) * mm, "end": v(0.44, -1.75) * mm});
            skLineSegment(sketch, "E1307", {"start": v(0.44, -1.7) * mm, "end": v(0.44, -1.75) * mm});
            skLineSegment(sketch, "E1308", {"start": v(0.4, -1.7) * mm, "end": v(0.4, -1.75) * mm});
            skLineSegment(sketch, "E1309", {"start": v(0.01, -1.7) * mm, "end": v(0.01, -1.75) * mm});
            skLineSegment(sketch, "E1310", {"start": v(0.38, -1.7) * mm, "end": v(0.38, -1.75) * mm});
            skLineSegment(sketch, "E1311", {"start": v(0.33, -1.7) * mm, "end": v(0.33, -1.75) * mm});
            skLineSegment(sketch, "E1312", {"start": v(0.3, -1.7) * mm, "end": v(0.3, -1.75) * mm});
            skLineSegment(sketch, "E1313", {"start": v(0.25, -1.7) * mm, "end": v(0.25, -1.75) * mm});
            skLineSegment(sketch, "E1314", {"start": v(0.22, -1.7) * mm, "end": v(0.22, -1.75) * mm});
            skLineSegment(sketch, "E1315", {"start": v(0.15, -1.7) * mm, "end": v(0.15, -1.75) * mm});
            skLineSegment(sketch, "E1316", {"start": v(0.13, -1.7) * mm, "end": v(0.13, -1.75) * mm});
            skLineSegment(sketch, "E1317", {"start": v(0.13, -1.7) * mm, "end": v(0.01, -1.7) * mm});
            skLineSegment(sketch, "E1318", {"start": v(0.13, -1.75) * mm, "end": v(0.01, -1.75) * mm});
            skLineSegment(sketch, "E1319", {"start": v(0.15, -1.7) * mm, "end": v(0.22, -1.7) * mm});
            skLineSegment(sketch, "E1320", {"start": v(0.22, -1.75) * mm, "end": v(0.15, -1.75) * mm});
            skLineSegment(sketch, "E1321", {"start": v(0.25, -1.7) * mm, "end": v(0.3, -1.7) * mm});
            skLineSegment(sketch, "E1322", {"start": v(0.3, -1.75) * mm, "end": v(0.25, -1.75) * mm});
            skLineSegment(sketch, "E1323", {"start": v(0.33, -1.7) * mm, "end": v(0.38, -1.7) * mm});
            skLineSegment(sketch, "E1324", {"start": v(0.38, -1.75) * mm, "end": v(0.33, -1.75) * mm});
            skLineSegment(sketch, "E1325", {"start": v(0.7, -1.77) * mm, "end": v(0.74, -1.77) * mm});
            skLineSegment(sketch, "E1326", {"start": v(0.7, -1.8) * mm, "end": v(0.74, -1.8) * mm});
            skLineSegment(sketch, "E1327", {"start": v(0.74, -1.77) * mm, "end": v(0.74, -1.8) * mm});
            skLineSegment(sketch, "E1328", {"start": v(0.7, -1.77) * mm, "end": v(0.7, -1.8) * mm});
            skLineSegment(sketch, "E1329", {"start": v(0.64, -1.77) * mm, "end": v(0.68, -1.77) * mm});
            skLineSegment(sketch, "E1330", {"start": v(0.64, -1.8) * mm, "end": v(0.68, -1.8) * mm});
            skLineSegment(sketch, "E1331", {"start": v(0.68, -1.77) * mm, "end": v(0.68, -1.8) * mm});
            skLineSegment(sketch, "E1332", {"start": v(0.64, -1.77) * mm, "end": v(0.64, -1.8) * mm});
            skLineSegment(sketch, "E1333", {"start": v(0.58, -1.77) * mm, "end": v(0.62, -1.77) * mm});
            skLineSegment(sketch, "E1334", {"start": v(0.58, -1.8) * mm, "end": v(0.62, -1.8) * mm});
            skLineSegment(sketch, "E1335", {"start": v(0.62, -1.77) * mm, "end": v(0.62, -1.8) * mm});
            skLineSegment(sketch, "E1336", {"start": v(0.58, -1.77) * mm, "end": v(0.58, -1.8) * mm});
            skLineSegment(sketch, "E1337", {"start": v(0.52, -1.77) * mm, "end": v(0.56, -1.77) * mm});
            skLineSegment(sketch, "E1338", {"start": v(0.52, -1.8) * mm, "end": v(0.56, -1.8) * mm});
            skLineSegment(sketch, "E1339", {"start": v(0.56, -1.77) * mm, "end": v(0.56, -1.8) * mm});
            skLineSegment(sketch, "E1340", {"start": v(0.52, -1.77) * mm, "end": v(0.52, -1.8) * mm});
            skLineSegment(sketch, "E1341", {"start": v(0.46, -1.77) * mm, "end": v(0.5, -1.77) * mm});
            skLineSegment(sketch, "E1342", {"start": v(0.46, -1.8) * mm, "end": v(0.5, -1.8) * mm});
            skLineSegment(sketch, "E1343", {"start": v(0.5, -1.77) * mm, "end": v(0.5, -1.8) * mm});
            skLineSegment(sketch, "E1344", {"start": v(0.46, -1.77) * mm, "end": v(0.46, -1.8) * mm});
            skLineSegment(sketch, "E1345", {"start": v(0.4, -1.77) * mm, "end": v(0.44, -1.77) * mm});
            skLineSegment(sketch, "E1346", {"start": v(0.4, -1.8) * mm, "end": v(0.44, -1.8) * mm});
            skLineSegment(sketch, "E1347", {"start": v(0.44, -1.77) * mm, "end": v(0.44, -1.8) * mm});
            skLineSegment(sketch, "E1348", {"start": v(0.4, -1.77) * mm, "end": v(0.4, -1.8) * mm});
            skLineSegment(sketch, "E1349", {"start": v(0.01, -1.77) * mm, "end": v(0.01, -1.8) * mm});
            skLineSegment(sketch, "E1350", {"start": v(0.38, -1.77) * mm, "end": v(0.38, -1.8) * mm});
            skLineSegment(sketch, "E1351", {"start": v(0.33, -1.77) * mm, "end": v(0.33, -1.8) * mm});
            skLineSegment(sketch, "E1352", {"start": v(0.3, -1.77) * mm, "end": v(0.3, -1.8) * mm});
            skLineSegment(sketch, "E1353", {"start": v(0.25, -1.77) * mm, "end": v(0.25, -1.8) * mm});
            skLineSegment(sketch, "E1354", {"start": v(0.22, -1.77) * mm, "end": v(0.22, -1.8) * mm});
            skLineSegment(sketch, "E1355", {"start": v(0.15, -1.77) * mm, "end": v(0.15, -1.8) * mm});
            skLineSegment(sketch, "E1356", {"start": v(0.13, -1.77) * mm, "end": v(0.13, -1.8) * mm});
            skLineSegment(sketch, "E1357", {"start": v(0.13, -1.77) * mm, "end": v(0.01, -1.77) * mm});
            skLineSegment(sketch, "E1358", {"start": v(0.13, -1.8) * mm, "end": v(0.01, -1.8) * mm});
            skLineSegment(sketch, "E1359", {"start": v(0.15, -1.77) * mm, "end": v(0.22, -1.77) * mm});
            skLineSegment(sketch, "E1360", {"start": v(0.22, -1.8) * mm, "end": v(0.15, -1.8) * mm});
            skLineSegment(sketch, "E1361", {"start": v(0.25, -1.77) * mm, "end": v(0.3, -1.77) * mm});
            skLineSegment(sketch, "E1362", {"start": v(0.3, -1.8) * mm, "end": v(0.25, -1.8) * mm});
            skLineSegment(sketch, "E1363", {"start": v(0.33, -1.77) * mm, "end": v(0.38, -1.77) * mm});
            skLineSegment(sketch, "E1364", {"start": v(0.38, -1.8) * mm, "end": v(0.33, -1.8) * mm});
            skLineSegment(sketch, "E1365", {"start": v(0.7, -1.83) * mm, "end": v(0.74, -1.83) * mm});
            skLineSegment(sketch, "E1366", {"start": v(0.7, -1.87) * mm, "end": v(0.74, -1.87) * mm});
            skLineSegment(sketch, "E1367", {"start": v(0.74, -1.83) * mm, "end": v(0.74, -1.87) * mm});
            skLineSegment(sketch, "E1368", {"start": v(0.7, -1.83) * mm, "end": v(0.7, -1.87) * mm});
            skLineSegment(sketch, "E1369", {"start": v(0.64, -1.83) * mm, "end": v(0.68, -1.83) * mm});
            skLineSegment(sketch, "E1370", {"start": v(0.64, -1.87) * mm, "end": v(0.68, -1.87) * mm});
            skLineSegment(sketch, "E1371", {"start": v(0.68, -1.83) * mm, "end": v(0.68, -1.87) * mm});
            skLineSegment(sketch, "E1372", {"start": v(0.64, -1.83) * mm, "end": v(0.64, -1.87) * mm});
            skLineSegment(sketch, "E1373", {"start": v(0.58, -1.83) * mm, "end": v(0.62, -1.83) * mm});
            skLineSegment(sketch, "E1374", {"start": v(0.58, -1.87) * mm, "end": v(0.62, -1.87) * mm});
            skLineSegment(sketch, "E1375", {"start": v(0.62, -1.83) * mm, "end": v(0.62, -1.87) * mm});
            skLineSegment(sketch, "E1376", {"start": v(0.58, -1.83) * mm, "end": v(0.58, -1.87) * mm});
            skLineSegment(sketch, "E1377", {"start": v(0.52, -1.83) * mm, "end": v(0.56, -1.83) * mm});
            skLineSegment(sketch, "E1378", {"start": v(0.52, -1.87) * mm, "end": v(0.56, -1.87) * mm});
            skLineSegment(sketch, "E1379", {"start": v(0.56, -1.83) * mm, "end": v(0.56, -1.87) * mm});
            skLineSegment(sketch, "E1380", {"start": v(0.52, -1.83) * mm, "end": v(0.52, -1.87) * mm});
            skLineSegment(sketch, "E1381", {"start": v(0.46, -1.83) * mm, "end": v(0.5, -1.83) * mm});
            skLineSegment(sketch, "E1382", {"start": v(0.46, -1.87) * mm, "end": v(0.5, -1.87) * mm});
            skLineSegment(sketch, "E1383", {"start": v(0.5, -1.83) * mm, "end": v(0.5, -1.87) * mm});
            skLineSegment(sketch, "E1384", {"start": v(0.46, -1.83) * mm, "end": v(0.46, -1.87) * mm});
            skLineSegment(sketch, "E1385", {"start": v(0.4, -1.83) * mm, "end": v(0.44, -1.83) * mm});
            skLineSegment(sketch, "E1386", {"start": v(0.4, -1.87) * mm, "end": v(0.44, -1.87) * mm});
            skLineSegment(sketch, "E1387", {"start": v(0.44, -1.83) * mm, "end": v(0.44, -1.87) * mm});
            skLineSegment(sketch, "E1388", {"start": v(0.4, -1.83) * mm, "end": v(0.4, -1.87) * mm});
            skLineSegment(sketch, "E1389", {"start": v(0.01, -1.83) * mm, "end": v(0.01, -1.87) * mm});
            skLineSegment(sketch, "E1390", {"start": v(0.38, -1.83) * mm, "end": v(0.38, -1.87) * mm});
            skLineSegment(sketch, "E1391", {"start": v(0.33, -1.83) * mm, "end": v(0.33, -1.87) * mm});
            skLineSegment(sketch, "E1392", {"start": v(0.3, -1.83) * mm, "end": v(0.3, -1.87) * mm});
            skLineSegment(sketch, "E1393", {"start": v(0.25, -1.83) * mm, "end": v(0.25, -1.87) * mm});
            skLineSegment(sketch, "E1394", {"start": v(0.22, -1.83) * mm, "end": v(0.22, -1.87) * mm});
            skLineSegment(sketch, "E1395", {"start": v(0.15, -1.83) * mm, "end": v(0.15, -1.87) * mm});
            skLineSegment(sketch, "E1396", {"start": v(0.13, -1.83) * mm, "end": v(0.13, -1.87) * mm});
            skLineSegment(sketch, "E1397", {"start": v(0.13, -1.83) * mm, "end": v(0.01, -1.83) * mm});
            skLineSegment(sketch, "E1398", {"start": v(0.13, -1.87) * mm, "end": v(0.01, -1.87) * mm});
            skLineSegment(sketch, "E1399", {"start": v(0.15, -1.83) * mm, "end": v(0.22, -1.83) * mm});
            skLineSegment(sketch, "E1400", {"start": v(0.22, -1.87) * mm, "end": v(0.15, -1.87) * mm});
            skLineSegment(sketch, "E1401", {"start": v(0.25, -1.83) * mm, "end": v(0.3, -1.83) * mm});
            skLineSegment(sketch, "E1402", {"start": v(0.3, -1.87) * mm, "end": v(0.25, -1.87) * mm});
            skLineSegment(sketch, "E1403", {"start": v(0.33, -1.83) * mm, "end": v(0.38, -1.83) * mm});
            skLineSegment(sketch, "E1404", {"start": v(0.38, -1.87) * mm, "end": v(0.33, -1.87) * mm});
            skLineSegment(sketch, "E1405", {"start": v(0.7, -1.89) * mm, "end": v(0.74, -1.89) * mm});
            skLineSegment(sketch, "E1406", {"start": v(0.7, -1.93) * mm, "end": v(0.74, -1.93) * mm});
            skLineSegment(sketch, "E1407", {"start": v(0.74, -1.89) * mm, "end": v(0.74, -1.93) * mm});
            skLineSegment(sketch, "E1408", {"start": v(0.7, -1.89) * mm, "end": v(0.7, -1.93) * mm});
            skLineSegment(sketch, "E1409", {"start": v(0.64, -1.89) * mm, "end": v(0.68, -1.89) * mm});
            skLineSegment(sketch, "E1410", {"start": v(0.64, -1.93) * mm, "end": v(0.68, -1.93) * mm});
            skLineSegment(sketch, "E1411", {"start": v(0.68, -1.89) * mm, "end": v(0.68, -1.93) * mm});
            skLineSegment(sketch, "E1412", {"start": v(0.64, -1.89) * mm, "end": v(0.64, -1.93) * mm});
            skLineSegment(sketch, "E1413", {"start": v(0.58, -1.89) * mm, "end": v(0.62, -1.89) * mm});
            skLineSegment(sketch, "E1414", {"start": v(0.58, -1.93) * mm, "end": v(0.62, -1.93) * mm});
            skLineSegment(sketch, "E1415", {"start": v(0.62, -1.89) * mm, "end": v(0.62, -1.93) * mm});
            skLineSegment(sketch, "E1416", {"start": v(0.58, -1.89) * mm, "end": v(0.58, -1.93) * mm});
            skLineSegment(sketch, "E1417", {"start": v(0.52, -1.89) * mm, "end": v(0.56, -1.89) * mm});
            skLineSegment(sketch, "E1418", {"start": v(0.52, -1.93) * mm, "end": v(0.56, -1.93) * mm});
            skLineSegment(sketch, "E1419", {"start": v(0.56, -1.89) * mm, "end": v(0.56, -1.93) * mm});
            skLineSegment(sketch, "E1420", {"start": v(0.52, -1.89) * mm, "end": v(0.52, -1.93) * mm});
            skLineSegment(sketch, "E1421", {"start": v(0.46, -1.89) * mm, "end": v(0.5, -1.89) * mm});
            skLineSegment(sketch, "E1422", {"start": v(0.46, -1.93) * mm, "end": v(0.5, -1.93) * mm});
            skLineSegment(sketch, "E1423", {"start": v(0.5, -1.89) * mm, "end": v(0.5, -1.93) * mm});
            skLineSegment(sketch, "E1424", {"start": v(0.46, -1.89) * mm, "end": v(0.46, -1.93) * mm});
            skLineSegment(sketch, "E1425", {"start": v(0.4, -1.89) * mm, "end": v(0.44, -1.89) * mm});
            skLineSegment(sketch, "E1426", {"start": v(0.4, -1.93) * mm, "end": v(0.44, -1.93) * mm});
            skLineSegment(sketch, "E1427", {"start": v(0.44, -1.89) * mm, "end": v(0.44, -1.93) * mm});
            skLineSegment(sketch, "E1428", {"start": v(0.4, -1.89) * mm, "end": v(0.4, -1.93) * mm});
            skLineSegment(sketch, "E1429", {"start": v(0.01, -1.89) * mm, "end": v(0.01, -1.93) * mm});
            skLineSegment(sketch, "E1430", {"start": v(0.38, -1.89) * mm, "end": v(0.38, -1.93) * mm});
            skLineSegment(sketch, "E1431", {"start": v(0.33, -1.89) * mm, "end": v(0.33, -1.93) * mm});
            skLineSegment(sketch, "E1432", {"start": v(0.3, -1.89) * mm, "end": v(0.3, -1.93) * mm});
            skLineSegment(sketch, "E1433", {"start": v(0.25, -1.89) * mm, "end": v(0.25, -1.93) * mm});
            skLineSegment(sketch, "E1434", {"start": v(0.22, -1.89) * mm, "end": v(0.22, -1.93) * mm});
            skLineSegment(sketch, "E1435", {"start": v(0.15, -1.89) * mm, "end": v(0.15, -1.93) * mm});
            skLineSegment(sketch, "E1436", {"start": v(0.13, -1.89) * mm, "end": v(0.13, -1.93) * mm});
            skLineSegment(sketch, "E1437", {"start": v(0.13, -1.89) * mm, "end": v(0.01, -1.89) * mm});
            skLineSegment(sketch, "E1438", {"start": v(0.13, -1.93) * mm, "end": v(0.01, -1.93) * mm});
            skLineSegment(sketch, "E1439", {"start": v(0.15, -1.89) * mm, "end": v(0.22, -1.89) * mm});
            skLineSegment(sketch, "E1440", {"start": v(0.22, -1.93) * mm, "end": v(0.15, -1.93) * mm});
            skLineSegment(sketch, "E1441", {"start": v(0.25, -1.89) * mm, "end": v(0.3, -1.89) * mm});
            skLineSegment(sketch, "E1442", {"start": v(0.3, -1.93) * mm, "end": v(0.25, -1.93) * mm});
            skLineSegment(sketch, "E1443", {"start": v(0.33, -1.89) * mm, "end": v(0.38, -1.89) * mm});
            skLineSegment(sketch, "E1444", {"start": v(0.38, -1.93) * mm, "end": v(0.33, -1.93) * mm});
            skLineSegment(sketch, "E1445", {"start": v(0.7, -1.95) * mm, "end": v(0.74, -1.95) * mm});
            skLineSegment(sketch, "E1446", {"start": v(0.7, -1.99) * mm, "end": v(0.74, -1.99) * mm});
            skLineSegment(sketch, "E1447", {"start": v(0.74, -1.95) * mm, "end": v(0.74, -1.99) * mm});
            skLineSegment(sketch, "E1448", {"start": v(0.7, -1.95) * mm, "end": v(0.7, -1.99) * mm});
            skLineSegment(sketch, "E1449", {"start": v(0.64, -1.95) * mm, "end": v(0.68, -1.95) * mm});
            skLineSegment(sketch, "E1450", {"start": v(0.64, -1.99) * mm, "end": v(0.68, -1.99) * mm});
            skLineSegment(sketch, "E1451", {"start": v(0.68, -1.95) * mm, "end": v(0.68, -1.99) * mm});
            skLineSegment(sketch, "E1452", {"start": v(0.64, -1.95) * mm, "end": v(0.64, -1.99) * mm});
            skLineSegment(sketch, "E1453", {"start": v(0.58, -1.95) * mm, "end": v(0.62, -1.95) * mm});
            skLineSegment(sketch, "E1454", {"start": v(0.58, -1.99) * mm, "end": v(0.62, -1.99) * mm});
            skLineSegment(sketch, "E1455", {"start": v(0.62, -1.95) * mm, "end": v(0.62, -1.99) * mm});
            skLineSegment(sketch, "E1456", {"start": v(0.58, -1.95) * mm, "end": v(0.58, -1.99) * mm});
            skLineSegment(sketch, "E1457", {"start": v(0.52, -1.95) * mm, "end": v(0.56, -1.95) * mm});
            skLineSegment(sketch, "E1458", {"start": v(0.52, -1.99) * mm, "end": v(0.56, -1.99) * mm});
            skLineSegment(sketch, "E1459", {"start": v(0.56, -1.95) * mm, "end": v(0.56, -1.99) * mm});
            skLineSegment(sketch, "E1460", {"start": v(0.52, -1.95) * mm, "end": v(0.52, -1.99) * mm});
            skLineSegment(sketch, "E1461", {"start": v(0.46, -1.95) * mm, "end": v(0.5, -1.95) * mm});
            skLineSegment(sketch, "E1462", {"start": v(0.46, -1.99) * mm, "end": v(0.5, -1.99) * mm});
            skLineSegment(sketch, "E1463", {"start": v(0.5, -1.95) * mm, "end": v(0.5, -1.99) * mm});
            skLineSegment(sketch, "E1464", {"start": v(0.46, -1.95) * mm, "end": v(0.46, -1.99) * mm});
            skLineSegment(sketch, "E1465", {"start": v(0.4, -1.95) * mm, "end": v(0.44, -1.95) * mm});
            skLineSegment(sketch, "E1466", {"start": v(0.4, -1.99) * mm, "end": v(0.44, -1.99) * mm});
            skLineSegment(sketch, "E1467", {"start": v(0.44, -1.95) * mm, "end": v(0.44, -1.99) * mm});
            skLineSegment(sketch, "E1468", {"start": v(0.4, -1.95) * mm, "end": v(0.4, -1.99) * mm});
            skLineSegment(sketch, "E1469", {"start": v(0.01, -1.95) * mm, "end": v(0.01, -1.99) * mm});
            skLineSegment(sketch, "E1470", {"start": v(0.38, -1.95) * mm, "end": v(0.38, -1.99) * mm});
            skLineSegment(sketch, "E1471", {"start": v(0.33, -1.95) * mm, "end": v(0.33, -1.99) * mm});
            skLineSegment(sketch, "E1472", {"start": v(0.3, -1.95) * mm, "end": v(0.3, -1.99) * mm});
            skLineSegment(sketch, "E1473", {"start": v(0.25, -1.95) * mm, "end": v(0.25, -1.99) * mm});
            skLineSegment(sketch, "E1474", {"start": v(0.22, -1.95) * mm, "end": v(0.22, -1.99) * mm});
            skLineSegment(sketch, "E1475", {"start": v(0.15, -1.95) * mm, "end": v(0.15, -1.99) * mm});
            skLineSegment(sketch, "E1476", {"start": v(0.13, -1.95) * mm, "end": v(0.13, -1.99) * mm});
            skLineSegment(sketch, "E1477", {"start": v(0.13, -1.95) * mm, "end": v(0.01, -1.95) * mm});
            skLineSegment(sketch, "E1478", {"start": v(0.13, -1.99) * mm, "end": v(0.01, -1.99) * mm});
            skLineSegment(sketch, "E1479", {"start": v(0.15, -1.95) * mm, "end": v(0.22, -1.95) * mm});
            skLineSegment(sketch, "E1480", {"start": v(0.22, -1.99) * mm, "end": v(0.15, -1.99) * mm});
            skLineSegment(sketch, "E1481", {"start": v(0.25, -1.95) * mm, "end": v(0.3, -1.95) * mm});
            skLineSegment(sketch, "E1482", {"start": v(0.3, -1.99) * mm, "end": v(0.25, -1.99) * mm});
            skLineSegment(sketch, "E1483", {"start": v(0.33, -1.95) * mm, "end": v(0.38, -1.95) * mm});
            skLineSegment(sketch, "E1484", {"start": v(0.38, -1.99) * mm, "end": v(0.33, -1.99) * mm});
            skLineSegment(sketch, "E1485", {"start": v(0.7, -2) * mm, "end": v(0.74, -2) * mm});
            skLineSegment(sketch, "E1486", {"start": v(0.7, -2.05) * mm, "end": v(0.74, -2.05) * mm});
            skLineSegment(sketch, "E1487", {"start": v(0.74, -2) * mm, "end": v(0.74, -2.05) * mm});
            skLineSegment(sketch, "E1488", {"start": v(0.7, -2) * mm, "end": v(0.7, -2.05) * mm});
            skLineSegment(sketch, "E1489", {"start": v(0.64, -2) * mm, "end": v(0.68, -2) * mm});
            skLineSegment(sketch, "E1490", {"start": v(0.64, -2.05) * mm, "end": v(0.68, -2.05) * mm});
            skLineSegment(sketch, "E1491", {"start": v(0.68, -2) * mm, "end": v(0.68, -2.05) * mm});
            skLineSegment(sketch, "E1492", {"start": v(0.64, -2) * mm, "end": v(0.64, -2.05) * mm});
            skLineSegment(sketch, "E1493", {"start": v(0.58, -2) * mm, "end": v(0.62, -2) * mm});
            skLineSegment(sketch, "E1494", {"start": v(0.58, -2.05) * mm, "end": v(0.62, -2.05) * mm});
            skLineSegment(sketch, "E1495", {"start": v(0.62, -2) * mm, "end": v(0.62, -2.05) * mm});
            skLineSegment(sketch, "E1496", {"start": v(0.58, -2) * mm, "end": v(0.58, -2.05) * mm});
            skLineSegment(sketch, "E1497", {"start": v(0.52, -2) * mm, "end": v(0.56, -2) * mm});
            skLineSegment(sketch, "E1498", {"start": v(0.52, -2.05) * mm, "end": v(0.56, -2.05) * mm});
            skLineSegment(sketch, "E1499", {"start": v(0.56, -2) * mm, "end": v(0.56, -2.05) * mm});
            skLineSegment(sketch, "E1500", {"start": v(0.52, -2) * mm, "end": v(0.52, -2.05) * mm});
            skLineSegment(sketch, "E1501", {"start": v(0.46, -2) * mm, "end": v(0.5, -2) * mm});
            skLineSegment(sketch, "E1502", {"start": v(0.46, -2.05) * mm, "end": v(0.5, -2.05) * mm});
            skLineSegment(sketch, "E1503", {"start": v(0.5, -2) * mm, "end": v(0.5, -2.05) * mm});
            skLineSegment(sketch, "E1504", {"start": v(0.46, -2) * mm, "end": v(0.46, -2.05) * mm});
            skLineSegment(sketch, "E1505", {"start": v(0.4, -2) * mm, "end": v(0.44, -2) * mm});
            skLineSegment(sketch, "E1506", {"start": v(0.4, -2.05) * mm, "end": v(0.44, -2.05) * mm});
            skLineSegment(sketch, "E1507", {"start": v(0.44, -2) * mm, "end": v(0.44, -2.05) * mm});
            skLineSegment(sketch, "E1508", {"start": v(0.4, -2) * mm, "end": v(0.4, -2.05) * mm});
            skLineSegment(sketch, "E1509", {"start": v(0.01, -2) * mm, "end": v(0.01, -2.05) * mm});
            skLineSegment(sketch, "E1510", {"start": v(0.38, -2) * mm, "end": v(0.38, -2.05) * mm});
            skLineSegment(sketch, "E1511", {"start": v(0.33, -2) * mm, "end": v(0.33, -2.05) * mm});
            skLineSegment(sketch, "E1512", {"start": v(0.3, -2) * mm, "end": v(0.3, -2.05) * mm});
            skLineSegment(sketch, "E1513", {"start": v(0.25, -2) * mm, "end": v(0.25, -2.05) * mm});
            skLineSegment(sketch, "E1514", {"start": v(0.22, -2) * mm, "end": v(0.22, -2.05) * mm});
            skLineSegment(sketch, "E1515", {"start": v(0.15, -2) * mm, "end": v(0.15, -2.05) * mm});
            skLineSegment(sketch, "E1516", {"start": v(0.13, -2) * mm, "end": v(0.13, -2.05) * mm});
            skLineSegment(sketch, "E1517", {"start": v(0.13, -2) * mm, "end": v(0.01, -2) * mm});
            skLineSegment(sketch, "E1518", {"start": v(0.13, -2.05) * mm, "end": v(0.01, -2.05) * mm});
            skLineSegment(sketch, "E1519", {"start": v(0.15, -2) * mm, "end": v(0.22, -2) * mm});
            skLineSegment(sketch, "E1520", {"start": v(0.22, -2.05) * mm, "end": v(0.15, -2.05) * mm});
            skLineSegment(sketch, "E1521", {"start": v(0.25, -2) * mm, "end": v(0.3, -2) * mm});
            skLineSegment(sketch, "E1522", {"start": v(0.3, -2.05) * mm, "end": v(0.25, -2.05) * mm});
            skLineSegment(sketch, "E1523", {"start": v(0.33, -2) * mm, "end": v(0.38, -2) * mm});
            skLineSegment(sketch, "E1524", {"start": v(0.38, -2.05) * mm, "end": v(0.33, -2.05) * mm});
            skLineSegment(sketch, "E1525", {"start": v(0.7, -2.07) * mm, "end": v(0.74, -2.07) * mm});
            skLineSegment(sketch, "E1526", {"start": v(0.7, -2.1) * mm, "end": v(0.74, -2.1) * mm});
            skLineSegment(sketch, "E1527", {"start": v(0.74, -2.07) * mm, "end": v(0.74, -2.1) * mm});
            skLineSegment(sketch, "E1528", {"start": v(0.7, -2.07) * mm, "end": v(0.7, -2.1) * mm});
            skLineSegment(sketch, "E1529", {"start": v(0.64, -2.07) * mm, "end": v(0.68, -2.07) * mm});
            skLineSegment(sketch, "E1530", {"start": v(0.64, -2.1) * mm, "end": v(0.68, -2.1) * mm});
            skLineSegment(sketch, "E1531", {"start": v(0.68, -2.07) * mm, "end": v(0.68, -2.1) * mm});
            skLineSegment(sketch, "E1532", {"start": v(0.64, -2.07) * mm, "end": v(0.64, -2.1) * mm});
            skLineSegment(sketch, "E1533", {"start": v(0.58, -2.07) * mm, "end": v(0.62, -2.07) * mm});
            skLineSegment(sketch, "E1534", {"start": v(0.58, -2.1) * mm, "end": v(0.62, -2.1) * mm});
            skLineSegment(sketch, "E1535", {"start": v(0.62, -2.07) * mm, "end": v(0.62, -2.1) * mm});
            skLineSegment(sketch, "E1536", {"start": v(0.58, -2.07) * mm, "end": v(0.58, -2.1) * mm});
            skLineSegment(sketch, "E1537", {"start": v(0.52, -2.07) * mm, "end": v(0.56, -2.07) * mm});
            skLineSegment(sketch, "E1538", {"start": v(0.52, -2.1) * mm, "end": v(0.56, -2.1) * mm});
            skLineSegment(sketch, "E1539", {"start": v(0.56, -2.07) * mm, "end": v(0.56, -2.1) * mm});
            skLineSegment(sketch, "E1540", {"start": v(0.52, -2.07) * mm, "end": v(0.52, -2.1) * mm});
            skLineSegment(sketch, "E1541", {"start": v(0.46, -2.07) * mm, "end": v(0.5, -2.07) * mm});
            skLineSegment(sketch, "E1542", {"start": v(0.46, -2.1) * mm, "end": v(0.5, -2.1) * mm});
            skLineSegment(sketch, "E1543", {"start": v(0.5, -2.07) * mm, "end": v(0.5, -2.1) * mm});
            skLineSegment(sketch, "E1544", {"start": v(0.46, -2.07) * mm, "end": v(0.46, -2.1) * mm});
            skLineSegment(sketch, "E1545", {"start": v(0.4, -2.07) * mm, "end": v(0.44, -2.07) * mm});
            skLineSegment(sketch, "E1546", {"start": v(0.4, -2.1) * mm, "end": v(0.44, -2.1) * mm});
            skLineSegment(sketch, "E1547", {"start": v(0.44, -2.07) * mm, "end": v(0.44, -2.1) * mm});
            skLineSegment(sketch, "E1548", {"start": v(0.4, -2.07) * mm, "end": v(0.4, -2.1) * mm});
            skLineSegment(sketch, "E1549", {"start": v(0.01, -2.07) * mm, "end": v(0.01, -2.1) * mm});
            skLineSegment(sketch, "E1550", {"start": v(0.38, -2.07) * mm, "end": v(0.38, -2.1) * mm});
            skLineSegment(sketch, "E1551", {"start": v(0.33, -2.07) * mm, "end": v(0.33, -2.1) * mm});
            skLineSegment(sketch, "E1552", {"start": v(0.3, -2.07) * mm, "end": v(0.3, -2.1) * mm});
            skLineSegment(sketch, "E1553", {"start": v(0.25, -2.07) * mm, "end": v(0.25, -2.1) * mm});
            skLineSegment(sketch, "E1554", {"start": v(0.22, -2.07) * mm, "end": v(0.22, -2.1) * mm});
            skLineSegment(sketch, "E1555", {"start": v(0.15, -2.07) * mm, "end": v(0.15, -2.1) * mm});
            skLineSegment(sketch, "E1556", {"start": v(0.13, -2.07) * mm, "end": v(0.13, -2.1) * mm});
            skLineSegment(sketch, "E1557", {"start": v(0.13, -2.07) * mm, "end": v(0.01, -2.07) * mm});
            skLineSegment(sketch, "E1558", {"start": v(0.13, -2.1) * mm, "end": v(0.01, -2.1) * mm});
            skLineSegment(sketch, "E1559", {"start": v(0.15, -2.07) * mm, "end": v(0.22, -2.07) * mm});
            skLineSegment(sketch, "E1560", {"start": v(0.22, -2.1) * mm, "end": v(0.15, -2.1) * mm});
            skLineSegment(sketch, "E1561", {"start": v(0.25, -2.07) * mm, "end": v(0.3, -2.07) * mm});
            skLineSegment(sketch, "E1562", {"start": v(0.3, -2.1) * mm, "end": v(0.25, -2.1) * mm});
            skLineSegment(sketch, "E1563", {"start": v(0.33, -2.07) * mm, "end": v(0.38, -2.07) * mm});
            skLineSegment(sketch, "E1564", {"start": v(0.38, -2.1) * mm, "end": v(0.33, -2.1) * mm});
            skLineSegment(sketch, "E1565", {"start": v(0.7, -2.13) * mm, "end": v(0.74, -2.13) * mm});
            skLineSegment(sketch, "E1566", {"start": v(0.7, -2.17) * mm, "end": v(0.74, -2.17) * mm});
            skLineSegment(sketch, "E1567", {"start": v(0.74, -2.13) * mm, "end": v(0.74, -2.17) * mm});
            skLineSegment(sketch, "E1568", {"start": v(0.7, -2.13) * mm, "end": v(0.7, -2.17) * mm});
            skLineSegment(sketch, "E1569", {"start": v(0.64, -2.13) * mm, "end": v(0.68, -2.13) * mm});
            skLineSegment(sketch, "E1570", {"start": v(0.64, -2.17) * mm, "end": v(0.68, -2.17) * mm});
            skLineSegment(sketch, "E1571", {"start": v(0.68, -2.13) * mm, "end": v(0.68, -2.17) * mm});
            skLineSegment(sketch, "E1572", {"start": v(0.64, -2.13) * mm, "end": v(0.64, -2.17) * mm});
            skLineSegment(sketch, "E1573", {"start": v(0.58, -2.13) * mm, "end": v(0.62, -2.13) * mm});
            skLineSegment(sketch, "E1574", {"start": v(0.58, -2.17) * mm, "end": v(0.62, -2.17) * mm});
            skLineSegment(sketch, "E1575", {"start": v(0.62, -2.13) * mm, "end": v(0.62, -2.17) * mm});
            skLineSegment(sketch, "E1576", {"start": v(0.58, -2.13) * mm, "end": v(0.58, -2.17) * mm});
            skLineSegment(sketch, "E1577", {"start": v(0.52, -2.13) * mm, "end": v(0.56, -2.13) * mm});
            skLineSegment(sketch, "E1578", {"start": v(0.52, -2.17) * mm, "end": v(0.56, -2.17) * mm});
            skLineSegment(sketch, "E1579", {"start": v(0.56, -2.13) * mm, "end": v(0.56, -2.17) * mm});
            skLineSegment(sketch, "E1580", {"start": v(0.52, -2.13) * mm, "end": v(0.52, -2.17) * mm});
            skLineSegment(sketch, "E1581", {"start": v(0.46, -2.13) * mm, "end": v(0.5, -2.13) * mm});
            skLineSegment(sketch, "E1582", {"start": v(0.46, -2.17) * mm, "end": v(0.5, -2.17) * mm});
            skLineSegment(sketch, "E1583", {"start": v(0.5, -2.13) * mm, "end": v(0.5, -2.17) * mm});
            skLineSegment(sketch, "E1584", {"start": v(0.46, -2.13) * mm, "end": v(0.46, -2.17) * mm});
            skLineSegment(sketch, "E1585", {"start": v(0.4, -2.13) * mm, "end": v(0.44, -2.13) * mm});
            skLineSegment(sketch, "E1586", {"start": v(0.4, -2.17) * mm, "end": v(0.44, -2.17) * mm});
            skLineSegment(sketch, "E1587", {"start": v(0.44, -2.13) * mm, "end": v(0.44, -2.17) * mm});
            skLineSegment(sketch, "E1588", {"start": v(0.4, -2.13) * mm, "end": v(0.4, -2.17) * mm});
            skLineSegment(sketch, "E1589", {"start": v(0.01, -2.13) * mm, "end": v(0.01, -2.17) * mm});
            skLineSegment(sketch, "E1590", {"start": v(0.38, -2.13) * mm, "end": v(0.38, -2.17) * mm});
            skLineSegment(sketch, "E1591", {"start": v(0.33, -2.13) * mm, "end": v(0.33, -2.17) * mm});
            skLineSegment(sketch, "E1592", {"start": v(0.3, -2.13) * mm, "end": v(0.3, -2.17) * mm});
            skLineSegment(sketch, "E1593", {"start": v(0.25, -2.13) * mm, "end": v(0.25, -2.17) * mm});
            skLineSegment(sketch, "E1594", {"start": v(0.22, -2.13) * mm, "end": v(0.22, -2.17) * mm});
            skLineSegment(sketch, "E1595", {"start": v(0.15, -2.13) * mm, "end": v(0.15, -2.17) * mm});
            skLineSegment(sketch, "E1596", {"start": v(0.13, -2.13) * mm, "end": v(0.13, -2.17) * mm});
            skLineSegment(sketch, "E1597", {"start": v(0.13, -2.13) * mm, "end": v(0.01, -2.13) * mm});
            skLineSegment(sketch, "E1598", {"start": v(0.13, -2.17) * mm, "end": v(0.01, -2.17) * mm});
            skLineSegment(sketch, "E1599", {"start": v(0.15, -2.13) * mm, "end": v(0.22, -2.13) * mm});
            skLineSegment(sketch, "E1600", {"start": v(0.22, -2.17) * mm, "end": v(0.15, -2.17) * mm});
            skLineSegment(sketch, "E1601", {"start": v(0.25, -2.13) * mm, "end": v(0.3, -2.13) * mm});
            skLineSegment(sketch, "E1602", {"start": v(0.3, -2.17) * mm, "end": v(0.25, -2.17) * mm});
            skLineSegment(sketch, "E1603", {"start": v(0.33, -2.13) * mm, "end": v(0.38, -2.13) * mm});
            skLineSegment(sketch, "E1604", {"start": v(0.38, -2.17) * mm, "end": v(0.33, -2.17) * mm});
            skLineSegment(sketch, "E1605", {"start": v(0.7, -2.19) * mm, "end": v(0.74, -2.19) * mm});
            skLineSegment(sketch, "E1606", {"start": v(0.7, -2.23) * mm, "end": v(0.74, -2.23) * mm});
            skLineSegment(sketch, "E1607", {"start": v(0.74, -2.19) * mm, "end": v(0.74, -2.23) * mm});
            skLineSegment(sketch, "E1608", {"start": v(0.7, -2.19) * mm, "end": v(0.7, -2.23) * mm});
            skLineSegment(sketch, "E1609", {"start": v(0.64, -2.19) * mm, "end": v(0.68, -2.19) * mm});
            skLineSegment(sketch, "E1610", {"start": v(0.64, -2.23) * mm, "end": v(0.68, -2.23) * mm});
            skLineSegment(sketch, "E1611", {"start": v(0.68, -2.19) * mm, "end": v(0.68, -2.23) * mm});
            skLineSegment(sketch, "E1612", {"start": v(0.64, -2.19) * mm, "end": v(0.64, -2.23) * mm});
            skLineSegment(sketch, "E1613", {"start": v(0.58, -2.19) * mm, "end": v(0.62, -2.19) * mm});
            skLineSegment(sketch, "E1614", {"start": v(0.58, -2.23) * mm, "end": v(0.62, -2.23) * mm});
            skLineSegment(sketch, "E1615", {"start": v(0.62, -2.19) * mm, "end": v(0.62, -2.23) * mm});
            skLineSegment(sketch, "E1616", {"start": v(0.58, -2.19) * mm, "end": v(0.58, -2.23) * mm});
            skLineSegment(sketch, "E1617", {"start": v(0.52, -2.19) * mm, "end": v(0.56, -2.19) * mm});
            skLineSegment(sketch, "E1618", {"start": v(0.52, -2.23) * mm, "end": v(0.56, -2.23) * mm});
            skLineSegment(sketch, "E1619", {"start": v(0.56, -2.19) * mm, "end": v(0.56, -2.23) * mm});
            skLineSegment(sketch, "E1620", {"start": v(0.52, -2.19) * mm, "end": v(0.52, -2.23) * mm});
            skLineSegment(sketch, "E1621", {"start": v(0.46, -2.19) * mm, "end": v(0.5, -2.19) * mm});
            skLineSegment(sketch, "E1622", {"start": v(0.46, -2.23) * mm, "end": v(0.5, -2.23) * mm});
            skLineSegment(sketch, "E1623", {"start": v(0.5, -2.19) * mm, "end": v(0.5, -2.23) * mm});
            skLineSegment(sketch, "E1624", {"start": v(0.46, -2.19) * mm, "end": v(0.46, -2.23) * mm});
            skLineSegment(sketch, "E1625", {"start": v(0.4, -2.19) * mm, "end": v(0.44, -2.19) * mm});
            skLineSegment(sketch, "E1626", {"start": v(0.4, -2.23) * mm, "end": v(0.44, -2.23) * mm});
            skLineSegment(sketch, "E1627", {"start": v(0.44, -2.19) * mm, "end": v(0.44, -2.23) * mm});
            skLineSegment(sketch, "E1628", {"start": v(0.4, -2.19) * mm, "end": v(0.4, -2.23) * mm});
            skLineSegment(sketch, "E1629", {"start": v(0.01, -2.19) * mm, "end": v(0.01, -2.23) * mm});
            skLineSegment(sketch, "E1630", {"start": v(0.38, -2.19) * mm, "end": v(0.38, -2.23) * mm});
            skLineSegment(sketch, "E1631", {"start": v(0.33, -2.19) * mm, "end": v(0.33, -2.23) * mm});
            skLineSegment(sketch, "E1632", {"start": v(0.3, -2.19) * mm, "end": v(0.3, -2.23) * mm});
            skLineSegment(sketch, "E1633", {"start": v(0.25, -2.19) * mm, "end": v(0.25, -2.23) * mm});
            skLineSegment(sketch, "E1634", {"start": v(0.22, -2.19) * mm, "end": v(0.22, -2.23) * mm});
            skLineSegment(sketch, "E1635", {"start": v(0.15, -2.19) * mm, "end": v(0.15, -2.23) * mm});
            skLineSegment(sketch, "E1636", {"start": v(0.13, -2.19) * mm, "end": v(0.13, -2.23) * mm});
            skLineSegment(sketch, "E1637", {"start": v(0.13, -2.19) * mm, "end": v(0.01, -2.19) * mm});
            skLineSegment(sketch, "E1638", {"start": v(0.13, -2.23) * mm, "end": v(0.01, -2.23) * mm});
            skLineSegment(sketch, "E1639", {"start": v(0.15, -2.19) * mm, "end": v(0.22, -2.19) * mm});
            skLineSegment(sketch, "E1640", {"start": v(0.22, -2.23) * mm, "end": v(0.15, -2.23) * mm});
            skLineSegment(sketch, "E1641", {"start": v(0.25, -2.19) * mm, "end": v(0.3, -2.19) * mm});
            skLineSegment(sketch, "E1642", {"start": v(0.3, -2.23) * mm, "end": v(0.25, -2.23) * mm});
            skLineSegment(sketch, "E1643", {"start": v(0.33, -2.19) * mm, "end": v(0.38, -2.19) * mm});
            skLineSegment(sketch, "E1644", {"start": v(0.38, -2.23) * mm, "end": v(0.33, -2.23) * mm});
            skLineSegment(sketch, "E1645", {"start": v(0.7, -2.25) * mm, "end": v(0.74, -2.25) * mm});
            skLineSegment(sketch, "E1646", {"start": v(0.7, -2.29) * mm, "end": v(0.74, -2.29) * mm});
            skLineSegment(sketch, "E1647", {"start": v(0.74, -2.25) * mm, "end": v(0.74, -2.29) * mm});
            skLineSegment(sketch, "E1648", {"start": v(0.7, -2.25) * mm, "end": v(0.7, -2.29) * mm});
            skLineSegment(sketch, "E1649", {"start": v(0.64, -2.25) * mm, "end": v(0.68, -2.25) * mm});
            skLineSegment(sketch, "E1650", {"start": v(0.64, -2.29) * mm, "end": v(0.68, -2.29) * mm});
            skLineSegment(sketch, "E1651", {"start": v(0.68, -2.25) * mm, "end": v(0.68, -2.29) * mm});
            skLineSegment(sketch, "E1652", {"start": v(0.64, -2.25) * mm, "end": v(0.64, -2.29) * mm});
            skLineSegment(sketch, "E1653", {"start": v(0.58, -2.25) * mm, "end": v(0.62, -2.25) * mm});
            skLineSegment(sketch, "E1654", {"start": v(0.58, -2.29) * mm, "end": v(0.62, -2.29) * mm});
            skLineSegment(sketch, "E1655", {"start": v(0.62, -2.25) * mm, "end": v(0.62, -2.29) * mm});
            skLineSegment(sketch, "E1656", {"start": v(0.58, -2.25) * mm, "end": v(0.58, -2.29) * mm});
            skLineSegment(sketch, "E1657", {"start": v(0.52, -2.25) * mm, "end": v(0.56, -2.25) * mm});
            skLineSegment(sketch, "E1658", {"start": v(0.52, -2.29) * mm, "end": v(0.56, -2.29) * mm});
            skLineSegment(sketch, "E1659", {"start": v(0.56, -2.25) * mm, "end": v(0.56, -2.29) * mm});
            skLineSegment(sketch, "E1660", {"start": v(0.52, -2.25) * mm, "end": v(0.52, -2.29) * mm});
            skLineSegment(sketch, "E1661", {"start": v(0.46, -2.25) * mm, "end": v(0.5, -2.25) * mm});
            skLineSegment(sketch, "E1662", {"start": v(0.46, -2.29) * mm, "end": v(0.5, -2.29) * mm});
            skLineSegment(sketch, "E1663", {"start": v(0.5, -2.25) * mm, "end": v(0.5, -2.29) * mm});
            skLineSegment(sketch, "E1664", {"start": v(0.46, -2.25) * mm, "end": v(0.46, -2.29) * mm});
            skLineSegment(sketch, "E1665", {"start": v(0.4, -2.25) * mm, "end": v(0.44, -2.25) * mm});
            skLineSegment(sketch, "E1666", {"start": v(0.4, -2.29) * mm, "end": v(0.44, -2.29) * mm});
            skLineSegment(sketch, "E1667", {"start": v(0.44, -2.25) * mm, "end": v(0.44, -2.29) * mm});
            skLineSegment(sketch, "E1668", {"start": v(0.4, -2.25) * mm, "end": v(0.4, -2.29) * mm});
            skLineSegment(sketch, "E1669", {"start": v(0.01, -2.25) * mm, "end": v(0.01, -2.29) * mm});
            skLineSegment(sketch, "E1670", {"start": v(0.38, -2.25) * mm, "end": v(0.38, -2.29) * mm});
            skLineSegment(sketch, "E1671", {"start": v(0.33, -2.25) * mm, "end": v(0.33, -2.29) * mm});
            skLineSegment(sketch, "E1672", {"start": v(0.3, -2.25) * mm, "end": v(0.3, -2.29) * mm});
            skLineSegment(sketch, "E1673", {"start": v(0.25, -2.25) * mm, "end": v(0.25, -2.29) * mm});
            skLineSegment(sketch, "E1674", {"start": v(0.22, -2.25) * mm, "end": v(0.22, -2.29) * mm});
            skLineSegment(sketch, "E1675", {"start": v(0.15, -2.25) * mm, "end": v(0.15, -2.29) * mm});
            skLineSegment(sketch, "E1676", {"start": v(0.13, -2.25) * mm, "end": v(0.13, -2.29) * mm});
            skLineSegment(sketch, "E1677", {"start": v(0.13, -2.25) * mm, "end": v(0.01, -2.25) * mm});
            skLineSegment(sketch, "E1678", {"start": v(0.13, -2.29) * mm, "end": v(0.01, -2.29) * mm});
            skLineSegment(sketch, "E1679", {"start": v(0.15, -2.25) * mm, "end": v(0.22, -2.25) * mm});
            skLineSegment(sketch, "E1680", {"start": v(0.22, -2.29) * mm, "end": v(0.15, -2.29) * mm});
            skLineSegment(sketch, "E1681", {"start": v(0.25, -2.25) * mm, "end": v(0.3, -2.25) * mm});
            skLineSegment(sketch, "E1682", {"start": v(0.3, -2.29) * mm, "end": v(0.25, -2.29) * mm});
            skLineSegment(sketch, "E1683", {"start": v(0.33, -2.25) * mm, "end": v(0.38, -2.25) * mm});
            skLineSegment(sketch, "E1684", {"start": v(0.38, -2.29) * mm, "end": v(0.33, -2.29) * mm});
            skLineSegment(sketch, "E1685", {"start": v(0.7, -2.3) * mm, "end": v(0.74, -2.3) * mm});
            skLineSegment(sketch, "E1686", {"start": v(0.7, -2.35) * mm, "end": v(0.74, -2.35) * mm});
            skLineSegment(sketch, "E1687", {"start": v(0.74, -2.3) * mm, "end": v(0.74, -2.35) * mm});
            skLineSegment(sketch, "E1688", {"start": v(0.7, -2.3) * mm, "end": v(0.7, -2.35) * mm});
            skLineSegment(sketch, "E1689", {"start": v(0.64, -2.3) * mm, "end": v(0.68, -2.3) * mm});
            skLineSegment(sketch, "E1690", {"start": v(0.64, -2.35) * mm, "end": v(0.68, -2.35) * mm});
            skLineSegment(sketch, "E1691", {"start": v(0.68, -2.3) * mm, "end": v(0.68, -2.35) * mm});
            skLineSegment(sketch, "E1692", {"start": v(0.64, -2.3) * mm, "end": v(0.64, -2.35) * mm});
            skLineSegment(sketch, "E1693", {"start": v(0.58, -2.3) * mm, "end": v(0.62, -2.3) * mm});
            skLineSegment(sketch, "E1694", {"start": v(0.58, -2.35) * mm, "end": v(0.62, -2.35) * mm});
            skLineSegment(sketch, "E1695", {"start": v(0.62, -2.3) * mm, "end": v(0.62, -2.35) * mm});
            skLineSegment(sketch, "E1696", {"start": v(0.58, -2.3) * mm, "end": v(0.58, -2.35) * mm});
            skLineSegment(sketch, "E1697", {"start": v(0.52, -2.3) * mm, "end": v(0.56, -2.3) * mm});
            skLineSegment(sketch, "E1698", {"start": v(0.52, -2.35) * mm, "end": v(0.56, -2.35) * mm});
            skLineSegment(sketch, "E1699", {"start": v(0.56, -2.3) * mm, "end": v(0.56, -2.35) * mm});
            skLineSegment(sketch, "E1700", {"start": v(0.52, -2.3) * mm, "end": v(0.52, -2.35) * mm});
            skLineSegment(sketch, "E1701", {"start": v(0.46, -2.3) * mm, "end": v(0.5, -2.3) * mm});
            skLineSegment(sketch, "E1702", {"start": v(0.46, -2.35) * mm, "end": v(0.5, -2.35) * mm});
            skLineSegment(sketch, "E1703", {"start": v(0.5, -2.3) * mm, "end": v(0.5, -2.35) * mm});
            skLineSegment(sketch, "E1704", {"start": v(0.46, -2.3) * mm, "end": v(0.46, -2.35) * mm});
            skLineSegment(sketch, "E1705", {"start": v(0.4, -2.3) * mm, "end": v(0.44, -2.3) * mm});
            skLineSegment(sketch, "E1706", {"start": v(0.4, -2.35) * mm, "end": v(0.44, -2.35) * mm});
            skLineSegment(sketch, "E1707", {"start": v(0.44, -2.3) * mm, "end": v(0.44, -2.35) * mm});
            skLineSegment(sketch, "E1708", {"start": v(0.4, -2.3) * mm, "end": v(0.4, -2.35) * mm});
            skLineSegment(sketch, "E1709", {"start": v(0.01, -2.3) * mm, "end": v(0.01, -2.35) * mm});
            skLineSegment(sketch, "E1710", {"start": v(0.38, -2.3) * mm, "end": v(0.38, -2.35) * mm});
            skLineSegment(sketch, "E1711", {"start": v(0.33, -2.3) * mm, "end": v(0.33, -2.35) * mm});
            skLineSegment(sketch, "E1712", {"start": v(0.3, -2.3) * mm, "end": v(0.3, -2.35) * mm});
            skLineSegment(sketch, "E1713", {"start": v(0.25, -2.3) * mm, "end": v(0.25, -2.35) * mm});
            skLineSegment(sketch, "E1714", {"start": v(0.22, -2.3) * mm, "end": v(0.22, -2.35) * mm});
            skLineSegment(sketch, "E1715", {"start": v(0.15, -2.3) * mm, "end": v(0.15, -2.35) * mm});
            skLineSegment(sketch, "E1716", {"start": v(0.13, -2.3) * mm, "end": v(0.13, -2.35) * mm});
            skLineSegment(sketch, "E1717", {"start": v(0.13, -2.3) * mm, "end": v(0.01, -2.3) * mm});
            skLineSegment(sketch, "E1718", {"start": v(0.13, -2.35) * mm, "end": v(0.01, -2.35) * mm});
            skLineSegment(sketch, "E1719", {"start": v(0.15, -2.3) * mm, "end": v(0.22, -2.3) * mm});
            skLineSegment(sketch, "E1720", {"start": v(0.22, -2.35) * mm, "end": v(0.15, -2.35) * mm});
            skLineSegment(sketch, "E1721", {"start": v(0.25, -2.3) * mm, "end": v(0.3, -2.3) * mm});
            skLineSegment(sketch, "E1722", {"start": v(0.3, -2.35) * mm, "end": v(0.25, -2.35) * mm});
            skLineSegment(sketch, "E1723", {"start": v(0.33, -2.3) * mm, "end": v(0.38, -2.3) * mm});
            skLineSegment(sketch, "E1724", {"start": v(0.38, -2.35) * mm, "end": v(0.33, -2.35) * mm});
            skLineSegment(sketch, "E1725", {"start": v(0.7, -2.37) * mm, "end": v(0.74, -2.37) * mm});
            skLineSegment(sketch, "E1726", {"start": v(0.7, -2.4) * mm, "end": v(0.74, -2.4) * mm});
            skLineSegment(sketch, "E1727", {"start": v(0.74, -2.37) * mm, "end": v(0.74, -2.4) * mm});
            skLineSegment(sketch, "E1728", {"start": v(0.7, -2.37) * mm, "end": v(0.7, -2.4) * mm});
            skLineSegment(sketch, "E1729", {"start": v(0.64, -2.37) * mm, "end": v(0.68, -2.37) * mm});
            skLineSegment(sketch, "E1730", {"start": v(0.64, -2.4) * mm, "end": v(0.68, -2.4) * mm});
            skLineSegment(sketch, "E1731", {"start": v(0.68, -2.37) * mm, "end": v(0.68, -2.4) * mm});
            skLineSegment(sketch, "E1732", {"start": v(0.64, -2.37) * mm, "end": v(0.64, -2.4) * mm});
            skLineSegment(sketch, "E1733", {"start": v(0.58, -2.37) * mm, "end": v(0.62, -2.37) * mm});
            skLineSegment(sketch, "E1734", {"start": v(0.58, -2.4) * mm, "end": v(0.62, -2.4) * mm});
            skLineSegment(sketch, "E1735", {"start": v(0.62, -2.37) * mm, "end": v(0.62, -2.4) * mm});
            skLineSegment(sketch, "E1736", {"start": v(0.58, -2.37) * mm, "end": v(0.58, -2.4) * mm});
            skLineSegment(sketch, "E1737", {"start": v(0.52, -2.37) * mm, "end": v(0.56, -2.37) * mm});
            skLineSegment(sketch, "E1738", {"start": v(0.52, -2.4) * mm, "end": v(0.56, -2.4) * mm});
            skLineSegment(sketch, "E1739", {"start": v(0.56, -2.37) * mm, "end": v(0.56, -2.4) * mm});
            skLineSegment(sketch, "E1740", {"start": v(0.52, -2.37) * mm, "end": v(0.52, -2.4) * mm});
            skLineSegment(sketch, "E1741", {"start": v(0.46, -2.37) * mm, "end": v(0.5, -2.37) * mm});
            skLineSegment(sketch, "E1742", {"start": v(0.46, -2.4) * mm, "end": v(0.5, -2.4) * mm});
            skLineSegment(sketch, "E1743", {"start": v(0.5, -2.37) * mm, "end": v(0.5, -2.4) * mm});
            skLineSegment(sketch, "E1744", {"start": v(0.46, -2.37) * mm, "end": v(0.46, -2.4) * mm});
            skLineSegment(sketch, "E1745", {"start": v(0.4, -2.37) * mm, "end": v(0.44, -2.37) * mm});
            skLineSegment(sketch, "E1746", {"start": v(0.4, -2.4) * mm, "end": v(0.44, -2.4) * mm});
            skLineSegment(sketch, "E1747", {"start": v(0.44, -2.37) * mm, "end": v(0.44, -2.4) * mm});
            skLineSegment(sketch, "E1748", {"start": v(0.4, -2.37) * mm, "end": v(0.4, -2.4) * mm});
            skLineSegment(sketch, "E1749", {"start": v(0.01, -2.37) * mm, "end": v(0.01, -2.4) * mm});
            skLineSegment(sketch, "E1750", {"start": v(0.38, -2.37) * mm, "end": v(0.38, -2.4) * mm});
            skLineSegment(sketch, "E1751", {"start": v(0.33, -2.37) * mm, "end": v(0.33, -2.4) * mm});
            skLineSegment(sketch, "E1752", {"start": v(0.3, -2.37) * mm, "end": v(0.3, -2.4) * mm});
            skLineSegment(sketch, "E1753", {"start": v(0.25, -2.37) * mm, "end": v(0.25, -2.4) * mm});
            skLineSegment(sketch, "E1754", {"start": v(0.22, -2.37) * mm, "end": v(0.22, -2.4) * mm});
            skLineSegment(sketch, "E1755", {"start": v(0.15, -2.37) * mm, "end": v(0.15, -2.4) * mm});
            skLineSegment(sketch, "E1756", {"start": v(0.13, -2.37) * mm, "end": v(0.13, -2.4) * mm});
            skLineSegment(sketch, "E1757", {"start": v(0.13, -2.37) * mm, "end": v(0.01, -2.37) * mm});
            skLineSegment(sketch, "E1758", {"start": v(0.13, -2.4) * mm, "end": v(0.01, -2.4) * mm});
            skLineSegment(sketch, "E1759", {"start": v(0.15, -2.37) * mm, "end": v(0.22, -2.37) * mm});
            skLineSegment(sketch, "E1760", {"start": v(0.22, -2.4) * mm, "end": v(0.15, -2.4) * mm});
            skLineSegment(sketch, "E1761", {"start": v(0.25, -2.37) * mm, "end": v(0.3, -2.37) * mm});
            skLineSegment(sketch, "E1762", {"start": v(0.3, -2.4) * mm, "end": v(0.25, -2.4) * mm});
            skLineSegment(sketch, "E1763", {"start": v(0.33, -2.37) * mm, "end": v(0.38, -2.37) * mm});
            skLineSegment(sketch, "E1764", {"start": v(0.38, -2.4) * mm, "end": v(0.33, -2.4) * mm});
            skLineSegment(sketch, "E1765", {"start": v(0.7, -2.43) * mm, "end": v(0.74, -2.43) * mm});
            skLineSegment(sketch, "E1766", {"start": v(0.7, -2.47) * mm, "end": v(0.74, -2.47) * mm});
            skLineSegment(sketch, "E1767", {"start": v(0.74, -2.43) * mm, "end": v(0.74, -2.47) * mm});
            skLineSegment(sketch, "E1768", {"start": v(0.7, -2.43) * mm, "end": v(0.7, -2.47) * mm});
            skLineSegment(sketch, "E1769", {"start": v(0.64, -2.43) * mm, "end": v(0.68, -2.43) * mm});
            skLineSegment(sketch, "E1770", {"start": v(0.64, -2.47) * mm, "end": v(0.68, -2.47) * mm});
            skLineSegment(sketch, "E1771", {"start": v(0.68, -2.43) * mm, "end": v(0.68, -2.47) * mm});
            skLineSegment(sketch, "E1772", {"start": v(0.64, -2.43) * mm, "end": v(0.64, -2.47) * mm});
            skLineSegment(sketch, "E1773", {"start": v(0.58, -2.43) * mm, "end": v(0.62, -2.43) * mm});
            skLineSegment(sketch, "E1774", {"start": v(0.58, -2.47) * mm, "end": v(0.62, -2.47) * mm});
            skLineSegment(sketch, "E1775", {"start": v(0.62, -2.43) * mm, "end": v(0.62, -2.47) * mm});
            skLineSegment(sketch, "E1776", {"start": v(0.58, -2.43) * mm, "end": v(0.58, -2.47) * mm});
            skLineSegment(sketch, "E1777", {"start": v(0.52, -2.43) * mm, "end": v(0.56, -2.43) * mm});
            skLineSegment(sketch, "E1778", {"start": v(0.52, -2.47) * mm, "end": v(0.56, -2.47) * mm});
            skLineSegment(sketch, "E1779", {"start": v(0.56, -2.43) * mm, "end": v(0.56, -2.47) * mm});
            skLineSegment(sketch, "E1780", {"start": v(0.52, -2.43) * mm, "end": v(0.52, -2.47) * mm});
            skLineSegment(sketch, "E1781", {"start": v(0.46, -2.43) * mm, "end": v(0.5, -2.43) * mm});
            skLineSegment(sketch, "E1782", {"start": v(0.46, -2.47) * mm, "end": v(0.5, -2.47) * mm});
            skLineSegment(sketch, "E1783", {"start": v(0.5, -2.43) * mm, "end": v(0.5, -2.47) * mm});
            skLineSegment(sketch, "E1784", {"start": v(0.46, -2.43) * mm, "end": v(0.46, -2.47) * mm});
            skLineSegment(sketch, "E1785", {"start": v(0.4, -2.43) * mm, "end": v(0.44, -2.43) * mm});
            skLineSegment(sketch, "E1786", {"start": v(0.4, -2.47) * mm, "end": v(0.44, -2.47) * mm});
            skLineSegment(sketch, "E1787", {"start": v(0.44, -2.43) * mm, "end": v(0.44, -2.47) * mm});
            skLineSegment(sketch, "E1788", {"start": v(0.4, -2.43) * mm, "end": v(0.4, -2.47) * mm});
            skLineSegment(sketch, "E1789", {"start": v(0.01, -2.43) * mm, "end": v(0.01, -2.47) * mm});
            skLineSegment(sketch, "E1790", {"start": v(0.38, -2.43) * mm, "end": v(0.38, -2.47) * mm});
            skLineSegment(sketch, "E1791", {"start": v(0.33, -2.43) * mm, "end": v(0.33, -2.47) * mm});
            skLineSegment(sketch, "E1792", {"start": v(0.3, -2.43) * mm, "end": v(0.3, -2.47) * mm});
            skLineSegment(sketch, "E1793", {"start": v(0.25, -2.43) * mm, "end": v(0.25, -2.47) * mm});
            skLineSegment(sketch, "E1794", {"start": v(0.22, -2.43) * mm, "end": v(0.22, -2.47) * mm});
            skLineSegment(sketch, "E1795", {"start": v(0.15, -2.43) * mm, "end": v(0.15, -2.47) * mm});
            skLineSegment(sketch, "E1796", {"start": v(0.13, -2.43) * mm, "end": v(0.13, -2.47) * mm});
            skLineSegment(sketch, "E1797", {"start": v(0.13, -2.43) * mm, "end": v(0.01, -2.43) * mm});
            skLineSegment(sketch, "E1798", {"start": v(0.13, -2.47) * mm, "end": v(0.01, -2.47) * mm});
            skLineSegment(sketch, "E1799", {"start": v(0.15, -2.43) * mm, "end": v(0.22, -2.43) * mm});
            skLineSegment(sketch, "E1800", {"start": v(0.22, -2.47) * mm, "end": v(0.15, -2.47) * mm});
            skLineSegment(sketch, "E1801", {"start": v(0.25, -2.43) * mm, "end": v(0.3, -2.43) * mm});
            skLineSegment(sketch, "E1802", {"start": v(0.3, -2.47) * mm, "end": v(0.25, -2.47) * mm});
            skLineSegment(sketch, "E1803", {"start": v(0.33, -2.43) * mm, "end": v(0.38, -2.43) * mm});
            skLineSegment(sketch, "E1804", {"start": v(0.38, -2.47) * mm, "end": v(0.33, -2.47) * mm});
            skLineSegment(sketch, "E1805", {"start": v(0.7, -2.49) * mm, "end": v(0.74, -2.49) * mm});
            skLineSegment(sketch, "E1806", {"start": v(0.7, -2.53) * mm, "end": v(0.74, -2.53) * mm});
            skLineSegment(sketch, "E1807", {"start": v(0.74, -2.49) * mm, "end": v(0.74, -2.53) * mm});
            skLineSegment(sketch, "E1808", {"start": v(0.7, -2.49) * mm, "end": v(0.7, -2.53) * mm});
            skLineSegment(sketch, "E1809", {"start": v(0.64, -2.49) * mm, "end": v(0.68, -2.49) * mm});
            skLineSegment(sketch, "E1810", {"start": v(0.64, -2.53) * mm, "end": v(0.68, -2.53) * mm});
            skLineSegment(sketch, "E1811", {"start": v(0.68, -2.49) * mm, "end": v(0.68, -2.53) * mm});
            skLineSegment(sketch, "E1812", {"start": v(0.64, -2.49) * mm, "end": v(0.64, -2.53) * mm});
            skLineSegment(sketch, "E1813", {"start": v(0.58, -2.49) * mm, "end": v(0.62, -2.49) * mm});
            skLineSegment(sketch, "E1814", {"start": v(0.58, -2.53) * mm, "end": v(0.62, -2.53) * mm});
            skLineSegment(sketch, "E1815", {"start": v(0.62, -2.49) * mm, "end": v(0.62, -2.53) * mm});
            skLineSegment(sketch, "E1816", {"start": v(0.58, -2.49) * mm, "end": v(0.58, -2.53) * mm});
            skLineSegment(sketch, "E1817", {"start": v(0.52, -2.49) * mm, "end": v(0.56, -2.49) * mm});
            skLineSegment(sketch, "E1818", {"start": v(0.52, -2.53) * mm, "end": v(0.56, -2.53) * mm});
            skLineSegment(sketch, "E1819", {"start": v(0.56, -2.49) * mm, "end": v(0.56, -2.53) * mm});
            skLineSegment(sketch, "E1820", {"start": v(0.52, -2.49) * mm, "end": v(0.52, -2.53) * mm});
            skLineSegment(sketch, "E1821", {"start": v(0.46, -2.49) * mm, "end": v(0.5, -2.49) * mm});
            skLineSegment(sketch, "E1822", {"start": v(0.46, -2.53) * mm, "end": v(0.5, -2.53) * mm});
            skLineSegment(sketch, "E1823", {"start": v(0.5, -2.49) * mm, "end": v(0.5, -2.53) * mm});
            skLineSegment(sketch, "E1824", {"start": v(0.46, -2.49) * mm, "end": v(0.46, -2.53) * mm});
            skLineSegment(sketch, "E1825", {"start": v(0.4, -2.49) * mm, "end": v(0.44, -2.49) * mm});
            skLineSegment(sketch, "E1826", {"start": v(0.4, -2.53) * mm, "end": v(0.44, -2.53) * mm});
            skLineSegment(sketch, "E1827", {"start": v(0.44, -2.49) * mm, "end": v(0.44, -2.53) * mm});
            skLineSegment(sketch, "E1828", {"start": v(0.4, -2.49) * mm, "end": v(0.4, -2.53) * mm});
            skLineSegment(sketch, "E1829", {"start": v(0.01, -2.49) * mm, "end": v(0.01, -2.53) * mm});
            skLineSegment(sketch, "E1830", {"start": v(0.38, -2.49) * mm, "end": v(0.38, -2.53) * mm});
            skLineSegment(sketch, "E1831", {"start": v(0.33, -2.49) * mm, "end": v(0.33, -2.53) * mm});
            skLineSegment(sketch, "E1832", {"start": v(0.3, -2.49) * mm, "end": v(0.3, -2.53) * mm});
            skLineSegment(sketch, "E1833", {"start": v(0.25, -2.49) * mm, "end": v(0.25, -2.53) * mm});
            skLineSegment(sketch, "E1834", {"start": v(0.22, -2.49) * mm, "end": v(0.22, -2.53) * mm});
            skLineSegment(sketch, "E1835", {"start": v(0.15, -2.49) * mm, "end": v(0.15, -2.53) * mm});
            skLineSegment(sketch, "E1836", {"start": v(0.13, -2.49) * mm, "end": v(0.13, -2.53) * mm});
            skLineSegment(sketch, "E1837", {"start": v(0.13, -2.49) * mm, "end": v(0.01, -2.49) * mm});
            skLineSegment(sketch, "E1838", {"start": v(0.13, -2.53) * mm, "end": v(0.01, -2.53) * mm});
            skLineSegment(sketch, "E1839", {"start": v(0.15, -2.49) * mm, "end": v(0.22, -2.49) * mm});
            skLineSegment(sketch, "E1840", {"start": v(0.22, -2.53) * mm, "end": v(0.15, -2.53) * mm});
            skLineSegment(sketch, "E1841", {"start": v(0.25, -2.49) * mm, "end": v(0.3, -2.49) * mm});
            skLineSegment(sketch, "E1842", {"start": v(0.3, -2.53) * mm, "end": v(0.25, -2.53) * mm});
            skLineSegment(sketch, "E1843", {"start": v(0.33, -2.49) * mm, "end": v(0.38, -2.49) * mm});
            skLineSegment(sketch, "E1844", {"start": v(0.38, -2.53) * mm, "end": v(0.33, -2.53) * mm});
            skLineSegment(sketch, "E1845", {"start": v(0.7, -2.55) * mm, "end": v(0.74, -2.55) * mm});
            skLineSegment(sketch, "E1846", {"start": v(0.7, -2.59) * mm, "end": v(0.74, -2.59) * mm});
            skLineSegment(sketch, "E1847", {"start": v(0.74, -2.55) * mm, "end": v(0.74, -2.59) * mm});
            skLineSegment(sketch, "E1848", {"start": v(0.7, -2.55) * mm, "end": v(0.7, -2.59) * mm});
            skLineSegment(sketch, "E1849", {"start": v(0.64, -2.55) * mm, "end": v(0.68, -2.55) * mm});
            skLineSegment(sketch, "E1850", {"start": v(0.64, -2.59) * mm, "end": v(0.68, -2.59) * mm});
            skLineSegment(sketch, "E1851", {"start": v(0.68, -2.55) * mm, "end": v(0.68, -2.59) * mm});
            skLineSegment(sketch, "E1852", {"start": v(0.64, -2.55) * mm, "end": v(0.64, -2.59) * mm});
            skLineSegment(sketch, "E1853", {"start": v(0.58, -2.55) * mm, "end": v(0.62, -2.55) * mm});
            skLineSegment(sketch, "E1854", {"start": v(0.58, -2.59) * mm, "end": v(0.62, -2.59) * mm});
            skLineSegment(sketch, "E1855", {"start": v(0.62, -2.55) * mm, "end": v(0.62, -2.59) * mm});
            skLineSegment(sketch, "E1856", {"start": v(0.58, -2.55) * mm, "end": v(0.58, -2.59) * mm});
            skLineSegment(sketch, "E1857", {"start": v(0.52, -2.55) * mm, "end": v(0.56, -2.55) * mm});
            skLineSegment(sketch, "E1858", {"start": v(0.52, -2.59) * mm, "end": v(0.56, -2.59) * mm});
            skLineSegment(sketch, "E1859", {"start": v(0.56, -2.55) * mm, "end": v(0.56, -2.59) * mm});
            skLineSegment(sketch, "E1860", {"start": v(0.52, -2.55) * mm, "end": v(0.52, -2.59) * mm});
            skLineSegment(sketch, "E1861", {"start": v(0.46, -2.55) * mm, "end": v(0.5, -2.55) * mm});
            skLineSegment(sketch, "E1862", {"start": v(0.46, -2.59) * mm, "end": v(0.5, -2.59) * mm});
            skLineSegment(sketch, "E1863", {"start": v(0.5, -2.55) * mm, "end": v(0.5, -2.59) * mm});
            skLineSegment(sketch, "E1864", {"start": v(0.46, -2.55) * mm, "end": v(0.46, -2.59) * mm});
            skLineSegment(sketch, "E1865", {"start": v(0.4, -2.55) * mm, "end": v(0.44, -2.55) * mm});
            skLineSegment(sketch, "E1866", {"start": v(0.4, -2.59) * mm, "end": v(0.44, -2.59) * mm});
            skLineSegment(sketch, "E1867", {"start": v(0.44, -2.55) * mm, "end": v(0.44, -2.59) * mm});
            skLineSegment(sketch, "E1868", {"start": v(0.4, -2.55) * mm, "end": v(0.4, -2.59) * mm});
            skLineSegment(sketch, "E1869", {"start": v(0.01, -2.55) * mm, "end": v(0.01, -2.59) * mm});
            skLineSegment(sketch, "E1870", {"start": v(0.38, -2.55) * mm, "end": v(0.38, -2.59) * mm});
            skLineSegment(sketch, "E1871", {"start": v(0.33, -2.55) * mm, "end": v(0.33, -2.59) * mm});
            skLineSegment(sketch, "E1872", {"start": v(0.3, -2.55) * mm, "end": v(0.3, -2.59) * mm});
            skLineSegment(sketch, "E1873", {"start": v(0.25, -2.55) * mm, "end": v(0.25, -2.59) * mm});
            skLineSegment(sketch, "E1874", {"start": v(0.22, -2.55) * mm, "end": v(0.22, -2.59) * mm});
            skLineSegment(sketch, "E1875", {"start": v(0.15, -2.55) * mm, "end": v(0.15, -2.59) * mm});
            skLineSegment(sketch, "E1876", {"start": v(0.13, -2.55) * mm, "end": v(0.13, -2.59) * mm});
            skLineSegment(sketch, "E1877", {"start": v(0.13, -2.55) * mm, "end": v(0.01, -2.55) * mm});
            skLineSegment(sketch, "E1878", {"start": v(0.13, -2.59) * mm, "end": v(0.01, -2.59) * mm});
            skLineSegment(sketch, "E1879", {"start": v(0.15, -2.55) * mm, "end": v(0.22, -2.55) * mm});
            skLineSegment(sketch, "E1880", {"start": v(0.22, -2.59) * mm, "end": v(0.15, -2.59) * mm});
            skLineSegment(sketch, "E1881", {"start": v(0.25, -2.55) * mm, "end": v(0.3, -2.55) * mm});
            skLineSegment(sketch, "E1882", {"start": v(0.3, -2.59) * mm, "end": v(0.25, -2.59) * mm});
            skLineSegment(sketch, "E1883", {"start": v(0.33, -2.55) * mm, "end": v(0.38, -2.55) * mm});
            skLineSegment(sketch, "E1884", {"start": v(0.38, -2.59) * mm, "end": v(0.33, -2.59) * mm});
            skLineSegment(sketch, "E1885", {"start": v(0.7, -2.6) * mm, "end": v(0.74, -2.6) * mm});
            skLineSegment(sketch, "E1886", {"start": v(0.7, -2.65) * mm, "end": v(0.74, -2.65) * mm});
            skLineSegment(sketch, "E1887", {"start": v(0.74, -2.6) * mm, "end": v(0.74, -2.65) * mm});
            skLineSegment(sketch, "E1888", {"start": v(0.7, -2.6) * mm, "end": v(0.7, -2.65) * mm});
            skLineSegment(sketch, "E1889", {"start": v(0.64, -2.6) * mm, "end": v(0.68, -2.6) * mm});
            skLineSegment(sketch, "E1890", {"start": v(0.64, -2.65) * mm, "end": v(0.68, -2.65) * mm});
            skLineSegment(sketch, "E1891", {"start": v(0.68, -2.6) * mm, "end": v(0.68, -2.65) * mm});
            skLineSegment(sketch, "E1892", {"start": v(0.64, -2.6) * mm, "end": v(0.64, -2.65) * mm});
            skLineSegment(sketch, "E1893", {"start": v(0.58, -2.6) * mm, "end": v(0.62, -2.6) * mm});
            skLineSegment(sketch, "E1894", {"start": v(0.58, -2.65) * mm, "end": v(0.62, -2.65) * mm});
            skLineSegment(sketch, "E1895", {"start": v(0.62, -2.6) * mm, "end": v(0.62, -2.65) * mm});
            skLineSegment(sketch, "E1896", {"start": v(0.58, -2.6) * mm, "end": v(0.58, -2.65) * mm});
            skLineSegment(sketch, "E1897", {"start": v(0.52, -2.6) * mm, "end": v(0.56, -2.6) * mm});
            skLineSegment(sketch, "E1898", {"start": v(0.52, -2.65) * mm, "end": v(0.56, -2.65) * mm});
            skLineSegment(sketch, "E1899", {"start": v(0.56, -2.6) * mm, "end": v(0.56, -2.65) * mm});
            skLineSegment(sketch, "E1900", {"start": v(0.52, -2.6) * mm, "end": v(0.52, -2.65) * mm});
            skLineSegment(sketch, "E1901", {"start": v(0.46, -2.6) * mm, "end": v(0.5, -2.6) * mm});
            skLineSegment(sketch, "E1902", {"start": v(0.46, -2.65) * mm, "end": v(0.5, -2.65) * mm});
            skLineSegment(sketch, "E1903", {"start": v(0.5, -2.6) * mm, "end": v(0.5, -2.65) * mm});
            skLineSegment(sketch, "E1904", {"start": v(0.46, -2.6) * mm, "end": v(0.46, -2.65) * mm});
            skLineSegment(sketch, "E1905", {"start": v(0.4, -2.6) * mm, "end": v(0.44, -2.6) * mm});
            skLineSegment(sketch, "E1906", {"start": v(0.4, -2.65) * mm, "end": v(0.44, -2.65) * mm});
            skLineSegment(sketch, "E1907", {"start": v(0.44, -2.6) * mm, "end": v(0.44, -2.65) * mm});
            skLineSegment(sketch, "E1908", {"start": v(0.4, -2.6) * mm, "end": v(0.4, -2.65) * mm});
            skLineSegment(sketch, "E1909", {"start": v(0.01, -2.6) * mm, "end": v(0.01, -2.65) * mm});
            skLineSegment(sketch, "E1910", {"start": v(0.38, -2.6) * mm, "end": v(0.38, -2.65) * mm});
            skLineSegment(sketch, "E1911", {"start": v(0.33, -2.6) * mm, "end": v(0.33, -2.65) * mm});
            skLineSegment(sketch, "E1912", {"start": v(0.3, -2.6) * mm, "end": v(0.3, -2.65) * mm});
            skLineSegment(sketch, "E1913", {"start": v(0.25, -2.6) * mm, "end": v(0.25, -2.65) * mm});
            skLineSegment(sketch, "E1914", {"start": v(0.22, -2.6) * mm, "end": v(0.22, -2.65) * mm});
            skLineSegment(sketch, "E1915", {"start": v(0.15, -2.6) * mm, "end": v(0.15, -2.65) * mm});
            skLineSegment(sketch, "E1916", {"start": v(0.13, -2.6) * mm, "end": v(0.13, -2.65) * mm});
            skLineSegment(sketch, "E1917", {"start": v(0.13, -2.6) * mm, "end": v(0.01, -2.6) * mm});
            skLineSegment(sketch, "E1918", {"start": v(0.13, -2.65) * mm, "end": v(0.01, -2.65) * mm});
            skLineSegment(sketch, "E1919", {"start": v(0.15, -2.6) * mm, "end": v(0.22, -2.6) * mm});
            skLineSegment(sketch, "E1920", {"start": v(0.22, -2.65) * mm, "end": v(0.15, -2.65) * mm});
            skLineSegment(sketch, "E1921", {"start": v(0.25, -2.6) * mm, "end": v(0.3, -2.6) * mm});
            skLineSegment(sketch, "E1922", {"start": v(0.3, -2.65) * mm, "end": v(0.25, -2.65) * mm});
            skLineSegment(sketch, "E1923", {"start": v(0.33, -2.6) * mm, "end": v(0.38, -2.6) * mm});
            skLineSegment(sketch, "E1924", {"start": v(0.38, -2.65) * mm, "end": v(0.33, -2.65) * mm});
            skLineSegment(sketch, "E1925", {"start": v(0.7, -2.67) * mm, "end": v(0.74, -2.67) * mm});
            skLineSegment(sketch, "E1926", {"start": v(0.7, -2.7) * mm, "end": v(0.74, -2.7) * mm});
            skLineSegment(sketch, "E1927", {"start": v(0.74, -2.67) * mm, "end": v(0.74, -2.7) * mm});
            skLineSegment(sketch, "E1928", {"start": v(0.7, -2.67) * mm, "end": v(0.7, -2.7) * mm});
            skLineSegment(sketch, "E1929", {"start": v(0.64, -2.67) * mm, "end": v(0.68, -2.67) * mm});
            skLineSegment(sketch, "E1930", {"start": v(0.64, -2.7) * mm, "end": v(0.68, -2.7) * mm});
            skLineSegment(sketch, "E1931", {"start": v(0.68, -2.67) * mm, "end": v(0.68, -2.7) * mm});
            skLineSegment(sketch, "E1932", {"start": v(0.64, -2.67) * mm, "end": v(0.64, -2.7) * mm});
            skLineSegment(sketch, "E1933", {"start": v(0.58, -2.67) * mm, "end": v(0.62, -2.67) * mm});
            skLineSegment(sketch, "E1934", {"start": v(0.58, -2.7) * mm, "end": v(0.62, -2.7) * mm});
            skLineSegment(sketch, "E1935", {"start": v(0.62, -2.67) * mm, "end": v(0.62, -2.7) * mm});
            skLineSegment(sketch, "E1936", {"start": v(0.58, -2.67) * mm, "end": v(0.58, -2.7) * mm});
            skLineSegment(sketch, "E1937", {"start": v(0.52, -2.67) * mm, "end": v(0.56, -2.67) * mm});
            skLineSegment(sketch, "E1938", {"start": v(0.52, -2.7) * mm, "end": v(0.56, -2.7) * mm});
            skLineSegment(sketch, "E1939", {"start": v(0.56, -2.67) * mm, "end": v(0.56, -2.7) * mm});
            skLineSegment(sketch, "E1940", {"start": v(0.52, -2.67) * mm, "end": v(0.52, -2.7) * mm});
            skLineSegment(sketch, "E1941", {"start": v(0.46, -2.67) * mm, "end": v(0.5, -2.67) * mm});
            skLineSegment(sketch, "E1942", {"start": v(0.46, -2.7) * mm, "end": v(0.5, -2.7) * mm});
            skLineSegment(sketch, "E1943", {"start": v(0.5, -2.67) * mm, "end": v(0.5, -2.7) * mm});
            skLineSegment(sketch, "E1944", {"start": v(0.46, -2.67) * mm, "end": v(0.46, -2.7) * mm});
            skLineSegment(sketch, "E1945", {"start": v(0.4, -2.67) * mm, "end": v(0.44, -2.67) * mm});
            skLineSegment(sketch, "E1946", {"start": v(0.4, -2.7) * mm, "end": v(0.44, -2.7) * mm});
            skLineSegment(sketch, "E1947", {"start": v(0.44, -2.67) * mm, "end": v(0.44, -2.7) * mm});
            skLineSegment(sketch, "E1948", {"start": v(0.4, -2.67) * mm, "end": v(0.4, -2.7) * mm});
            skLineSegment(sketch, "E1949", {"start": v(0.01, -2.67) * mm, "end": v(0.01, -2.7) * mm});
            skLineSegment(sketch, "E1950", {"start": v(0.38, -2.67) * mm, "end": v(0.38, -2.7) * mm});
            skLineSegment(sketch, "E1951", {"start": v(0.33, -2.67) * mm, "end": v(0.33, -2.7) * mm});
            skLineSegment(sketch, "E1952", {"start": v(0.3, -2.67) * mm, "end": v(0.3, -2.7) * mm});
            skLineSegment(sketch, "E1953", {"start": v(0.25, -2.67) * mm, "end": v(0.25, -2.7) * mm});
            skLineSegment(sketch, "E1954", {"start": v(0.22, -2.67) * mm, "end": v(0.22, -2.7) * mm});
            skLineSegment(sketch, "E1955", {"start": v(0.15, -2.67) * mm, "end": v(0.15, -2.7) * mm});
            skLineSegment(sketch, "E1956", {"start": v(0.13, -2.67) * mm, "end": v(0.13, -2.7) * mm});
            skLineSegment(sketch, "E1957", {"start": v(0.13, -2.67) * mm, "end": v(0.01, -2.67) * mm});
            skLineSegment(sketch, "E1958", {"start": v(0.13, -2.7) * mm, "end": v(0.01, -2.7) * mm});
            skLineSegment(sketch, "E1959", {"start": v(0.15, -2.67) * mm, "end": v(0.22, -2.67) * mm});
            skLineSegment(sketch, "E1960", {"start": v(0.22, -2.7) * mm, "end": v(0.15, -2.7) * mm});
            skLineSegment(sketch, "E1961", {"start": v(0.25, -2.67) * mm, "end": v(0.3, -2.67) * mm});
            skLineSegment(sketch, "E1962", {"start": v(0.3, -2.7) * mm, "end": v(0.25, -2.7) * mm});
            skLineSegment(sketch, "E1963", {"start": v(0.33, -2.67) * mm, "end": v(0.38, -2.67) * mm});
            skLineSegment(sketch, "E1964", {"start": v(0.38, -2.7) * mm, "end": v(0.33, -2.7) * mm});
            skLineSegment(sketch, "E1965", {"start": v(0.7, -2.73) * mm, "end": v(0.74, -2.73) * mm});
            skLineSegment(sketch, "E1966", {"start": v(0.7, -2.77) * mm, "end": v(0.74, -2.77) * mm});
            skLineSegment(sketch, "E1967", {"start": v(0.74, -2.73) * mm, "end": v(0.74, -2.77) * mm});
            skLineSegment(sketch, "E1968", {"start": v(0.7, -2.73) * mm, "end": v(0.7, -2.77) * mm});
            skLineSegment(sketch, "E1969", {"start": v(0.64, -2.73) * mm, "end": v(0.68, -2.73) * mm});
            skLineSegment(sketch, "E1970", {"start": v(0.64, -2.77) * mm, "end": v(0.68, -2.77) * mm});
            skLineSegment(sketch, "E1971", {"start": v(0.68, -2.73) * mm, "end": v(0.68, -2.77) * mm});
            skLineSegment(sketch, "E1972", {"start": v(0.64, -2.73) * mm, "end": v(0.64, -2.77) * mm});
            skLineSegment(sketch, "E1973", {"start": v(0.58, -2.73) * mm, "end": v(0.62, -2.73) * mm});
            skLineSegment(sketch, "E1974", {"start": v(0.58, -2.77) * mm, "end": v(0.62, -2.77) * mm});
            skLineSegment(sketch, "E1975", {"start": v(0.62, -2.73) * mm, "end": v(0.62, -2.77) * mm});
            skLineSegment(sketch, "E1976", {"start": v(0.58, -2.73) * mm, "end": v(0.58, -2.77) * mm});
            skLineSegment(sketch, "E1977", {"start": v(0.52, -2.73) * mm, "end": v(0.56, -2.73) * mm});
            skLineSegment(sketch, "E1978", {"start": v(0.52, -2.77) * mm, "end": v(0.56, -2.77) * mm});
            skLineSegment(sketch, "E1979", {"start": v(0.56, -2.73) * mm, "end": v(0.56, -2.77) * mm});
            skLineSegment(sketch, "E1980", {"start": v(0.52, -2.73) * mm, "end": v(0.52, -2.77) * mm});
            skLineSegment(sketch, "E1981", {"start": v(0.46, -2.73) * mm, "end": v(0.5, -2.73) * mm});
            skLineSegment(sketch, "E1982", {"start": v(0.46, -2.77) * mm, "end": v(0.5, -2.77) * mm});
            skLineSegment(sketch, "E1983", {"start": v(0.5, -2.73) * mm, "end": v(0.5, -2.77) * mm});
            skLineSegment(sketch, "E1984", {"start": v(0.46, -2.73) * mm, "end": v(0.46, -2.77) * mm});
            skLineSegment(sketch, "E1985", {"start": v(0.4, -2.73) * mm, "end": v(0.44, -2.73) * mm});
            skLineSegment(sketch, "E1986", {"start": v(0.4, -2.77) * mm, "end": v(0.44, -2.77) * mm});
            skLineSegment(sketch, "E1987", {"start": v(0.44, -2.73) * mm, "end": v(0.44, -2.77) * mm});
            skLineSegment(sketch, "E1988", {"start": v(0.4, -2.73) * mm, "end": v(0.4, -2.77) * mm});
            skLineSegment(sketch, "E1989", {"start": v(0.01, -2.73) * mm, "end": v(0.01, -2.77) * mm});
            skLineSegment(sketch, "E1990", {"start": v(0.38, -2.73) * mm, "end": v(0.38, -2.77) * mm});
            skLineSegment(sketch, "E1991", {"start": v(0.33, -2.73) * mm, "end": v(0.33, -2.77) * mm});
            skLineSegment(sketch, "E1992", {"start": v(0.3, -2.73) * mm, "end": v(0.3, -2.77) * mm});
            skLineSegment(sketch, "E1993", {"start": v(0.25, -2.73) * mm, "end": v(0.25, -2.77) * mm});
            skLineSegment(sketch, "E1994", {"start": v(0.22, -2.73) * mm, "end": v(0.22, -2.77) * mm});
            skLineSegment(sketch, "E1995", {"start": v(0.15, -2.73) * mm, "end": v(0.15, -2.77) * mm});
            skLineSegment(sketch, "E1996", {"start": v(0.13, -2.73) * mm, "end": v(0.13, -2.77) * mm});
            skLineSegment(sketch, "E1997", {"start": v(0.13, -2.73) * mm, "end": v(0.01, -2.73) * mm});
            skLineSegment(sketch, "E1998", {"start": v(0.13, -2.77) * mm, "end": v(0.01, -2.77) * mm});
            skLineSegment(sketch, "E1999", {"start": v(0.15, -2.73) * mm, "end": v(0.22, -2.73) * mm});
            skLineSegment(sketch, "E2000", {"start": v(0.22, -2.77) * mm, "end": v(0.15, -2.77) * mm});
            skLineSegment(sketch, "E2001", {"start": v(0.25, -2.73) * mm, "end": v(0.3, -2.73) * mm});
            skLineSegment(sketch, "E2002", {"start": v(0.3, -2.77) * mm, "end": v(0.25, -2.77) * mm});
            skLineSegment(sketch, "E2003", {"start": v(0.33, -2.73) * mm, "end": v(0.38, -2.73) * mm});
            skLineSegment(sketch, "E2004", {"start": v(0.38, -2.77) * mm, "end": v(0.33, -2.77) * mm});
            skLineSegment(sketch, "E2005", {"start": v(0.7, -2.79) * mm, "end": v(0.74, -2.79) * mm});
            skLineSegment(sketch, "E2006", {"start": v(0.7, -2.83) * mm, "end": v(0.74, -2.83) * mm});
            skLineSegment(sketch, "E2007", {"start": v(0.74, -2.79) * mm, "end": v(0.74, -2.83) * mm});
            skLineSegment(sketch, "E2008", {"start": v(0.7, -2.79) * mm, "end": v(0.7, -2.83) * mm});
            skLineSegment(sketch, "E2009", {"start": v(0.64, -2.79) * mm, "end": v(0.68, -2.79) * mm});
            skLineSegment(sketch, "E2010", {"start": v(0.64, -2.83) * mm, "end": v(0.68, -2.83) * mm});
            skLineSegment(sketch, "E2011", {"start": v(0.68, -2.79) * mm, "end": v(0.68, -2.83) * mm});
            skLineSegment(sketch, "E2012", {"start": v(0.64, -2.79) * mm, "end": v(0.64, -2.83) * mm});
            skLineSegment(sketch, "E2013", {"start": v(0.58, -2.79) * mm, "end": v(0.62, -2.79) * mm});
            skLineSegment(sketch, "E2014", {"start": v(0.58, -2.83) * mm, "end": v(0.62, -2.83) * mm});
            skLineSegment(sketch, "E2015", {"start": v(0.62, -2.79) * mm, "end": v(0.62, -2.83) * mm});
            skLineSegment(sketch, "E2016", {"start": v(0.58, -2.79) * mm, "end": v(0.58, -2.83) * mm});
            skLineSegment(sketch, "E2017", {"start": v(0.52, -2.79) * mm, "end": v(0.56, -2.79) * mm});
            skLineSegment(sketch, "E2018", {"start": v(0.52, -2.83) * mm, "end": v(0.56, -2.83) * mm});
            skLineSegment(sketch, "E2019", {"start": v(0.56, -2.79) * mm, "end": v(0.56, -2.83) * mm});
            skLineSegment(sketch, "E2020", {"start": v(0.52, -2.79) * mm, "end": v(0.52, -2.83) * mm});
            skLineSegment(sketch, "E2021", {"start": v(0.46, -2.79) * mm, "end": v(0.5, -2.79) * mm});
            skLineSegment(sketch, "E2022", {"start": v(0.46, -2.83) * mm, "end": v(0.5, -2.83) * mm});
            skLineSegment(sketch, "E2023", {"start": v(0.5, -2.79) * mm, "end": v(0.5, -2.83) * mm});
            skLineSegment(sketch, "E2024", {"start": v(0.46, -2.79) * mm, "end": v(0.46, -2.83) * mm});
            skLineSegment(sketch, "E2025", {"start": v(0.4, -2.79) * mm, "end": v(0.44, -2.79) * mm});
            skLineSegment(sketch, "E2026", {"start": v(0.4, -2.83) * mm, "end": v(0.44, -2.83) * mm});
            skLineSegment(sketch, "E2027", {"start": v(0.44, -2.79) * mm, "end": v(0.44, -2.83) * mm});
            skLineSegment(sketch, "E2028", {"start": v(0.4, -2.79) * mm, "end": v(0.4, -2.83) * mm});
            skLineSegment(sketch, "E2029", {"start": v(0.01, -2.79) * mm, "end": v(0.01, -2.83) * mm});
            skLineSegment(sketch, "E2030", {"start": v(0.38, -2.79) * mm, "end": v(0.38, -2.83) * mm});
            skLineSegment(sketch, "E2031", {"start": v(0.33, -2.79) * mm, "end": v(0.33, -2.83) * mm});
            skLineSegment(sketch, "E2032", {"start": v(0.3, -2.79) * mm, "end": v(0.3, -2.83) * mm});
            skLineSegment(sketch, "E2033", {"start": v(0.25, -2.79) * mm, "end": v(0.25, -2.83) * mm});
            skLineSegment(sketch, "E2034", {"start": v(0.22, -2.79) * mm, "end": v(0.22, -2.83) * mm});
            skLineSegment(sketch, "E2035", {"start": v(0.15, -2.79) * mm, "end": v(0.15, -2.83) * mm});
            skLineSegment(sketch, "E2036", {"start": v(0.13, -2.79) * mm, "end": v(0.13, -2.83) * mm});
            skLineSegment(sketch, "E2037", {"start": v(0.13, -2.79) * mm, "end": v(0.01, -2.79) * mm});
            skLineSegment(sketch, "E2038", {"start": v(0.13, -2.83) * mm, "end": v(0.01, -2.83) * mm});
            skLineSegment(sketch, "E2039", {"start": v(0.15, -2.79) * mm, "end": v(0.22, -2.79) * mm});
            skLineSegment(sketch, "E2040", {"start": v(0.22, -2.83) * mm, "end": v(0.15, -2.83) * mm});
            skLineSegment(sketch, "E2041", {"start": v(0.25, -2.79) * mm, "end": v(0.3, -2.79) * mm});
            skLineSegment(sketch, "E2042", {"start": v(0.3, -2.83) * mm, "end": v(0.25, -2.83) * mm});
            skLineSegment(sketch, "E2043", {"start": v(0.33, -2.79) * mm, "end": v(0.38, -2.79) * mm});
            skLineSegment(sketch, "E2044", {"start": v(0.38, -2.83) * mm, "end": v(0.33, -2.83) * mm});
            skLineSegment(sketch, "E2045", {"start": v(-0.7, -2.85) * mm, "end": v(-0.74, -2.85) * mm});
            skLineSegment(sketch, "E2046", {"start": v(-0.7, -2.89) * mm, "end": v(-0.74, -2.89) * mm});
            skLineSegment(sketch, "E2047", {"start": v(-0.74, -2.85) * mm, "end": v(-0.74, -2.89) * mm});
            skLineSegment(sketch, "E2048", {"start": v(-0.7, -2.85) * mm, "end": v(-0.7, -2.89) * mm});
            skLineSegment(sketch, "E2049", {"start": v(-0.64, -2.85) * mm, "end": v(-0.68, -2.85) * mm});
            skLineSegment(sketch, "E2050", {"start": v(-0.64, -2.89) * mm, "end": v(-0.68, -2.89) * mm});
            skLineSegment(sketch, "E2051", {"start": v(-0.68, -2.85) * mm, "end": v(-0.68, -2.89) * mm});
            skLineSegment(sketch, "E2052", {"start": v(-0.64, -2.85) * mm, "end": v(-0.64, -2.89) * mm});
            skLineSegment(sketch, "E2053", {"start": v(-0.58, -2.85) * mm, "end": v(-0.62, -2.85) * mm});
            skLineSegment(sketch, "E2054", {"start": v(-0.58, -2.89) * mm, "end": v(-0.62, -2.89) * mm});
            skLineSegment(sketch, "E2055", {"start": v(-0.62, -2.85) * mm, "end": v(-0.62, -2.89) * mm});
            skLineSegment(sketch, "E2056", {"start": v(-0.58, -2.85) * mm, "end": v(-0.58, -2.89) * mm});
            skLineSegment(sketch, "E2057", {"start": v(-0.52, -2.85) * mm, "end": v(-0.56, -2.85) * mm});
            skLineSegment(sketch, "E2058", {"start": v(-0.52, -2.89) * mm, "end": v(-0.56, -2.89) * mm});
            skLineSegment(sketch, "E2059", {"start": v(-0.56, -2.85) * mm, "end": v(-0.56, -2.89) * mm});
            skLineSegment(sketch, "E2060", {"start": v(-0.52, -2.85) * mm, "end": v(-0.52, -2.89) * mm});
            skLineSegment(sketch, "E2061", {"start": v(-0.46, -2.85) * mm, "end": v(-0.5, -2.85) * mm});
            skLineSegment(sketch, "E2062", {"start": v(-0.46, -2.89) * mm, "end": v(-0.5, -2.89) * mm});
            skLineSegment(sketch, "E2063", {"start": v(-0.5, -2.85) * mm, "end": v(-0.5, -2.89) * mm});
            skLineSegment(sketch, "E2064", {"start": v(-0.46, -2.85) * mm, "end": v(-0.46, -2.89) * mm});
            skLineSegment(sketch, "E2065", {"start": v(-0.4, -2.85) * mm, "end": v(-0.44, -2.85) * mm});
            skLineSegment(sketch, "E2066", {"start": v(-0.4, -2.89) * mm, "end": v(-0.44, -2.89) * mm});
            skLineSegment(sketch, "E2067", {"start": v(-0.44, -2.85) * mm, "end": v(-0.44, -2.89) * mm});
            skLineSegment(sketch, "E2068", {"start": v(-0.4, -2.85) * mm, "end": v(-0.4, -2.89) * mm});
            skLineSegment(sketch, "E2069", {"start": v(-0.01, -2.85) * mm, "end": v(-0.01, -2.89) * mm});
            skLineSegment(sketch, "E2070", {"start": v(-0.38, -2.85) * mm, "end": v(-0.38, -2.89) * mm});
            skLineSegment(sketch, "E2071", {"start": v(-0.33, -2.85) * mm, "end": v(-0.33, -2.89) * mm});
            skLineSegment(sketch, "E2072", {"start": v(-0.3, -2.85) * mm, "end": v(-0.3, -2.89) * mm});
            skLineSegment(sketch, "E2073", {"start": v(-0.25, -2.85) * mm, "end": v(-0.25, -2.89) * mm});
            skLineSegment(sketch, "E2074", {"start": v(-0.22, -2.85) * mm, "end": v(-0.22, -2.89) * mm});
            skLineSegment(sketch, "E2075", {"start": v(-0.15, -2.85) * mm, "end": v(-0.15, -2.89) * mm});
            skLineSegment(sketch, "E2076", {"start": v(-0.13, -2.85) * mm, "end": v(-0.13, -2.89) * mm});
            skLineSegment(sketch, "E2077", {"start": v(-0.13, -2.85) * mm, "end": v(-0.01, -2.85) * mm});
            skLineSegment(sketch, "E2078", {"start": v(-0.13, -2.89) * mm, "end": v(-0.01, -2.89) * mm});
            skLineSegment(sketch, "E2079", {"start": v(-0.15, -2.85) * mm, "end": v(-0.22, -2.85) * mm});
            skLineSegment(sketch, "E2080", {"start": v(-0.22, -2.89) * mm, "end": v(-0.15, -2.89) * mm});
            skLineSegment(sketch, "E2081", {"start": v(-0.25, -2.85) * mm, "end": v(-0.3, -2.85) * mm});
            skLineSegment(sketch, "E2082", {"start": v(-0.3, -2.89) * mm, "end": v(-0.25, -2.89) * mm});
            skLineSegment(sketch, "E2083", {"start": v(-0.33, -2.85) * mm, "end": v(-0.38, -2.85) * mm});
            skLineSegment(sketch, "E2084", {"start": v(-0.38, -2.89) * mm, "end": v(-0.33, -2.89) * mm});
            skLineSegment(sketch, "E2085", {"start": v(0.7, -2.85) * mm, "end": v(0.74, -2.85) * mm});
            skLineSegment(sketch, "E2086", {"start": v(0.7, -2.89) * mm, "end": v(0.74, -2.89) * mm});
            skLineSegment(sketch, "E2087", {"start": v(0.74, -2.85) * mm, "end": v(0.74, -2.89) * mm});
            skLineSegment(sketch, "E2088", {"start": v(0.7, -2.85) * mm, "end": v(0.7, -2.89) * mm});
            skLineSegment(sketch, "E2089", {"start": v(0.64, -2.85) * mm, "end": v(0.68, -2.85) * mm});
            skLineSegment(sketch, "E2090", {"start": v(0.64, -2.89) * mm, "end": v(0.68, -2.89) * mm});
            skLineSegment(sketch, "E2091", {"start": v(0.68, -2.85) * mm, "end": v(0.68, -2.89) * mm});
            skLineSegment(sketch, "E2092", {"start": v(0.64, -2.85) * mm, "end": v(0.64, -2.89) * mm});
            skLineSegment(sketch, "E2093", {"start": v(0.58, -2.85) * mm, "end": v(0.62, -2.85) * mm});
            skLineSegment(sketch, "E2094", {"start": v(0.58, -2.89) * mm, "end": v(0.62, -2.89) * mm});
            skLineSegment(sketch, "E2095", {"start": v(0.62, -2.85) * mm, "end": v(0.62, -2.89) * mm});
            skLineSegment(sketch, "E2096", {"start": v(0.58, -2.85) * mm, "end": v(0.58, -2.89) * mm});
            skLineSegment(sketch, "E2097", {"start": v(0.52, -2.85) * mm, "end": v(0.56, -2.85) * mm});
            skLineSegment(sketch, "E2098", {"start": v(0.52, -2.89) * mm, "end": v(0.56, -2.89) * mm});
            skLineSegment(sketch, "E2099", {"start": v(0.56, -2.85) * mm, "end": v(0.56, -2.89) * mm});
            skLineSegment(sketch, "E2100", {"start": v(0.52, -2.85) * mm, "end": v(0.52, -2.89) * mm});
            skLineSegment(sketch, "E2101", {"start": v(0.46, -2.85) * mm, "end": v(0.5, -2.85) * mm});
            skLineSegment(sketch, "E2102", {"start": v(0.46, -2.89) * mm, "end": v(0.5, -2.89) * mm});
            skLineSegment(sketch, "E2103", {"start": v(0.5, -2.85) * mm, "end": v(0.5, -2.89) * mm});
            skLineSegment(sketch, "E2104", {"start": v(0.46, -2.85) * mm, "end": v(0.46, -2.89) * mm});
            skLineSegment(sketch, "E2105", {"start": v(0.4, -2.85) * mm, "end": v(0.44, -2.85) * mm});
            skLineSegment(sketch, "E2106", {"start": v(0.4, -2.89) * mm, "end": v(0.44, -2.89) * mm});
            skLineSegment(sketch, "E2107", {"start": v(0.44, -2.85) * mm, "end": v(0.44, -2.89) * mm});
            skLineSegment(sketch, "E2108", {"start": v(0.4, -2.85) * mm, "end": v(0.4, -2.89) * mm});
            skLineSegment(sketch, "E2109", {"start": v(0.01, -2.85) * mm, "end": v(0.01, -2.89) * mm});
            skLineSegment(sketch, "E2110", {"start": v(0.38, -2.85) * mm, "end": v(0.38, -2.89) * mm});
            skLineSegment(sketch, "E2111", {"start": v(0.33, -2.85) * mm, "end": v(0.33, -2.89) * mm});
            skLineSegment(sketch, "E2112", {"start": v(0.3, -2.85) * mm, "end": v(0.3, -2.89) * mm});
            skLineSegment(sketch, "E2113", {"start": v(0.25, -2.85) * mm, "end": v(0.25, -2.89) * mm});
            skLineSegment(sketch, "E2114", {"start": v(0.22, -2.85) * mm, "end": v(0.22, -2.89) * mm});
            skLineSegment(sketch, "E2115", {"start": v(0.15, -2.85) * mm, "end": v(0.15, -2.89) * mm});
            skLineSegment(sketch, "E2116", {"start": v(0.13, -2.85) * mm, "end": v(0.13, -2.89) * mm});
            skLineSegment(sketch, "E2117", {"start": v(0.13, -2.85) * mm, "end": v(0.01, -2.85) * mm});
            skLineSegment(sketch, "E2118", {"start": v(0.13, -2.89) * mm, "end": v(0.01, -2.89) * mm});
            skLineSegment(sketch, "E2119", {"start": v(0.15, -2.85) * mm, "end": v(0.22, -2.85) * mm});
            skLineSegment(sketch, "E2120", {"start": v(0.22, -2.89) * mm, "end": v(0.15, -2.89) * mm});
            skLineSegment(sketch, "E2121", {"start": v(0.25, -2.85) * mm, "end": v(0.3, -2.85) * mm});
            skLineSegment(sketch, "E2122", {"start": v(0.3, -2.89) * mm, "end": v(0.25, -2.89) * mm});
            skLineSegment(sketch, "E2123", {"start": v(0.33, -2.85) * mm, "end": v(0.38, -2.85) * mm});
            skLineSegment(sketch, "E2124", {"start": v(0.38, -2.89) * mm, "end": v(0.33, -2.89) * mm});
            skLineSegment(sketch, "E2125", {"start": v(-0.7, -2.9) * mm, "end": v(-0.74, -2.9) * mm});
            skLineSegment(sketch, "E2126", {"start": v(-0.7, -2.95) * mm, "end": v(-0.74, -2.95) * mm});
            skLineSegment(sketch, "E2127", {"start": v(-0.74, -2.9) * mm, "end": v(-0.74, -2.95) * mm});
            skLineSegment(sketch, "E2128", {"start": v(-0.7, -2.9) * mm, "end": v(-0.7, -2.95) * mm});
            skLineSegment(sketch, "E2129", {"start": v(-0.64, -2.9) * mm, "end": v(-0.68, -2.9) * mm});
            skLineSegment(sketch, "E2130", {"start": v(-0.64, -2.95) * mm, "end": v(-0.68, -2.95) * mm});
            skLineSegment(sketch, "E2131", {"start": v(-0.68, -2.9) * mm, "end": v(-0.68, -2.95) * mm});
            skLineSegment(sketch, "E2132", {"start": v(-0.64, -2.9) * mm, "end": v(-0.64, -2.95) * mm});
            skLineSegment(sketch, "E2133", {"start": v(-0.58, -2.9) * mm, "end": v(-0.62, -2.9) * mm});
            skLineSegment(sketch, "E2134", {"start": v(-0.58, -2.95) * mm, "end": v(-0.62, -2.95) * mm});
            skLineSegment(sketch, "E2135", {"start": v(-0.62, -2.9) * mm, "end": v(-0.62, -2.95) * mm});
            skLineSegment(sketch, "E2136", {"start": v(-0.58, -2.9) * mm, "end": v(-0.58, -2.95) * mm});
            skLineSegment(sketch, "E2137", {"start": v(-0.52, -2.9) * mm, "end": v(-0.56, -2.9) * mm});
            skLineSegment(sketch, "E2138", {"start": v(-0.52, -2.95) * mm, "end": v(-0.56, -2.95) * mm});
            skLineSegment(sketch, "E2139", {"start": v(-0.56, -2.9) * mm, "end": v(-0.56, -2.95) * mm});
            skLineSegment(sketch, "E2140", {"start": v(-0.52, -2.9) * mm, "end": v(-0.52, -2.95) * mm});
            skLineSegment(sketch, "E2141", {"start": v(-0.46, -2.9) * mm, "end": v(-0.5, -2.9) * mm});
            skLineSegment(sketch, "E2142", {"start": v(-0.46, -2.95) * mm, "end": v(-0.5, -2.95) * mm});
            skLineSegment(sketch, "E2143", {"start": v(-0.5, -2.9) * mm, "end": v(-0.5, -2.95) * mm});
            skLineSegment(sketch, "E2144", {"start": v(-0.46, -2.9) * mm, "end": v(-0.46, -2.95) * mm});
            skLineSegment(sketch, "E2145", {"start": v(-0.4, -2.9) * mm, "end": v(-0.44, -2.9) * mm});
            skLineSegment(sketch, "E2146", {"start": v(-0.4, -2.95) * mm, "end": v(-0.44, -2.95) * mm});
            skLineSegment(sketch, "E2147", {"start": v(-0.44, -2.9) * mm, "end": v(-0.44, -2.95) * mm});
            skLineSegment(sketch, "E2148", {"start": v(-0.4, -2.9) * mm, "end": v(-0.4, -2.95) * mm});
            skLineSegment(sketch, "E2149", {"start": v(-0.01, -2.9) * mm, "end": v(-0.01, -2.95) * mm});
            skLineSegment(sketch, "E2150", {"start": v(-0.38, -2.9) * mm, "end": v(-0.38, -2.95) * mm});
            skLineSegment(sketch, "E2151", {"start": v(-0.33, -2.9) * mm, "end": v(-0.33, -2.95) * mm});
            skLineSegment(sketch, "E2152", {"start": v(-0.3, -2.9) * mm, "end": v(-0.3, -2.95) * mm});
            skLineSegment(sketch, "E2153", {"start": v(-0.25, -2.9) * mm, "end": v(-0.25, -2.95) * mm});
            skLineSegment(sketch, "E2154", {"start": v(-0.22, -2.9) * mm, "end": v(-0.22, -2.95) * mm});
            skLineSegment(sketch, "E2155", {"start": v(-0.15, -2.9) * mm, "end": v(-0.15, -2.95) * mm});
            skLineSegment(sketch, "E2156", {"start": v(-0.13, -2.9) * mm, "end": v(-0.13, -2.95) * mm});
            skLineSegment(sketch, "E2157", {"start": v(-0.13, -2.9) * mm, "end": v(-0.01, -2.9) * mm});
            skLineSegment(sketch, "E2158", {"start": v(-0.13, -2.95) * mm, "end": v(-0.01, -2.95) * mm});
            skLineSegment(sketch, "E2159", {"start": v(-0.15, -2.9) * mm, "end": v(-0.22, -2.9) * mm});
            skLineSegment(sketch, "E2160", {"start": v(-0.22, -2.95) * mm, "end": v(-0.15, -2.95) * mm});
            skLineSegment(sketch, "E2161", {"start": v(-0.25, -2.9) * mm, "end": v(-0.3, -2.9) * mm});
            skLineSegment(sketch, "E2162", {"start": v(-0.3, -2.95) * mm, "end": v(-0.25, -2.95) * mm});
            skLineSegment(sketch, "E2163", {"start": v(-0.33, -2.9) * mm, "end": v(-0.38, -2.9) * mm});
            skLineSegment(sketch, "E2164", {"start": v(-0.38, -2.95) * mm, "end": v(-0.33, -2.95) * mm});
            skLineSegment(sketch, "E2165", {"start": v(0.7, -2.9) * mm, "end": v(0.74, -2.9) * mm});
            skLineSegment(sketch, "E2166", {"start": v(0.7, -2.95) * mm, "end": v(0.74, -2.95) * mm});
            skLineSegment(sketch, "E2167", {"start": v(0.74, -2.9) * mm, "end": v(0.74, -2.95) * mm});
            skLineSegment(sketch, "E2168", {"start": v(0.7, -2.9) * mm, "end": v(0.7, -2.95) * mm});
            skLineSegment(sketch, "E2169", {"start": v(0.64, -2.9) * mm, "end": v(0.68, -2.9) * mm});
            skLineSegment(sketch, "E2170", {"start": v(0.64, -2.95) * mm, "end": v(0.68, -2.95) * mm});
            skLineSegment(sketch, "E2171", {"start": v(0.68, -2.9) * mm, "end": v(0.68, -2.95) * mm});
            skLineSegment(sketch, "E2172", {"start": v(0.64, -2.9) * mm, "end": v(0.64, -2.95) * mm});
            skLineSegment(sketch, "E2173", {"start": v(0.58, -2.9) * mm, "end": v(0.62, -2.9) * mm});
            skLineSegment(sketch, "E2174", {"start": v(0.58, -2.95) * mm, "end": v(0.62, -2.95) * mm});
            skLineSegment(sketch, "E2175", {"start": v(0.62, -2.9) * mm, "end": v(0.62, -2.95) * mm});
            skLineSegment(sketch, "E2176", {"start": v(0.58, -2.9) * mm, "end": v(0.58, -2.95) * mm});
            skLineSegment(sketch, "E2177", {"start": v(0.52, -2.9) * mm, "end": v(0.56, -2.9) * mm});
            skLineSegment(sketch, "E2178", {"start": v(0.52, -2.95) * mm, "end": v(0.56, -2.95) * mm});
            skLineSegment(sketch, "E2179", {"start": v(0.56, -2.9) * mm, "end": v(0.56, -2.95) * mm});
            skLineSegment(sketch, "E2180", {"start": v(0.52, -2.9) * mm, "end": v(0.52, -2.95) * mm});
            skLineSegment(sketch, "E2181", {"start": v(0.46, -2.9) * mm, "end": v(0.5, -2.9) * mm});
            skLineSegment(sketch, "E2182", {"start": v(0.46, -2.95) * mm, "end": v(0.5, -2.95) * mm});
            skLineSegment(sketch, "E2183", {"start": v(0.5, -2.9) * mm, "end": v(0.5, -2.95) * mm});
            skLineSegment(sketch, "E2184", {"start": v(0.46, -2.9) * mm, "end": v(0.46, -2.95) * mm});
            skLineSegment(sketch, "E2185", {"start": v(0.4, -2.9) * mm, "end": v(0.44, -2.9) * mm});
            skLineSegment(sketch, "E2186", {"start": v(0.4, -2.95) * mm, "end": v(0.44, -2.95) * mm});
            skLineSegment(sketch, "E2187", {"start": v(0.44, -2.9) * mm, "end": v(0.44, -2.95) * mm});
            skLineSegment(sketch, "E2188", {"start": v(0.4, -2.9) * mm, "end": v(0.4, -2.95) * mm});
            skLineSegment(sketch, "E2189", {"start": v(0.01, -2.9) * mm, "end": v(0.01, -2.95) * mm});
            skLineSegment(sketch, "E2190", {"start": v(0.38, -2.9) * mm, "end": v(0.38, -2.95) * mm});
            skLineSegment(sketch, "E2191", {"start": v(0.33, -2.9) * mm, "end": v(0.33, -2.95) * mm});
            skLineSegment(sketch, "E2192", {"start": v(0.3, -2.9) * mm, "end": v(0.3, -2.95) * mm});
            skLineSegment(sketch, "E2193", {"start": v(0.25, -2.9) * mm, "end": v(0.25, -2.95) * mm});
            skLineSegment(sketch, "E2194", {"start": v(0.22, -2.9) * mm, "end": v(0.22, -2.95) * mm});
            skLineSegment(sketch, "E2195", {"start": v(0.15, -2.9) * mm, "end": v(0.15, -2.95) * mm});
            skLineSegment(sketch, "E2196", {"start": v(0.13, -2.9) * mm, "end": v(0.13, -2.95) * mm});
            skLineSegment(sketch, "E2197", {"start": v(0.13, -2.9) * mm, "end": v(0.01, -2.9) * mm});
            skLineSegment(sketch, "E2198", {"start": v(0.13, -2.95) * mm, "end": v(0.01, -2.95) * mm});
            skLineSegment(sketch, "E2199", {"start": v(0.15, -2.9) * mm, "end": v(0.22, -2.9) * mm});
            skLineSegment(sketch, "E2200", {"start": v(0.22, -2.95) * mm, "end": v(0.15, -2.95) * mm});
            skLineSegment(sketch, "E2201", {"start": v(0.25, -2.9) * mm, "end": v(0.3, -2.9) * mm});
            skLineSegment(sketch, "E2202", {"start": v(0.3, -2.95) * mm, "end": v(0.25, -2.95) * mm});
            skLineSegment(sketch, "E2203", {"start": v(0.33, -2.9) * mm, "end": v(0.38, -2.9) * mm});
            skLineSegment(sketch, "E2204", {"start": v(0.38, -2.95) * mm, "end": v(0.33, -2.95) * mm});
            skLineSegment(sketch, "E2205", {"start": v(-0.7, -2.97) * mm, "end": v(-0.74, -2.97) * mm});
            skLineSegment(sketch, "E2206", {"start": v(-0.7, -3) * mm, "end": v(-0.74, -3) * mm});
            skLineSegment(sketch, "E2207", {"start": v(-0.74, -2.97) * mm, "end": v(-0.74, -3) * mm});
            skLineSegment(sketch, "E2208", {"start": v(-0.7, -2.97) * mm, "end": v(-0.7, -3) * mm});
            skLineSegment(sketch, "E2209", {"start": v(-0.64, -2.97) * mm, "end": v(-0.68, -2.97) * mm});
            skLineSegment(sketch, "E2210", {"start": v(-0.64, -3) * mm, "end": v(-0.68, -3) * mm});
            skLineSegment(sketch, "E2211", {"start": v(-0.68, -2.97) * mm, "end": v(-0.68, -3) * mm});
            skLineSegment(sketch, "E2212", {"start": v(-0.64, -2.97) * mm, "end": v(-0.64, -3) * mm});
            skLineSegment(sketch, "E2213", {"start": v(-0.58, -2.97) * mm, "end": v(-0.62, -2.97) * mm});
            skLineSegment(sketch, "E2214", {"start": v(-0.58, -3) * mm, "end": v(-0.62, -3) * mm});
            skLineSegment(sketch, "E2215", {"start": v(-0.62, -2.97) * mm, "end": v(-0.62, -3) * mm});
            skLineSegment(sketch, "E2216", {"start": v(-0.58, -2.97) * mm, "end": v(-0.58, -3) * mm});
            skLineSegment(sketch, "E2217", {"start": v(-0.52, -2.97) * mm, "end": v(-0.56, -2.97) * mm});
            skLineSegment(sketch, "E2218", {"start": v(-0.52, -3) * mm, "end": v(-0.56, -3) * mm});
            skLineSegment(sketch, "E2219", {"start": v(-0.56, -2.97) * mm, "end": v(-0.56, -3) * mm});
            skLineSegment(sketch, "E2220", {"start": v(-0.52, -2.97) * mm, "end": v(-0.52, -3) * mm});
            skLineSegment(sketch, "E2221", {"start": v(-0.46, -2.97) * mm, "end": v(-0.5, -2.97) * mm});
            skLineSegment(sketch, "E2222", {"start": v(-0.46, -3) * mm, "end": v(-0.5, -3) * mm});
            skLineSegment(sketch, "E2223", {"start": v(-0.5, -2.97) * mm, "end": v(-0.5, -3) * mm});
            skLineSegment(sketch, "E2224", {"start": v(-0.46, -2.97) * mm, "end": v(-0.46, -3) * mm});
            skLineSegment(sketch, "E2225", {"start": v(-0.4, -2.97) * mm, "end": v(-0.44, -2.97) * mm});
            skLineSegment(sketch, "E2226", {"start": v(-0.4, -3) * mm, "end": v(-0.44, -3) * mm});
            skLineSegment(sketch, "E2227", {"start": v(-0.44, -2.97) * mm, "end": v(-0.44, -3) * mm});
            skLineSegment(sketch, "E2228", {"start": v(-0.4, -2.97) * mm, "end": v(-0.4, -3) * mm});
            skLineSegment(sketch, "E2229", {"start": v(-0.01, -2.97) * mm, "end": v(-0.01, -3) * mm});
            skLineSegment(sketch, "E2230", {"start": v(-0.38, -2.97) * mm, "end": v(-0.38, -3) * mm});
            skLineSegment(sketch, "E2231", {"start": v(-0.33, -2.97) * mm, "end": v(-0.33, -3) * mm});
            skLineSegment(sketch, "E2232", {"start": v(-0.3, -2.97) * mm, "end": v(-0.3, -3) * mm});
            skLineSegment(sketch, "E2233", {"start": v(-0.25, -2.97) * mm, "end": v(-0.25, -3) * mm});
            skLineSegment(sketch, "E2234", {"start": v(-0.22, -2.97) * mm, "end": v(-0.22, -3) * mm});
            skLineSegment(sketch, "E2235", {"start": v(-0.15, -2.97) * mm, "end": v(-0.15, -3) * mm});
            skLineSegment(sketch, "E2236", {"start": v(-0.13, -2.97) * mm, "end": v(-0.13, -3) * mm});
            skLineSegment(sketch, "E2237", {"start": v(-0.13, -2.97) * mm, "end": v(-0.01, -2.97) * mm});
            skLineSegment(sketch, "E2238", {"start": v(-0.13, -3) * mm, "end": v(-0.01, -3) * mm});
            skLineSegment(sketch, "E2239", {"start": v(-0.15, -2.97) * mm, "end": v(-0.22, -2.97) * mm});
            skLineSegment(sketch, "E2240", {"start": v(-0.22, -3) * mm, "end": v(-0.15, -3) * mm});
            skLineSegment(sketch, "E2241", {"start": v(-0.25, -2.97) * mm, "end": v(-0.3, -2.97) * mm});
            skLineSegment(sketch, "E2242", {"start": v(-0.3, -3) * mm, "end": v(-0.25, -3) * mm});
            skLineSegment(sketch, "E2243", {"start": v(-0.33, -2.97) * mm, "end": v(-0.38, -2.97) * mm});
            skLineSegment(sketch, "E2244", {"start": v(-0.38, -3) * mm, "end": v(-0.33, -3) * mm});
            skLineSegment(sketch, "E2245", {"start": v(0.7, -2.97) * mm, "end": v(0.74, -2.97) * mm});
            skLineSegment(sketch, "E2246", {"start": v(0.7, -3) * mm, "end": v(0.74, -3) * mm});
            skLineSegment(sketch, "E2247", {"start": v(0.74, -2.97) * mm, "end": v(0.74, -3) * mm});
            skLineSegment(sketch, "E2248", {"start": v(0.7, -2.97) * mm, "end": v(0.7, -3) * mm});
            skLineSegment(sketch, "E2249", {"start": v(0.64, -2.97) * mm, "end": v(0.68, -2.97) * mm});
            skLineSegment(sketch, "E2250", {"start": v(0.64, -3) * mm, "end": v(0.68, -3) * mm});
            skLineSegment(sketch, "E2251", {"start": v(0.68, -2.97) * mm, "end": v(0.68, -3) * mm});
            skLineSegment(sketch, "E2252", {"start": v(0.64, -2.97) * mm, "end": v(0.64, -3) * mm});
            skLineSegment(sketch, "E2253", {"start": v(0.58, -2.97) * mm, "end": v(0.62, -2.97) * mm});
            skLineSegment(sketch, "E2254", {"start": v(0.58, -3) * mm, "end": v(0.62, -3) * mm});
            skLineSegment(sketch, "E2255", {"start": v(0.62, -2.97) * mm, "end": v(0.62, -3) * mm});
            skLineSegment(sketch, "E2256", {"start": v(0.58, -2.97) * mm, "end": v(0.58, -3) * mm});
            skLineSegment(sketch, "E2257", {"start": v(0.52, -2.97) * mm, "end": v(0.56, -2.97) * mm});
            skLineSegment(sketch, "E2258", {"start": v(0.52, -3) * mm, "end": v(0.56, -3) * mm});
            skLineSegment(sketch, "E2259", {"start": v(0.56, -2.97) * mm, "end": v(0.56, -3) * mm});
            skLineSegment(sketch, "E2260", {"start": v(0.52, -2.97) * mm, "end": v(0.52, -3) * mm});
            skLineSegment(sketch, "E2261", {"start": v(0.46, -2.97) * mm, "end": v(0.5, -2.97) * mm});
            skLineSegment(sketch, "E2262", {"start": v(0.46, -3) * mm, "end": v(0.5, -3) * mm});
            skLineSegment(sketch, "E2263", {"start": v(0.5, -2.97) * mm, "end": v(0.5, -3) * mm});
            skLineSegment(sketch, "E2264", {"start": v(0.46, -2.97) * mm, "end": v(0.46, -3) * mm});
            skLineSegment(sketch, "E2265", {"start": v(0.4, -2.97) * mm, "end": v(0.44, -2.97) * mm});
            skLineSegment(sketch, "E2266", {"start": v(0.4, -3) * mm, "end": v(0.44, -3) * mm});
            skLineSegment(sketch, "E2267", {"start": v(0.44, -2.97) * mm, "end": v(0.44, -3) * mm});
            skLineSegment(sketch, "E2268", {"start": v(0.4, -2.97) * mm, "end": v(0.4, -3) * mm});
            skLineSegment(sketch, "E2269", {"start": v(0.01, -2.97) * mm, "end": v(0.01, -3) * mm});
            skLineSegment(sketch, "E2270", {"start": v(0.38, -2.97) * mm, "end": v(0.38, -3) * mm});
            skLineSegment(sketch, "E2271", {"start": v(0.33, -2.97) * mm, "end": v(0.33, -3) * mm});
            skLineSegment(sketch, "E2272", {"start": v(0.3, -2.97) * mm, "end": v(0.3, -3) * mm});
            skLineSegment(sketch, "E2273", {"start": v(0.25, -2.97) * mm, "end": v(0.25, -3) * mm});
            skLineSegment(sketch, "E2274", {"start": v(0.22, -2.97) * mm, "end": v(0.22, -3) * mm});
            skLineSegment(sketch, "E2275", {"start": v(0.15, -2.97) * mm, "end": v(0.15, -3) * mm});
            skLineSegment(sketch, "E2276", {"start": v(0.13, -2.97) * mm, "end": v(0.13, -3) * mm});
            skLineSegment(sketch, "E2277", {"start": v(0.13, -2.97) * mm, "end": v(0.01, -2.97) * mm});
            skLineSegment(sketch, "E2278", {"start": v(0.13, -3) * mm, "end": v(0.01, -3) * mm});
            skLineSegment(sketch, "E2279", {"start": v(0.15, -2.97) * mm, "end": v(0.22, -2.97) * mm});
            skLineSegment(sketch, "E2280", {"start": v(0.22, -3) * mm, "end": v(0.15, -3) * mm});
            skLineSegment(sketch, "E2281", {"start": v(0.25, -2.97) * mm, "end": v(0.3, -2.97) * mm});
            skLineSegment(sketch, "E2282", {"start": v(0.3, -3) * mm, "end": v(0.25, -3) * mm});
            skLineSegment(sketch, "E2283", {"start": v(0.33, -2.97) * mm, "end": v(0.38, -2.97) * mm});
            skLineSegment(sketch, "E2284", {"start": v(0.38, -3) * mm, "end": v(0.33, -3) * mm});
            skLineSegment(sketch, "E2285", {"start": v(-0.74, -1.33) * mm, "end": v(-0.74, -1.3) * mm});
            skLineSegment(sketch, "E2286", {"start": v(-0.74, -1.25) * mm, "end": v(-1.74, -1.25) * mm});
            skLineSegment(sketch, "E2287", {"start": v(-0.74, -1.3) * mm, "end": v(-1.74, -1.3) * mm});
            skLineSegment(sketch, "E2288", {"start": v(-0.58, -1.33) * mm, "end": v(-0.74, -1.33) * mm});
            skLineSegment(sketch, "E2289", {"start": v(-0.58, -1.23) * mm, "end": v(-0.74, -1.23) * mm});
            skLineSegment(sketch, "E2290", {"start": v(-0.74, -1.25) * mm, "end": v(-0.74, -1.23) * mm});
            skLineSegment(sketch, "E2291", {"start": v(-0.56, -1.23) * mm, "end": v(-0.52, -1.23) * mm});
            skLineSegment(sketch, "E2292", {"start": v(-0.5, -1.23) * mm, "end": v(-0.46, -1.23) * mm});
            skLineSegment(sketch, "E2293", {"start": v(-0.44, -1.23) * mm, "end": v(-0.4, -1.23) * mm});
            skLineSegment(sketch, "E2294", {"start": v(-0.38, -1.23) * mm, "end": v(-0.33, -1.23) * mm});
            skLineSegment(sketch, "E2295", {"start": v(-0.3, -1.23) * mm, "end": v(-0.25, -1.23) * mm});
            skLineSegment(sketch, "E2296", {"start": v(-0.22, -1.23) * mm, "end": v(-0.15, -1.23) * mm});
            skLineSegment(sketch, "E2297", {"start": v(-0.13, -1.23) * mm, "end": v(-0.01, -1.23) * mm});
            skLineSegment(sketch, "E2298", {"start": v(0.13, -1.23) * mm, "end": v(0.01, -1.23) * mm});
            skLineSegment(sketch, "E2299", {"start": v(0.22, -1.23) * mm, "end": v(0.15, -1.23) * mm});
            skLineSegment(sketch, "E2300", {"start": v(0.3, -1.23) * mm, "end": v(0.25, -1.23) * mm});
            skLineSegment(sketch, "E2301", {"start": v(0.38, -1.23) * mm, "end": v(0.33, -1.23) * mm});
            skLineSegment(sketch, "E2302", {"start": v(0.44, -1.23) * mm, "end": v(0.4, -1.23) * mm});
            skLineSegment(sketch, "E2303", {"start": v(0.5, -1.23) * mm, "end": v(0.46, -1.23) * mm});
            skLineSegment(sketch, "E2304", {"start": v(0.56, -1.23) * mm, "end": v(0.52, -1.23) * mm});
            skLineSegment(sketch, "E2305", {"start": v(0.58, -1.23) * mm, "end": v(0.74, -1.23) * mm});
            skLineSegment(sketch, "E2306", {"start": v(0.74, -1.33) * mm, "end": v(0.74, -1.3) * mm});
            skLineSegment(sketch, "E2307", {"start": v(0.74, -1.25) * mm, "end": v(1.74, -1.25) * mm});
            skLineSegment(sketch, "E2308", {"start": v(0.74, -1.3) * mm, "end": v(1.74, -1.3) * mm});
            skLineSegment(sketch, "E2309", {"start": v(0.74, -1.25) * mm, "end": v(0.74, -1.23) * mm});
            skLineSegment(sketch, "E2310", {"start": v(1.74, -1.3) * mm, "end": v(1.74, -1.25) * mm});
            skLineSegment(sketch, "E2311", {"start": v(-1.74, -1.3) * mm, "end": v(-1.74, -1.25) * mm});
            skLineSegment(sketch, "E2312", {"start": v(-0.74, -3.1) * mm, "end": v(-1.74, -3.1) * mm});
            skLineSegment(sketch, "E2313", {"start": v(-0.7, -3.15) * mm, "end": v(-0.74, -3.15) * mm});
            skLineSegment(sketch, "E2314", {"start": v(-0.7, -3.19) * mm, "end": v(-0.74, -3.19) * mm});
            skLineSegment(sketch, "E2315", {"start": v(-0.74, -3.05) * mm, "end": v(-1.74, -3.05) * mm});
            skLineSegment(sketch, "E2316", {"start": v(-0.58, -3.03) * mm, "end": v(-0.74, -3.03) * mm});
            skLineSegment(sketch, "E2317", {"start": v(-0.01, -3.03) * mm, "end": v(-0.01, -3.13) * mm});
            skLineSegment(sketch, "E2318", {"start": v(-0.01, -3.15) * mm, "end": v(-0.01, -3.19) * mm});
            skLineSegment(sketch, "E2319", {"start": v(-0.74, -3.15) * mm, "end": v(-0.74, -3.19) * mm});
            skLineSegment(sketch, "E2320", {"start": v(-0.7, -3.15) * mm, "end": v(-0.7, -3.19) * mm});
            skLineSegment(sketch, "E2321", {"start": v(-0.58, -3.03) * mm, "end": v(-0.58, -3.13) * mm});
            skLineSegment(sketch, "E2322", {"start": v(-0.56, -3.03) * mm, "end": v(-0.56, -3.13) * mm});
            skLineSegment(sketch, "E2323", {"start": v(-0.52, -3.03) * mm, "end": v(-0.52, -3.13) * mm});
            skLineSegment(sketch, "E2324", {"start": v(-0.56, -3.03) * mm, "end": v(-0.52, -3.03) * mm});
            skLineSegment(sketch, "E2325", {"start": v(-0.52, -3.13) * mm, "end": v(-0.56, -3.13) * mm});
            skLineSegment(sketch, "E2326", {"start": v(-0.5, -3.03) * mm, "end": v(-0.5, -3.13) * mm});
            skLineSegment(sketch, "E2327", {"start": v(-0.46, -3.03) * mm, "end": v(-0.46, -3.13) * mm});
            skLineSegment(sketch, "E2328", {"start": v(-0.5, -3.03) * mm, "end": v(-0.46, -3.03) * mm});
            skLineSegment(sketch, "E2329", {"start": v(-0.46, -3.13) * mm, "end": v(-0.5, -3.13) * mm});
            skLineSegment(sketch, "E2330", {"start": v(-0.44, -3.03) * mm, "end": v(-0.44, -3.13) * mm});
            skLineSegment(sketch, "E2331", {"start": v(-0.4, -3.03) * mm, "end": v(-0.4, -3.13) * mm});
            skLineSegment(sketch, "E2332", {"start": v(-0.38, -3.03) * mm, "end": v(-0.38, -3.13) * mm});
            skLineSegment(sketch, "E2333", {"start": v(-0.33, -3.03) * mm, "end": v(-0.33, -3.13) * mm});
            skLineSegment(sketch, "E2334", {"start": v(-0.3, -3.03) * mm, "end": v(-0.3, -3.13) * mm});
            skLineSegment(sketch, "E2335", {"start": v(-0.25, -3.03) * mm, "end": v(-0.25, -3.13) * mm});
            skLineSegment(sketch, "E2336", {"start": v(-0.22, -3.03) * mm, "end": v(-0.22, -3.13) * mm});
            skLineSegment(sketch, "E2337", {"start": v(-0.15, -3.03) * mm, "end": v(-0.15, -3.13) * mm});
            skLineSegment(sketch, "E2338", {"start": v(-0.13, -3.03) * mm, "end": v(-0.13, -3.13) * mm});
            skLineSegment(sketch, "E2339", {"start": v(-0.44, -3.03) * mm, "end": v(-0.4, -3.03) * mm});
            skLineSegment(sketch, "E2340", {"start": v(-0.4, -3.13) * mm, "end": v(-0.44, -3.13) * mm});
            skLineSegment(sketch, "E2341", {"start": v(-0.7, -3.2) * mm, "end": v(-0.74, -3.2) * mm});
            skLineSegment(sketch, "E2342", {"start": v(-0.7, -3.25) * mm, "end": v(-0.74, -3.25) * mm});
            skLineSegment(sketch, "E2343", {"start": v(-0.74, -3.2) * mm, "end": v(-0.74, -3.25) * mm});
            skLineSegment(sketch, "E2344", {"start": v(-0.7, -3.2) * mm, "end": v(-0.7, -3.25) * mm});
            skLineSegment(sketch, "E2345", {"start": v(-0.7, -3.27) * mm, "end": v(-0.74, -3.27) * mm});
            skLineSegment(sketch, "E2346", {"start": v(-0.7, -3.3) * mm, "end": v(-0.74, -3.3) * mm});
            skLineSegment(sketch, "E2347", {"start": v(-0.74, -3.27) * mm, "end": v(-0.74, -3.3) * mm});
            skLineSegment(sketch, "E2348", {"start": v(-0.7, -3.27) * mm, "end": v(-0.7, -3.3) * mm});
            skLineSegment(sketch, "E2349", {"start": v(-0.7, -3.33) * mm, "end": v(-0.74, -3.33) * mm});
            skLineSegment(sketch, "E2350", {"start": v(-0.7, -3.37) * mm, "end": v(-0.74, -3.37) * mm});
            skLineSegment(sketch, "E2351", {"start": v(-0.74, -3.33) * mm, "end": v(-0.74, -3.37) * mm});
            skLineSegment(sketch, "E2352", {"start": v(-0.7, -3.33) * mm, "end": v(-0.7, -3.37) * mm});
            skLineSegment(sketch, "E2353", {"start": v(-0.64, -3.15) * mm, "end": v(-0.68, -3.15) * mm});
            skLineSegment(sketch, "E2354", {"start": v(-0.64, -3.19) * mm, "end": v(-0.68, -3.19) * mm});
            skLineSegment(sketch, "E2355", {"start": v(-0.68, -3.15) * mm, "end": v(-0.68, -3.19) * mm});
            skLineSegment(sketch, "E2356", {"start": v(-0.64, -3.15) * mm, "end": v(-0.64, -3.19) * mm});
            skLineSegment(sketch, "E2357", {"start": v(-0.64, -3.2) * mm, "end": v(-0.68, -3.2) * mm});
            skLineSegment(sketch, "E2358", {"start": v(-0.64, -3.25) * mm, "end": v(-0.68, -3.25) * mm});
            skLineSegment(sketch, "E2359", {"start": v(-0.68, -3.2) * mm, "end": v(-0.68, -3.25) * mm});
            skLineSegment(sketch, "E2360", {"start": v(-0.64, -3.2) * mm, "end": v(-0.64, -3.25) * mm});
            skLineSegment(sketch, "E2361", {"start": v(-0.64, -3.27) * mm, "end": v(-0.68, -3.27) * mm});
            skLineSegment(sketch, "E2362", {"start": v(-0.64, -3.3) * mm, "end": v(-0.68, -3.3) * mm});
            skLineSegment(sketch, "E2363", {"start": v(-0.68, -3.27) * mm, "end": v(-0.68, -3.3) * mm});
            skLineSegment(sketch, "E2364", {"start": v(-0.64, -3.27) * mm, "end": v(-0.64, -3.3) * mm});
            skLineSegment(sketch, "E2365", {"start": v(-0.64, -3.33) * mm, "end": v(-0.68, -3.33) * mm});
            skLineSegment(sketch, "E2366", {"start": v(-0.64, -3.37) * mm, "end": v(-0.68, -3.37) * mm});
            skLineSegment(sketch, "E2367", {"start": v(-0.68, -3.33) * mm, "end": v(-0.68, -3.37) * mm});
            skLineSegment(sketch, "E2368", {"start": v(-0.64, -3.33) * mm, "end": v(-0.64, -3.37) * mm});
            skLineSegment(sketch, "E2369", {"start": v(-0.58, -3.15) * mm, "end": v(-0.62, -3.15) * mm});
            skLineSegment(sketch, "E2370", {"start": v(-0.58, -3.19) * mm, "end": v(-0.62, -3.19) * mm});
            skLineSegment(sketch, "E2371", {"start": v(-0.62, -3.15) * mm, "end": v(-0.62, -3.19) * mm});
            skLineSegment(sketch, "E2372", {"start": v(-0.58, -3.15) * mm, "end": v(-0.58, -3.19) * mm});
            skLineSegment(sketch, "E2373", {"start": v(-0.58, -3.2) * mm, "end": v(-0.62, -3.2) * mm});
            skLineSegment(sketch, "E2374", {"start": v(-0.58, -3.25) * mm, "end": v(-0.62, -3.25) * mm});
            skLineSegment(sketch, "E2375", {"start": v(-0.62, -3.2) * mm, "end": v(-0.62, -3.25) * mm});
            skLineSegment(sketch, "E2376", {"start": v(-0.58, -3.2) * mm, "end": v(-0.58, -3.25) * mm});
            skLineSegment(sketch, "E2377", {"start": v(-0.58, -3.27) * mm, "end": v(-0.62, -3.27) * mm});
            skLineSegment(sketch, "E2378", {"start": v(-0.58, -3.3) * mm, "end": v(-0.62, -3.3) * mm});
            skLineSegment(sketch, "E2379", {"start": v(-0.62, -3.27) * mm, "end": v(-0.62, -3.3) * mm});
            skLineSegment(sketch, "E2380", {"start": v(-0.58, -3.27) * mm, "end": v(-0.58, -3.3) * mm});
            skLineSegment(sketch, "E2381", {"start": v(-0.58, -3.33) * mm, "end": v(-0.62, -3.33) * mm});
            skLineSegment(sketch, "E2382", {"start": v(-0.58, -3.37) * mm, "end": v(-0.62, -3.37) * mm});
            skLineSegment(sketch, "E2383", {"start": v(-0.62, -3.33) * mm, "end": v(-0.62, -3.37) * mm});
            skLineSegment(sketch, "E2384", {"start": v(-0.58, -3.33) * mm, "end": v(-0.58, -3.37) * mm});
            skLineSegment(sketch, "E2385", {"start": v(-0.52, -3.15) * mm, "end": v(-0.56, -3.15) * mm});
            skLineSegment(sketch, "E2386", {"start": v(-0.52, -3.19) * mm, "end": v(-0.56, -3.19) * mm});
            skLineSegment(sketch, "E2387", {"start": v(-0.56, -3.15) * mm, "end": v(-0.56, -3.19) * mm});
            skLineSegment(sketch, "E2388", {"start": v(-0.52, -3.15) * mm, "end": v(-0.52, -3.19) * mm});
            skLineSegment(sketch, "E2389", {"start": v(-0.52, -3.2) * mm, "end": v(-0.56, -3.2) * mm});
            skLineSegment(sketch, "E2390", {"start": v(-0.52, -3.25) * mm, "end": v(-0.56, -3.25) * mm});
            skLineSegment(sketch, "E2391", {"start": v(-0.56, -3.2) * mm, "end": v(-0.56, -3.25) * mm});
            skLineSegment(sketch, "E2392", {"start": v(-0.52, -3.2) * mm, "end": v(-0.52, -3.25) * mm});
            skLineSegment(sketch, "E2393", {"start": v(-0.52, -3.27) * mm, "end": v(-0.56, -3.27) * mm});
            skLineSegment(sketch, "E2394", {"start": v(-0.52, -3.3) * mm, "end": v(-0.56, -3.3) * mm});
            skLineSegment(sketch, "E2395", {"start": v(-0.56, -3.27) * mm, "end": v(-0.56, -3.3) * mm});
            skLineSegment(sketch, "E2396", {"start": v(-0.52, -3.27) * mm, "end": v(-0.52, -3.3) * mm});
            skLineSegment(sketch, "E2397", {"start": v(-0.52, -3.33) * mm, "end": v(-0.56, -3.33) * mm});
            skLineSegment(sketch, "E2398", {"start": v(-0.52, -3.37) * mm, "end": v(-0.56, -3.37) * mm});
            skLineSegment(sketch, "E2399", {"start": v(-0.56, -3.33) * mm, "end": v(-0.56, -3.37) * mm});
            skLineSegment(sketch, "E2400", {"start": v(-0.52, -3.33) * mm, "end": v(-0.52, -3.37) * mm});
            skLineSegment(sketch, "E2401", {"start": v(-0.46, -3.15) * mm, "end": v(-0.5, -3.15) * mm});
            skLineSegment(sketch, "E2402", {"start": v(-0.46, -3.19) * mm, "end": v(-0.5, -3.19) * mm});
            skLineSegment(sketch, "E2403", {"start": v(-0.5, -3.15) * mm, "end": v(-0.5, -3.19) * mm});
            skLineSegment(sketch, "E2404", {"start": v(-0.46, -3.15) * mm, "end": v(-0.46, -3.19) * mm});
            skLineSegment(sketch, "E2405", {"start": v(-0.46, -3.2) * mm, "end": v(-0.5, -3.2) * mm});
            skLineSegment(sketch, "E2406", {"start": v(-0.46, -3.25) * mm, "end": v(-0.5, -3.25) * mm});
            skLineSegment(sketch, "E2407", {"start": v(-0.5, -3.2) * mm, "end": v(-0.5, -3.25) * mm});
            skLineSegment(sketch, "E2408", {"start": v(-0.46, -3.2) * mm, "end": v(-0.46, -3.25) * mm});
            skLineSegment(sketch, "E2409", {"start": v(-0.46, -3.27) * mm, "end": v(-0.5, -3.27) * mm});
            skLineSegment(sketch, "E2410", {"start": v(-0.46, -3.3) * mm, "end": v(-0.5, -3.3) * mm});
            skLineSegment(sketch, "E2411", {"start": v(-0.5, -3.27) * mm, "end": v(-0.5, -3.3) * mm});
            skLineSegment(sketch, "E2412", {"start": v(-0.46, -3.27) * mm, "end": v(-0.46, -3.3) * mm});
            skLineSegment(sketch, "E2413", {"start": v(-0.46, -3.33) * mm, "end": v(-0.5, -3.33) * mm});
            skLineSegment(sketch, "E2414", {"start": v(-0.46, -3.37) * mm, "end": v(-0.5, -3.37) * mm});
            skLineSegment(sketch, "E2415", {"start": v(-0.5, -3.33) * mm, "end": v(-0.5, -3.37) * mm});
            skLineSegment(sketch, "E2416", {"start": v(-0.46, -3.33) * mm, "end": v(-0.46, -3.37) * mm});
            skLineSegment(sketch, "E2417", {"start": v(-0.4, -3.15) * mm, "end": v(-0.44, -3.15) * mm});
            skLineSegment(sketch, "E2418", {"start": v(-0.4, -3.19) * mm, "end": v(-0.44, -3.19) * mm});
            skLineSegment(sketch, "E2419", {"start": v(-0.44, -3.15) * mm, "end": v(-0.44, -3.19) * mm});
            skLineSegment(sketch, "E2420", {"start": v(-0.4, -3.15) * mm, "end": v(-0.4, -3.19) * mm});
            skLineSegment(sketch, "E2421", {"start": v(-0.38, -3.15) * mm, "end": v(-0.38, -3.19) * mm});
            skLineSegment(sketch, "E2422", {"start": v(-0.33, -3.15) * mm, "end": v(-0.33, -3.19) * mm});
            skLineSegment(sketch, "E2423", {"start": v(-0.3, -3.15) * mm, "end": v(-0.3, -3.19) * mm});
            skLineSegment(sketch, "E2424", {"start": v(-0.25, -3.15) * mm, "end": v(-0.25, -3.19) * mm});
            skLineSegment(sketch, "E2425", {"start": v(-0.22, -3.15) * mm, "end": v(-0.22, -3.19) * mm});
            skLineSegment(sketch, "E2426", {"start": v(-0.15, -3.15) * mm, "end": v(-0.15, -3.19) * mm});
            skLineSegment(sketch, "E2427", {"start": v(-0.13, -3.15) * mm, "end": v(-0.13, -3.19) * mm});
            skLineSegment(sketch, "E2428", {"start": v(-0.4, -3.2) * mm, "end": v(-0.44, -3.2) * mm});
            skLineSegment(sketch, "E2429", {"start": v(-0.4, -3.25) * mm, "end": v(-0.44, -3.25) * mm});
            skLineSegment(sketch, "E2430", {"start": v(-0.44, -3.2) * mm, "end": v(-0.44, -3.25) * mm});
            skLineSegment(sketch, "E2431", {"start": v(-0.4, -3.2) * mm, "end": v(-0.4, -3.25) * mm});
            skLineSegment(sketch, "E2432", {"start": v(-0.4, -3.27) * mm, "end": v(-0.44, -3.27) * mm});
            skLineSegment(sketch, "E2433", {"start": v(-0.4, -3.3) * mm, "end": v(-0.44, -3.3) * mm});
            skLineSegment(sketch, "E2434", {"start": v(-0.44, -3.27) * mm, "end": v(-0.44, -3.3) * mm});
            skLineSegment(sketch, "E2435", {"start": v(-0.4, -3.27) * mm, "end": v(-0.4, -3.3) * mm});
            skLineSegment(sketch, "E2436", {"start": v(-0.4, -3.33) * mm, "end": v(-0.44, -3.33) * mm});
            skLineSegment(sketch, "E2437", {"start": v(-0.4, -3.37) * mm, "end": v(-0.44, -3.37) * mm});
            skLineSegment(sketch, "E2438", {"start": v(-0.44, -3.33) * mm, "end": v(-0.44, -3.37) * mm});
            skLineSegment(sketch, "E2439", {"start": v(-0.4, -3.33) * mm, "end": v(-0.4, -3.37) * mm});
            skLineSegment(sketch, "E2440", {"start": v(-0.13, -3.15) * mm, "end": v(-0.01, -3.15) * mm});
            skLineSegment(sketch, "E2441", {"start": v(-0.13, -3.13) * mm, "end": v(-0.01, -3.13) * mm});
            skLineSegment(sketch, "E2442", {"start": v(-0.13, -3.03) * mm, "end": v(-0.01, -3.03) * mm});
            skLineSegment(sketch, "E2443", {"start": v(-0.13, -3.19) * mm, "end": v(-0.01, -3.19) * mm});
            skLineSegment(sketch, "E2444", {"start": v(-0.15, -3.15) * mm, "end": v(-0.22, -3.15) * mm});
            skLineSegment(sketch, "E2445", {"start": v(-0.22, -3.19) * mm, "end": v(-0.15, -3.19) * mm});
            skLineSegment(sketch, "E2446", {"start": v(-0.25, -3.15) * mm, "end": v(-0.3, -3.15) * mm});
            skLineSegment(sketch, "E2447", {"start": v(-0.3, -3.19) * mm, "end": v(-0.25, -3.19) * mm});
            skLineSegment(sketch, "E2448", {"start": v(-0.33, -3.15) * mm, "end": v(-0.38, -3.15) * mm});
            skLineSegment(sketch, "E2449", {"start": v(-0.38, -3.19) * mm, "end": v(-0.33, -3.19) * mm});
            skLineSegment(sketch, "E2450", {"start": v(-0.38, -3.13) * mm, "end": v(-0.33, -3.13) * mm});
            skLineSegment(sketch, "E2451", {"start": v(-0.3, -3.13) * mm, "end": v(-0.25, -3.13) * mm});
            skLineSegment(sketch, "E2452", {"start": v(-0.22, -3.13) * mm, "end": v(-0.15, -3.13) * mm});
            skLineSegment(sketch, "E2453", {"start": v(-0.38, -3.03) * mm, "end": v(-0.33, -3.03) * mm});
            skLineSegment(sketch, "E2454", {"start": v(-0.3, -3.03) * mm, "end": v(-0.25, -3.03) * mm});
            skLineSegment(sketch, "E2455", {"start": v(-0.22, -3.03) * mm, "end": v(-0.15, -3.03) * mm});
            skLineSegment(sketch, "E2456", {"start": v(-0.01, -3.2) * mm, "end": v(-0.01, -3.25) * mm});
            skLineSegment(sketch, "E2457", {"start": v(-0.38, -3.2) * mm, "end": v(-0.38, -3.25) * mm});
            skLineSegment(sketch, "E2458", {"start": v(-0.33, -3.2) * mm, "end": v(-0.33, -3.25) * mm});
            skLineSegment(sketch, "E2459", {"start": v(-0.3, -3.2) * mm, "end": v(-0.3, -3.25) * mm});
            skLineSegment(sketch, "E2460", {"start": v(-0.25, -3.2) * mm, "end": v(-0.25, -3.25) * mm});
            skLineSegment(sketch, "E2461", {"start": v(-0.22, -3.2) * mm, "end": v(-0.22, -3.25) * mm});
            skLineSegment(sketch, "E2462", {"start": v(-0.15, -3.2) * mm, "end": v(-0.15, -3.25) * mm});
            skLineSegment(sketch, "E2463", {"start": v(-0.13, -3.2) * mm, "end": v(-0.13, -3.25) * mm});
            skLineSegment(sketch, "E2464", {"start": v(-0.13, -3.2) * mm, "end": v(-0.01, -3.2) * mm});
            skLineSegment(sketch, "E2465", {"start": v(-0.13, -3.25) * mm, "end": v(-0.01, -3.25) * mm});
            skLineSegment(sketch, "E2466", {"start": v(-0.15, -3.2) * mm, "end": v(-0.22, -3.2) * mm});
            skLineSegment(sketch, "E2467", {"start": v(-0.22, -3.25) * mm, "end": v(-0.15, -3.25) * mm});
            skLineSegment(sketch, "E2468", {"start": v(-0.25, -3.2) * mm, "end": v(-0.3, -3.2) * mm});
            skLineSegment(sketch, "E2469", {"start": v(-0.3, -3.25) * mm, "end": v(-0.25, -3.25) * mm});
            skLineSegment(sketch, "E2470", {"start": v(-0.33, -3.2) * mm, "end": v(-0.38, -3.2) * mm});
            skLineSegment(sketch, "E2471", {"start": v(-0.38, -3.25) * mm, "end": v(-0.33, -3.25) * mm});
            skLineSegment(sketch, "E2472", {"start": v(-0.01, -3.27) * mm, "end": v(-0.01, -3.3) * mm});
            skLineSegment(sketch, "E2473", {"start": v(-0.38, -3.27) * mm, "end": v(-0.38, -3.3) * mm});
            skLineSegment(sketch, "E2474", {"start": v(-0.33, -3.27) * mm, "end": v(-0.33, -3.3) * mm});
            skLineSegment(sketch, "E2475", {"start": v(-0.3, -3.27) * mm, "end": v(-0.3, -3.3) * mm});
            skLineSegment(sketch, "E2476", {"start": v(-0.25, -3.27) * mm, "end": v(-0.25, -3.3) * mm});
            skLineSegment(sketch, "E2477", {"start": v(-0.22, -3.27) * mm, "end": v(-0.22, -3.3) * mm});
            skLineSegment(sketch, "E2478", {"start": v(-0.15, -3.27) * mm, "end": v(-0.15, -3.3) * mm});
            skLineSegment(sketch, "E2479", {"start": v(-0.13, -3.27) * mm, "end": v(-0.13, -3.3) * mm});
            skLineSegment(sketch, "E2480", {"start": v(-0.13, -3.27) * mm, "end": v(-0.01, -3.27) * mm});
            skLineSegment(sketch, "E2481", {"start": v(-0.13, -3.3) * mm, "end": v(-0.01, -3.3) * mm});
            skLineSegment(sketch, "E2482", {"start": v(-0.15, -3.27) * mm, "end": v(-0.22, -3.27) * mm});
            skLineSegment(sketch, "E2483", {"start": v(-0.22, -3.3) * mm, "end": v(-0.15, -3.3) * mm});
            skLineSegment(sketch, "E2484", {"start": v(-0.25, -3.27) * mm, "end": v(-0.3, -3.27) * mm});
            skLineSegment(sketch, "E2485", {"start": v(-0.3, -3.3) * mm, "end": v(-0.25, -3.3) * mm});
            skLineSegment(sketch, "E2486", {"start": v(-0.33, -3.27) * mm, "end": v(-0.38, -3.27) * mm});
            skLineSegment(sketch, "E2487", {"start": v(-0.38, -3.3) * mm, "end": v(-0.33, -3.3) * mm});
            skLineSegment(sketch, "E2488", {"start": v(-0.01, -3.33) * mm, "end": v(-0.01, -3.37) * mm});
            skLineSegment(sketch, "E2489", {"start": v(-0.38, -3.33) * mm, "end": v(-0.38, -3.37) * mm});
            skLineSegment(sketch, "E2490", {"start": v(-0.33, -3.33) * mm, "end": v(-0.33, -3.37) * mm});
            skLineSegment(sketch, "E2491", {"start": v(-0.3, -3.33) * mm, "end": v(-0.3, -3.37) * mm});
            skLineSegment(sketch, "E2492", {"start": v(-0.25, -3.33) * mm, "end": v(-0.25, -3.37) * mm});
            skLineSegment(sketch, "E2493", {"start": v(-0.22, -3.33) * mm, "end": v(-0.22, -3.37) * mm});
            skLineSegment(sketch, "E2494", {"start": v(-0.15, -3.33) * mm, "end": v(-0.15, -3.37) * mm});
            skLineSegment(sketch, "E2495", {"start": v(-0.13, -3.33) * mm, "end": v(-0.13, -3.37) * mm});
            skLineSegment(sketch, "E2496", {"start": v(-0.13, -3.33) * mm, "end": v(-0.01, -3.33) * mm});
            skLineSegment(sketch, "E2497", {"start": v(-0.13, -3.37) * mm, "end": v(-0.01, -3.37) * mm});
            skLineSegment(sketch, "E2498", {"start": v(-0.15, -3.33) * mm, "end": v(-0.22, -3.33) * mm});
            skLineSegment(sketch, "E2499", {"start": v(-0.22, -3.37) * mm, "end": v(-0.15, -3.37) * mm});
            skLineSegment(sketch, "E2500", {"start": v(-0.25, -3.33) * mm, "end": v(-0.3, -3.33) * mm});
            skLineSegment(sketch, "E2501", {"start": v(-0.3, -3.37) * mm, "end": v(-0.25, -3.37) * mm});
            skLineSegment(sketch, "E2502", {"start": v(-0.33, -3.33) * mm, "end": v(-0.38, -3.33) * mm});
            skLineSegment(sketch, "E2503", {"start": v(-0.38, -3.37) * mm, "end": v(-0.33, -3.37) * mm});
            skLineSegment(sketch, "E2504", {"start": v(0.58, -3.13) * mm, "end": v(0.74, -3.13) * mm});
            skLineSegment(sketch, "E2505", {"start": v(0.74, -3.1) * mm, "end": v(1.74, -3.1) * mm});
            skLineSegment(sketch, "E2506", {"start": v(0.7, -3.15) * mm, "end": v(0.74, -3.15) * mm});
            skLineSegment(sketch, "E2507", {"start": v(0.7, -3.19) * mm, "end": v(0.74, -3.19) * mm});
            skLineSegment(sketch, "E2508", {"start": v(0.74, -3.05) * mm, "end": v(1.74, -3.05) * mm});
            skLineSegment(sketch, "E2509", {"start": v(0.58, -3.03) * mm, "end": v(0.74, -3.03) * mm});
            skLineSegment(sketch, "E2510", {"start": v(0.01, -3.03) * mm, "end": v(0.01, -3.13) * mm});
            skLineSegment(sketch, "E2511", {"start": v(0.01, -3.15) * mm, "end": v(0.01, -3.19) * mm});
            skLineSegment(sketch, "E2512", {"start": v(0.74, -3.15) * mm, "end": v(0.74, -3.19) * mm});
            skLineSegment(sketch, "E2513", {"start": v(0.7, -3.15) * mm, "end": v(0.7, -3.19) * mm});
            skLineSegment(sketch, "E2514", {"start": v(0.58, -3.03) * mm, "end": v(0.58, -3.13) * mm});
            skLineSegment(sketch, "E2515", {"start": v(0.56, -3.03) * mm, "end": v(0.56, -3.13) * mm});
            skLineSegment(sketch, "E2516", {"start": v(0.52, -3.03) * mm, "end": v(0.52, -3.13) * mm});
            skLineSegment(sketch, "E2517", {"start": v(0.56, -3.03) * mm, "end": v(0.52, -3.03) * mm});
            skLineSegment(sketch, "E2518", {"start": v(0.52, -3.13) * mm, "end": v(0.56, -3.13) * mm});
            skLineSegment(sketch, "E2519", {"start": v(0.5, -3.03) * mm, "end": v(0.5, -3.13) * mm});
            skLineSegment(sketch, "E2520", {"start": v(0.46, -3.03) * mm, "end": v(0.46, -3.13) * mm});
            skLineSegment(sketch, "E2521", {"start": v(0.5, -3.03) * mm, "end": v(0.46, -3.03) * mm});
            skLineSegment(sketch, "E2522", {"start": v(0.46, -3.13) * mm, "end": v(0.5, -3.13) * mm});
            skLineSegment(sketch, "E2523", {"start": v(0.44, -3.03) * mm, "end": v(0.44, -3.13) * mm});
            skLineSegment(sketch, "E2524", {"start": v(0.4, -3.03) * mm, "end": v(0.4, -3.13) * mm});
            skLineSegment(sketch, "E2525", {"start": v(0.38, -3.03) * mm, "end": v(0.38, -3.13) * mm});
            skLineSegment(sketch, "E2526", {"start": v(0.33, -3.03) * mm, "end": v(0.33, -3.13) * mm});
            skLineSegment(sketch, "E2527", {"start": v(0.3, -3.03) * mm, "end": v(0.3, -3.13) * mm});
            skLineSegment(sketch, "E2528", {"start": v(0.25, -3.03) * mm, "end": v(0.25, -3.13) * mm});
            skLineSegment(sketch, "E2529", {"start": v(0.22, -3.03) * mm, "end": v(0.22, -3.13) * mm});
            skLineSegment(sketch, "E2530", {"start": v(0.15, -3.03) * mm, "end": v(0.15, -3.13) * mm});
            skLineSegment(sketch, "E2531", {"start": v(0.13, -3.03) * mm, "end": v(0.13, -3.13) * mm});
            skLineSegment(sketch, "E2532", {"start": v(0.44, -3.03) * mm, "end": v(0.4, -3.03) * mm});
            skLineSegment(sketch, "E2533", {"start": v(0.4, -3.13) * mm, "end": v(0.44, -3.13) * mm});
            skLineSegment(sketch, "E2534", {"start": v(0.7, -3.2) * mm, "end": v(0.74, -3.2) * mm});
            skLineSegment(sketch, "E2535", {"start": v(0.7, -3.25) * mm, "end": v(0.74, -3.25) * mm});
            skLineSegment(sketch, "E2536", {"start": v(0.74, -3.2) * mm, "end": v(0.74, -3.25) * mm});
            skLineSegment(sketch, "E2537", {"start": v(0.7, -3.2) * mm, "end": v(0.7, -3.25) * mm});
            skLineSegment(sketch, "E2538", {"start": v(0.7, -3.27) * mm, "end": v(0.74, -3.27) * mm});
            skLineSegment(sketch, "E2539", {"start": v(0.7, -3.3) * mm, "end": v(0.74, -3.3) * mm});
            skLineSegment(sketch, "E2540", {"start": v(0.74, -3.27) * mm, "end": v(0.74, -3.3) * mm});
            skLineSegment(sketch, "E2541", {"start": v(0.7, -3.27) * mm, "end": v(0.7, -3.3) * mm});
            skLineSegment(sketch, "E2542", {"start": v(0.7, -3.33) * mm, "end": v(0.74, -3.33) * mm});
            skLineSegment(sketch, "E2543", {"start": v(0.7, -3.37) * mm, "end": v(0.74, -3.37) * mm});
            skLineSegment(sketch, "E2544", {"start": v(0.74, -3.33) * mm, "end": v(0.74, -3.37) * mm});
            skLineSegment(sketch, "E2545", {"start": v(0.7, -3.33) * mm, "end": v(0.7, -3.37) * mm});
            skLineSegment(sketch, "E2546", {"start": v(0.64, -3.15) * mm, "end": v(0.68, -3.15) * mm});
            skLineSegment(sketch, "E2547", {"start": v(0.64, -3.19) * mm, "end": v(0.68, -3.19) * mm});
            skLineSegment(sketch, "E2548", {"start": v(0.68, -3.15) * mm, "end": v(0.68, -3.19) * mm});
            skLineSegment(sketch, "E2549", {"start": v(0.64, -3.15) * mm, "end": v(0.64, -3.19) * mm});
            skLineSegment(sketch, "E2550", {"start": v(0.64, -3.2) * mm, "end": v(0.68, -3.2) * mm});
            skLineSegment(sketch, "E2551", {"start": v(0.64, -3.25) * mm, "end": v(0.68, -3.25) * mm});
            skLineSegment(sketch, "E2552", {"start": v(0.68, -3.2) * mm, "end": v(0.68, -3.25) * mm});
            skLineSegment(sketch, "E2553", {"start": v(0.64, -3.2) * mm, "end": v(0.64, -3.25) * mm});
            skLineSegment(sketch, "E2554", {"start": v(0.64, -3.27) * mm, "end": v(0.68, -3.27) * mm});
            skLineSegment(sketch, "E2555", {"start": v(0.64, -3.3) * mm, "end": v(0.68, -3.3) * mm});
            skLineSegment(sketch, "E2556", {"start": v(0.68, -3.27) * mm, "end": v(0.68, -3.3) * mm});
            skLineSegment(sketch, "E2557", {"start": v(0.64, -3.27) * mm, "end": v(0.64, -3.3) * mm});
            skLineSegment(sketch, "E2558", {"start": v(0.64, -3.33) * mm, "end": v(0.68, -3.33) * mm});
            skLineSegment(sketch, "E2559", {"start": v(0.64, -3.37) * mm, "end": v(0.68, -3.37) * mm});
            skLineSegment(sketch, "E2560", {"start": v(0.68, -3.33) * mm, "end": v(0.68, -3.37) * mm});
            skLineSegment(sketch, "E2561", {"start": v(0.64, -3.33) * mm, "end": v(0.64, -3.37) * mm});
            skLineSegment(sketch, "E2562", {"start": v(0.58, -3.15) * mm, "end": v(0.62, -3.15) * mm});
            skLineSegment(sketch, "E2563", {"start": v(0.58, -3.19) * mm, "end": v(0.62, -3.19) * mm});
            skLineSegment(sketch, "E2564", {"start": v(0.62, -3.15) * mm, "end": v(0.62, -3.19) * mm});
            skLineSegment(sketch, "E2565", {"start": v(0.58, -3.15) * mm, "end": v(0.58, -3.19) * mm});
            skLineSegment(sketch, "E2566", {"start": v(0.58, -3.2) * mm, "end": v(0.62, -3.2) * mm});
            skLineSegment(sketch, "E2567", {"start": v(0.58, -3.25) * mm, "end": v(0.62, -3.25) * mm});
            skLineSegment(sketch, "E2568", {"start": v(0.62, -3.2) * mm, "end": v(0.62, -3.25) * mm});
            skLineSegment(sketch, "E2569", {"start": v(0.58, -3.2) * mm, "end": v(0.58, -3.25) * mm});
            skLineSegment(sketch, "E2570", {"start": v(0.58, -3.27) * mm, "end": v(0.62, -3.27) * mm});
            skLineSegment(sketch, "E2571", {"start": v(0.58, -3.3) * mm, "end": v(0.62, -3.3) * mm});
            skLineSegment(sketch, "E2572", {"start": v(0.62, -3.27) * mm, "end": v(0.62, -3.3) * mm});
            skLineSegment(sketch, "E2573", {"start": v(0.58, -3.27) * mm, "end": v(0.58, -3.3) * mm});
            skLineSegment(sketch, "E2574", {"start": v(0.58, -3.33) * mm, "end": v(0.62, -3.33) * mm});
            skLineSegment(sketch, "E2575", {"start": v(0.58, -3.37) * mm, "end": v(0.62, -3.37) * mm});
            skLineSegment(sketch, "E2576", {"start": v(0.62, -3.33) * mm, "end": v(0.62, -3.37) * mm});
            skLineSegment(sketch, "E2577", {"start": v(0.58, -3.33) * mm, "end": v(0.58, -3.37) * mm});
            skLineSegment(sketch, "E2578", {"start": v(0.52, -3.15) * mm, "end": v(0.56, -3.15) * mm});
            skLineSegment(sketch, "E2579", {"start": v(0.52, -3.19) * mm, "end": v(0.56, -3.19) * mm});
            skLineSegment(sketch, "E2580", {"start": v(0.56, -3.15) * mm, "end": v(0.56, -3.19) * mm});
            skLineSegment(sketch, "E2581", {"start": v(0.52, -3.15) * mm, "end": v(0.52, -3.19) * mm});
            skLineSegment(sketch, "E2582", {"start": v(0.52, -3.2) * mm, "end": v(0.56, -3.2) * mm});
            skLineSegment(sketch, "E2583", {"start": v(0.52, -3.25) * mm, "end": v(0.56, -3.25) * mm});
            skLineSegment(sketch, "E2584", {"start": v(0.56, -3.2) * mm, "end": v(0.56, -3.25) * mm});
            skLineSegment(sketch, "E2585", {"start": v(0.52, -3.2) * mm, "end": v(0.52, -3.25) * mm});
            skLineSegment(sketch, "E2586", {"start": v(0.52, -3.27) * mm, "end": v(0.56, -3.27) * mm});
            skLineSegment(sketch, "E2587", {"start": v(0.52, -3.3) * mm, "end": v(0.56, -3.3) * mm});
            skLineSegment(sketch, "E2588", {"start": v(0.56, -3.27) * mm, "end": v(0.56, -3.3) * mm});
            skLineSegment(sketch, "E2589", {"start": v(0.52, -3.27) * mm, "end": v(0.52, -3.3) * mm});
            skLineSegment(sketch, "E2590", {"start": v(0.52, -3.33) * mm, "end": v(0.56, -3.33) * mm});
            skLineSegment(sketch, "E2591", {"start": v(0.52, -3.37) * mm, "end": v(0.56, -3.37) * mm});
            skLineSegment(sketch, "E2592", {"start": v(0.56, -3.33) * mm, "end": v(0.56, -3.37) * mm});
            skLineSegment(sketch, "E2593", {"start": v(0.52, -3.33) * mm, "end": v(0.52, -3.37) * mm});
            skLineSegment(sketch, "E2594", {"start": v(0.46, -3.15) * mm, "end": v(0.5, -3.15) * mm});
            skLineSegment(sketch, "E2595", {"start": v(0.46, -3.19) * mm, "end": v(0.5, -3.19) * mm});
            skLineSegment(sketch, "E2596", {"start": v(0.5, -3.15) * mm, "end": v(0.5, -3.19) * mm});
            skLineSegment(sketch, "E2597", {"start": v(0.46, -3.15) * mm, "end": v(0.46, -3.19) * mm});
            skLineSegment(sketch, "E2598", {"start": v(0.46, -3.2) * mm, "end": v(0.5, -3.2) * mm});
            skLineSegment(sketch, "E2599", {"start": v(0.46, -3.25) * mm, "end": v(0.5, -3.25) * mm});
            skLineSegment(sketch, "E2600", {"start": v(0.5, -3.2) * mm, "end": v(0.5, -3.25) * mm});
            skLineSegment(sketch, "E2601", {"start": v(0.46, -3.2) * mm, "end": v(0.46, -3.25) * mm});
            skLineSegment(sketch, "E2602", {"start": v(0.46, -3.27) * mm, "end": v(0.5, -3.27) * mm});
            skLineSegment(sketch, "E2603", {"start": v(0.46, -3.3) * mm, "end": v(0.5, -3.3) * mm});
            skLineSegment(sketch, "E2604", {"start": v(0.5, -3.27) * mm, "end": v(0.5, -3.3) * mm});
            skLineSegment(sketch, "E2605", {"start": v(0.46, -3.27) * mm, "end": v(0.46, -3.3) * mm});
            skLineSegment(sketch, "E2606", {"start": v(0.46, -3.33) * mm, "end": v(0.5, -3.33) * mm});
            skLineSegment(sketch, "E2607", {"start": v(0.46, -3.37) * mm, "end": v(0.5, -3.37) * mm});
            skLineSegment(sketch, "E2608", {"start": v(0.5, -3.33) * mm, "end": v(0.5, -3.37) * mm});
            skLineSegment(sketch, "E2609", {"start": v(0.46, -3.33) * mm, "end": v(0.46, -3.37) * mm});
            skLineSegment(sketch, "E2610", {"start": v(0.4, -3.15) * mm, "end": v(0.44, -3.15) * mm});
            skLineSegment(sketch, "E2611", {"start": v(0.4, -3.19) * mm, "end": v(0.44, -3.19) * mm});
            skLineSegment(sketch, "E2612", {"start": v(0.44, -3.15) * mm, "end": v(0.44, -3.19) * mm});
            skLineSegment(sketch, "E2613", {"start": v(0.4, -3.15) * mm, "end": v(0.4, -3.19) * mm});
            skLineSegment(sketch, "E2614", {"start": v(0.38, -3.15) * mm, "end": v(0.38, -3.19) * mm});
            skLineSegment(sketch, "E2615", {"start": v(0.33, -3.15) * mm, "end": v(0.33, -3.19) * mm});
            skLineSegment(sketch, "E2616", {"start": v(0.3, -3.15) * mm, "end": v(0.3, -3.19) * mm});
            skLineSegment(sketch, "E2617", {"start": v(0.25, -3.15) * mm, "end": v(0.25, -3.19) * mm});
            skLineSegment(sketch, "E2618", {"start": v(0.22, -3.15) * mm, "end": v(0.22, -3.19) * mm});
            skLineSegment(sketch, "E2619", {"start": v(0.15, -3.15) * mm, "end": v(0.15, -3.19) * mm});
            skLineSegment(sketch, "E2620", {"start": v(0.13, -3.15) * mm, "end": v(0.13, -3.19) * mm});
            skLineSegment(sketch, "E2621", {"start": v(0.4, -3.2) * mm, "end": v(0.44, -3.2) * mm});
            skLineSegment(sketch, "E2622", {"start": v(0.4, -3.25) * mm, "end": v(0.44, -3.25) * mm});
            skLineSegment(sketch, "E2623", {"start": v(0.44, -3.2) * mm, "end": v(0.44, -3.25) * mm});
            skLineSegment(sketch, "E2624", {"start": v(0.4, -3.2) * mm, "end": v(0.4, -3.25) * mm});
            skLineSegment(sketch, "E2625", {"start": v(0.4, -3.27) * mm, "end": v(0.44, -3.27) * mm});
            skLineSegment(sketch, "E2626", {"start": v(0.4, -3.3) * mm, "end": v(0.44, -3.3) * mm});
            skLineSegment(sketch, "E2627", {"start": v(0.44, -3.27) * mm, "end": v(0.44, -3.3) * mm});
            skLineSegment(sketch, "E2628", {"start": v(0.4, -3.27) * mm, "end": v(0.4, -3.3) * mm});
            skLineSegment(sketch, "E2629", {"start": v(0.4, -3.33) * mm, "end": v(0.44, -3.33) * mm});
            skLineSegment(sketch, "E2630", {"start": v(0.4, -3.37) * mm, "end": v(0.44, -3.37) * mm});
            skLineSegment(sketch, "E2631", {"start": v(0.44, -3.33) * mm, "end": v(0.44, -3.37) * mm});
            skLineSegment(sketch, "E2632", {"start": v(0.4, -3.33) * mm, "end": v(0.4, -3.37) * mm});
            skLineSegment(sketch, "E2633", {"start": v(0.13, -3.15) * mm, "end": v(0.01, -3.15) * mm});
            skLineSegment(sketch, "E2634", {"start": v(0.13, -3.13) * mm, "end": v(0.01, -3.13) * mm});
            skLineSegment(sketch, "E2635", {"start": v(0.13, -3.03) * mm, "end": v(0.01, -3.03) * mm});
            skLineSegment(sketch, "E2636", {"start": v(0.13, -3.19) * mm, "end": v(0.01, -3.19) * mm});
            skLineSegment(sketch, "E2637", {"start": v(0.15, -3.15) * mm, "end": v(0.22, -3.15) * mm});
            skLineSegment(sketch, "E2638", {"start": v(0.22, -3.19) * mm, "end": v(0.15, -3.19) * mm});
            skLineSegment(sketch, "E2639", {"start": v(0.25, -3.15) * mm, "end": v(0.3, -3.15) * mm});
            skLineSegment(sketch, "E2640", {"start": v(0.3, -3.19) * mm, "end": v(0.25, -3.19) * mm});
            skLineSegment(sketch, "E2641", {"start": v(0.33, -3.15) * mm, "end": v(0.38, -3.15) * mm});
            skLineSegment(sketch, "E2642", {"start": v(0.38, -3.19) * mm, "end": v(0.33, -3.19) * mm});
            skLineSegment(sketch, "E2643", {"start": v(0.38, -3.13) * mm, "end": v(0.33, -3.13) * mm});
            skLineSegment(sketch, "E2644", {"start": v(0.3, -3.13) * mm, "end": v(0.25, -3.13) * mm});
            skLineSegment(sketch, "E2645", {"start": v(0.22, -3.13) * mm, "end": v(0.15, -3.13) * mm});
            skLineSegment(sketch, "E2646", {"start": v(0.38, -3.03) * mm, "end": v(0.33, -3.03) * mm});
            skLineSegment(sketch, "E2647", {"start": v(0.3, -3.03) * mm, "end": v(0.25, -3.03) * mm});
            skLineSegment(sketch, "E2648", {"start": v(0.22, -3.03) * mm, "end": v(0.15, -3.03) * mm});
            skLineSegment(sketch, "E2649", {"start": v(0.01, -3.2) * mm, "end": v(0.01, -3.25) * mm});
            skLineSegment(sketch, "E2650", {"start": v(0.38, -3.2) * mm, "end": v(0.38, -3.25) * mm});
            skLineSegment(sketch, "E2651", {"start": v(0.33, -3.2) * mm, "end": v(0.33, -3.25) * mm});
            skLineSegment(sketch, "E2652", {"start": v(0.3, -3.2) * mm, "end": v(0.3, -3.25) * mm});
            skLineSegment(sketch, "E2653", {"start": v(0.25, -3.2) * mm, "end": v(0.25, -3.25) * mm});
            skLineSegment(sketch, "E2654", {"start": v(0.22, -3.2) * mm, "end": v(0.22, -3.25) * mm});
            skLineSegment(sketch, "E2655", {"start": v(0.15, -3.2) * mm, "end": v(0.15, -3.25) * mm});
            skLineSegment(sketch, "E2656", {"start": v(0.13, -3.2) * mm, "end": v(0.13, -3.25) * mm});
            skLineSegment(sketch, "E2657", {"start": v(0.13, -3.2) * mm, "end": v(0.01, -3.2) * mm});
            skLineSegment(sketch, "E2658", {"start": v(0.13, -3.25) * mm, "end": v(0.01, -3.25) * mm});
            skLineSegment(sketch, "E2659", {"start": v(0.15, -3.2) * mm, "end": v(0.22, -3.2) * mm});
            skLineSegment(sketch, "E2660", {"start": v(0.22, -3.25) * mm, "end": v(0.15, -3.25) * mm});
            skLineSegment(sketch, "E2661", {"start": v(0.25, -3.2) * mm, "end": v(0.3, -3.2) * mm});
            skLineSegment(sketch, "E2662", {"start": v(0.3, -3.25) * mm, "end": v(0.25, -3.25) * mm});
            skLineSegment(sketch, "E2663", {"start": v(0.33, -3.2) * mm, "end": v(0.38, -3.2) * mm});
            skLineSegment(sketch, "E2664", {"start": v(0.38, -3.25) * mm, "end": v(0.33, -3.25) * mm});
            skLineSegment(sketch, "E2665", {"start": v(0.01, -3.27) * mm, "end": v(0.01, -3.3) * mm});
            skLineSegment(sketch, "E2666", {"start": v(0.38, -3.27) * mm, "end": v(0.38, -3.3) * mm});
            skLineSegment(sketch, "E2667", {"start": v(0.33, -3.27) * mm, "end": v(0.33, -3.3) * mm});
            skLineSegment(sketch, "E2668", {"start": v(0.3, -3.27) * mm, "end": v(0.3, -3.3) * mm});
            skLineSegment(sketch, "E2669", {"start": v(0.25, -3.27) * mm, "end": v(0.25, -3.3) * mm});
            skLineSegment(sketch, "E2670", {"start": v(0.22, -3.27) * mm, "end": v(0.22, -3.3) * mm});
            skLineSegment(sketch, "E2671", {"start": v(0.15, -3.27) * mm, "end": v(0.15, -3.3) * mm});
            skLineSegment(sketch, "E2672", {"start": v(0.13, -3.27) * mm, "end": v(0.13, -3.3) * mm});
            skLineSegment(sketch, "E2673", {"start": v(0.13, -3.27) * mm, "end": v(0.01, -3.27) * mm});
            skLineSegment(sketch, "E2674", {"start": v(0.13, -3.3) * mm, "end": v(0.01, -3.3) * mm});
            skLineSegment(sketch, "E2675", {"start": v(0.15, -3.27) * mm, "end": v(0.22, -3.27) * mm});
            skLineSegment(sketch, "E2676", {"start": v(0.22, -3.3) * mm, "end": v(0.15, -3.3) * mm});
            skLineSegment(sketch, "E2677", {"start": v(0.25, -3.27) * mm, "end": v(0.3, -3.27) * mm});
            skLineSegment(sketch, "E2678", {"start": v(0.3, -3.3) * mm, "end": v(0.25, -3.3) * mm});
            skLineSegment(sketch, "E2679", {"start": v(0.33, -3.27) * mm, "end": v(0.38, -3.27) * mm});
            skLineSegment(sketch, "E2680", {"start": v(0.38, -3.3) * mm, "end": v(0.33, -3.3) * mm});
            skLineSegment(sketch, "E2681", {"start": v(0.01, -3.33) * mm, "end": v(0.01, -3.37) * mm});
            skLineSegment(sketch, "E2682", {"start": v(0.38, -3.33) * mm, "end": v(0.38, -3.37) * mm});
            skLineSegment(sketch, "E2683", {"start": v(0.33, -3.33) * mm, "end": v(0.33, -3.37) * mm});
            skLineSegment(sketch, "E2684", {"start": v(0.3, -3.33) * mm, "end": v(0.3, -3.37) * mm});
            skLineSegment(sketch, "E2685", {"start": v(0.25, -3.33) * mm, "end": v(0.25, -3.37) * mm});
            skLineSegment(sketch, "E2686", {"start": v(0.22, -3.33) * mm, "end": v(0.22, -3.37) * mm});
            skLineSegment(sketch, "E2687", {"start": v(0.15, -3.33) * mm, "end": v(0.15, -3.37) * mm});
            skLineSegment(sketch, "E2688", {"start": v(0.13, -3.33) * mm, "end": v(0.13, -3.37) * mm});
            skLineSegment(sketch, "E2689", {"start": v(0.13, -3.33) * mm, "end": v(0.01, -3.33) * mm});
            skLineSegment(sketch, "E2690", {"start": v(0.13, -3.37) * mm, "end": v(0.01, -3.37) * mm});
            skLineSegment(sketch, "E2691", {"start": v(0.15, -3.33) * mm, "end": v(0.22, -3.33) * mm});
            skLineSegment(sketch, "E2692", {"start": v(0.22, -3.37) * mm, "end": v(0.15, -3.37) * mm});
            skLineSegment(sketch, "E2693", {"start": v(0.25, -3.33) * mm, "end": v(0.3, -3.33) * mm});
            skLineSegment(sketch, "E2694", {"start": v(0.3, -3.37) * mm, "end": v(0.25, -3.37) * mm});
            skLineSegment(sketch, "E2695", {"start": v(0.33, -3.33) * mm, "end": v(0.38, -3.33) * mm});
            skLineSegment(sketch, "E2696", {"start": v(0.38, -3.37) * mm, "end": v(0.33, -3.37) * mm});
            skLineSegment(sketch, "E2697", {"start": v(-0.74, -3.13) * mm, "end": v(-0.74, -3.1) * mm});
            skLineSegment(sketch, "E2698", {"start": v(-0.74, -3.05) * mm, "end": v(-0.74, -3.03) * mm});
            skLineSegment(sketch, "E2699", {"start": v(-0.58, -3.13) * mm, "end": v(-0.74, -3.13) * mm});
            skLineSegment(sketch, "E2700", {"start": v(0.74, -3.13) * mm, "end": v(0.74, -3.1) * mm});
            skLineSegment(sketch, "E2701", {"start": v(0.74, -3.05) * mm, "end": v(0.74, -3.03) * mm});
            skLineSegment(sketch, "E2702", {"start": v(1.74, -3.1) * mm, "end": v(1.74, -3.05) * mm});
            skLineSegment(sketch, "E2703", {"start": v(-1.74, -3.1) * mm, "end": v(-1.74, -3.05) * mm});
            skLineSegment(sketch, "E2704", {"start": v(-1.99, -0.98) * mm, "end": v(1.99, -0.98) * mm});
            skLineSegment(sketch, "E2705", {"start": v(1.99, -0.98) * mm, "end": v(1.99, -3.62) * mm});
            skLineSegment(sketch, "E2706", {"start": v(-1.99, -0.98) * mm, "end": v(-1.99, -3.62) * mm});
            skLineSegment(sketch, "E2707", {"start": v(1.99, -3.62) * mm, "end": v(-1.99, -3.62) * mm});
            skSolve(sketch);
        }
        {
            var Q0;
            Q0 = qSketchRegion(id + "F0", true);
            extrude(context, id + "F1", {"entities" : qUnion([Q0]), "depth" : .3 * mm});
        }
    });
